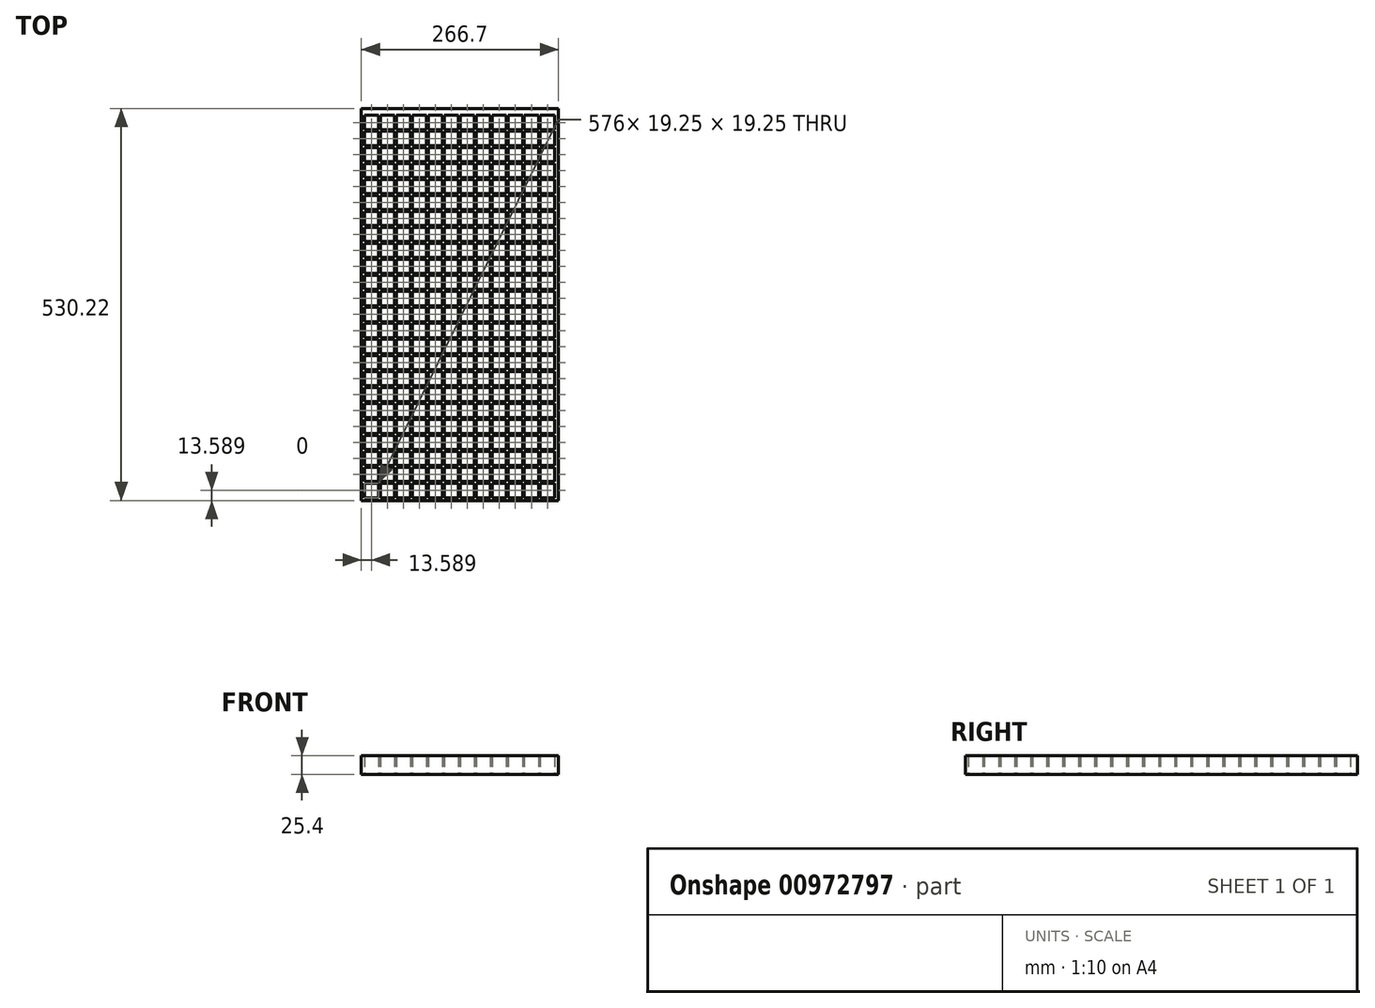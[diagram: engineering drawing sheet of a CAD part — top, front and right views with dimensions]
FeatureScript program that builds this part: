
annotation { "Feature Type Name" : "Feature", "Feature Type Description" : "" }
export const myFeature = defineFeature(function(context is Context, id is Id, definition is map)
    precondition{}
    {
        {
            var Q0;
            Q0=qCreatedBy(makeId("Top.planeOp"),FACE);
            var sketch = newSketch(context, id + "F0", { "sketchPlane" : qUnion([Q0])});
            skLineSegment(sketch, "E0.bottom", {"start": v(0, 0) * mm, "end": v(266.7, 0) * mm});
            skLineSegment(sketch, "E0.top", {"start": v(0, 530.23) * mm, "end": v(266.7, 530.23) * mm});
            skLineSegment(sketch, "E0.left", {"start": v(0, 0) * mm, "end": v(0, 530.23) * mm});
            skLineSegment(sketch, "E0.right", {"start": v(266.7, 0) * mm, "end": v(266.7, 530.22) * mm});
            skLineSegment(sketch, "E1.bottom", {"start": v(3.96, 23.22) * mm, "end": v(23.22, 23.22) * mm});
            skLineSegment(sketch, "E1.top", {"start": v(3.96, 3.96) * mm, "end": v(23.22, 3.96) * mm});
            skLineSegment(sketch, "E1.left", {"start": v(3.96, 23.22) * mm, "end": v(3.96, 3.96) * mm});
            skLineSegment(sketch, "E1.right", {"start": v(23.22, 23.22) * mm, "end": v(23.22, 3.96) * mm});
            skLineSegment(sketch, "E2.0.1.0", {"start": v(3.96, 44.86) * mm, "end": v(23.22, 44.86) * mm});
            skLineSegment(sketch, "E2.0.1.1", {"start": v(3.96, 25.6) * mm, "end": v(23.22, 25.6) * mm});
            skLineSegment(sketch, "E2.0.1.2", {"start": v(3.96, 44.86) * mm, "end": v(3.96, 25.6) * mm});
            skLineSegment(sketch, "E2.0.1.3", {"start": v(23.22, 44.86) * mm, "end": v(23.22, 25.6) * mm});
            skLineSegment(sketch, "E2.0.2.0", {"start": v(3.96, 66.5) * mm, "end": v(23.22, 66.5) * mm});
            skLineSegment(sketch, "E2.0.2.1", {"start": v(3.96, 47.24) * mm, "end": v(23.22, 47.24) * mm});
            skLineSegment(sketch, "E2.0.2.2", {"start": v(3.96, 66.5) * mm, "end": v(3.96, 47.24) * mm});
            skLineSegment(sketch, "E2.0.2.3", {"start": v(23.22, 66.5) * mm, "end": v(23.22, 47.24) * mm});
            skLineSegment(sketch, "E2.0.3.0", {"start": v(3.96, 88.14) * mm, "end": v(23.22, 88.14) * mm});
            skLineSegment(sketch, "E2.0.3.1", {"start": v(3.96, 68.88) * mm, "end": v(23.22, 68.88) * mm});
            skLineSegment(sketch, "E2.0.3.2", {"start": v(3.96, 88.14) * mm, "end": v(3.96, 68.88) * mm});
            skLineSegment(sketch, "E2.0.3.3", {"start": v(23.22, 88.14) * mm, "end": v(23.22, 68.88) * mm});
            skLineSegment(sketch, "E2.0.4.0", {"start": v(3.96, 109.78) * mm, "end": v(23.22, 109.78) * mm});
            skLineSegment(sketch, "E2.0.4.1", {"start": v(3.96, 90.53) * mm, "end": v(23.22, 90.53) * mm});
            skLineSegment(sketch, "E2.0.4.2", {"start": v(3.96, 109.78) * mm, "end": v(3.96, 90.53) * mm});
            skLineSegment(sketch, "E2.0.4.3", {"start": v(23.22, 109.78) * mm, "end": v(23.22, 90.53) * mm});
            skLineSegment(sketch, "E2.0.5.0", {"start": v(3.96, 131.42) * mm, "end": v(23.22, 131.42) * mm});
            skLineSegment(sketch, "E2.0.5.1", {"start": v(3.96, 112.17) * mm, "end": v(23.22, 112.17) * mm});
            skLineSegment(sketch, "E2.0.5.2", {"start": v(3.96, 131.42) * mm, "end": v(3.96, 112.17) * mm});
            skLineSegment(sketch, "E2.0.5.3", {"start": v(23.22, 131.42) * mm, "end": v(23.22, 112.17) * mm});
            skLineSegment(sketch, "E2.0.6.0", {"start": v(3.96, 153.06) * mm, "end": v(23.22, 153.06) * mm});
            skLineSegment(sketch, "E2.0.6.1", {"start": v(3.96, 133.8) * mm, "end": v(23.22, 133.8) * mm});
            skLineSegment(sketch, "E2.0.6.2", {"start": v(3.96, 153.06) * mm, "end": v(3.96, 133.8) * mm});
            skLineSegment(sketch, "E2.0.6.3", {"start": v(23.22, 153.06) * mm, "end": v(23.22, 133.8) * mm});
            skLineSegment(sketch, "E2.0.7.0", {"start": v(3.96, 174.7) * mm, "end": v(23.22, 174.7) * mm});
            skLineSegment(sketch, "E2.0.7.1", {"start": v(3.96, 155.45) * mm, "end": v(23.22, 155.45) * mm});
            skLineSegment(sketch, "E2.0.7.2", {"start": v(3.96, 174.7) * mm, "end": v(3.96, 155.45) * mm});
            skLineSegment(sketch, "E2.0.7.3", {"start": v(23.22, 174.7) * mm, "end": v(23.22, 155.45) * mm});
            skLineSegment(sketch, "E2.0.8.0", {"start": v(3.96, 196.34) * mm, "end": v(23.22, 196.34) * mm});
            skLineSegment(sketch, "E2.0.8.1", {"start": v(3.96, 177.09) * mm, "end": v(23.22, 177.09) * mm});
            skLineSegment(sketch, "E2.0.8.2", {"start": v(3.96, 196.34) * mm, "end": v(3.96, 177.09) * mm});
            skLineSegment(sketch, "E2.0.8.3", {"start": v(23.22, 196.34) * mm, "end": v(23.22, 177.09) * mm});
            skLineSegment(sketch, "E2.0.9.0", {"start": v(3.96, 217.98) * mm, "end": v(23.22, 217.98) * mm});
            skLineSegment(sketch, "E2.0.9.1", {"start": v(3.96, 198.73) * mm, "end": v(23.22, 198.73) * mm});
            skLineSegment(sketch, "E2.0.9.2", {"start": v(3.96, 217.98) * mm, "end": v(3.96, 198.73) * mm});
            skLineSegment(sketch, "E2.0.9.3", {"start": v(23.22, 217.98) * mm, "end": v(23.22, 198.73) * mm});
            skLineSegment(sketch, "E2.0.10.0", {"start": v(3.96, 239.62) * mm, "end": v(23.22, 239.62) * mm});
            skLineSegment(sketch, "E2.0.10.1", {"start": v(3.96, 220.37) * mm, "end": v(23.22, 220.37) * mm});
            skLineSegment(sketch, "E2.0.10.2", {"start": v(3.96, 239.62) * mm, "end": v(3.96, 220.37) * mm});
            skLineSegment(sketch, "E2.0.10.3", {"start": v(23.22, 239.62) * mm, "end": v(23.22, 220.37) * mm});
            skLineSegment(sketch, "E2.0.11.0", {"start": v(3.96, 261.26) * mm, "end": v(23.22, 261.26) * mm});
            skLineSegment(sketch, "E2.0.11.1", {"start": v(3.96, 242.01) * mm, "end": v(23.22, 242.01) * mm});
            skLineSegment(sketch, "E2.0.11.2", {"start": v(3.96, 261.26) * mm, "end": v(3.96, 242.01) * mm});
            skLineSegment(sketch, "E2.0.11.3", {"start": v(23.22, 261.26) * mm, "end": v(23.22, 242.01) * mm});
            skLineSegment(sketch, "E2.0.12.0", {"start": v(3.96, 282.9) * mm, "end": v(23.22, 282.9) * mm});
            skLineSegment(sketch, "E2.0.12.1", {"start": v(3.96, 263.65) * mm, "end": v(23.22, 263.65) * mm});
            skLineSegment(sketch, "E2.0.12.2", {"start": v(3.96, 282.9) * mm, "end": v(3.96, 263.65) * mm});
            skLineSegment(sketch, "E2.0.12.3", {"start": v(23.22, 282.9) * mm, "end": v(23.22, 263.65) * mm});
            skLineSegment(sketch, "E2.0.13.0", {"start": v(3.96, 304.55) * mm, "end": v(23.22, 304.55) * mm});
            skLineSegment(sketch, "E2.0.13.1", {"start": v(3.96, 285.3) * mm, "end": v(23.22, 285.3) * mm});
            skLineSegment(sketch, "E2.0.13.2", {"start": v(3.96, 304.55) * mm, "end": v(3.96, 285.3) * mm});
            skLineSegment(sketch, "E2.0.13.3", {"start": v(23.22, 304.55) * mm, "end": v(23.22, 285.3) * mm});
            skLineSegment(sketch, "E2.0.14.0", {"start": v(3.96, 326.19) * mm, "end": v(23.22, 326.19) * mm});
            skLineSegment(sketch, "E2.0.14.1", {"start": v(3.96, 306.93) * mm, "end": v(23.22, 306.93) * mm});
            skLineSegment(sketch, "E2.0.14.2", {"start": v(3.96, 326.19) * mm, "end": v(3.96, 306.93) * mm});
            skLineSegment(sketch, "E2.0.14.3", {"start": v(23.22, 326.19) * mm, "end": v(23.22, 306.93) * mm});
            skLineSegment(sketch, "E2.0.15.0", {"start": v(3.96, 347.83) * mm, "end": v(23.22, 347.83) * mm});
            skLineSegment(sketch, "E2.0.15.1", {"start": v(3.96, 328.57) * mm, "end": v(23.22, 328.57) * mm});
            skLineSegment(sketch, "E2.0.15.2", {"start": v(3.96, 347.83) * mm, "end": v(3.96, 328.57) * mm});
            skLineSegment(sketch, "E2.0.15.3", {"start": v(23.22, 347.83) * mm, "end": v(23.22, 328.57) * mm});
            skLineSegment(sketch, "E2.0.16.0", {"start": v(3.96, 369.47) * mm, "end": v(23.22, 369.47) * mm});
            skLineSegment(sketch, "E2.0.16.1", {"start": v(3.96, 350.22) * mm, "end": v(23.22, 350.22) * mm});
            skLineSegment(sketch, "E2.0.16.2", {"start": v(3.96, 369.47) * mm, "end": v(3.96, 350.22) * mm});
            skLineSegment(sketch, "E2.0.16.3", {"start": v(23.22, 369.47) * mm, "end": v(23.22, 350.22) * mm});
            skLineSegment(sketch, "E2.0.17.0", {"start": v(3.96, 391.1) * mm, "end": v(23.22, 391.1) * mm});
            skLineSegment(sketch, "E2.0.17.1", {"start": v(3.96, 371.86) * mm, "end": v(23.22, 371.86) * mm});
            skLineSegment(sketch, "E2.0.17.2", {"start": v(3.96, 391.1) * mm, "end": v(3.96, 371.86) * mm});
            skLineSegment(sketch, "E2.0.17.3", {"start": v(23.22, 391.1) * mm, "end": v(23.22, 371.86) * mm});
            skLineSegment(sketch, "E2.0.18.0", {"start": v(3.96, 412.75) * mm, "end": v(23.22, 412.75) * mm});
            skLineSegment(sketch, "E2.0.18.1", {"start": v(3.96, 393.5) * mm, "end": v(23.22, 393.5) * mm});
            skLineSegment(sketch, "E2.0.18.2", {"start": v(3.96, 412.75) * mm, "end": v(3.96, 393.5) * mm});
            skLineSegment(sketch, "E2.0.18.3", {"start": v(23.22, 412.75) * mm, "end": v(23.22, 393.5) * mm});
            skLineSegment(sketch, "E2.0.19.0", {"start": v(3.96, 434.4) * mm, "end": v(23.22, 434.4) * mm});
            skLineSegment(sketch, "E2.0.19.1", {"start": v(3.96, 415.14) * mm, "end": v(23.22, 415.14) * mm});
            skLineSegment(sketch, "E2.0.19.2", {"start": v(3.96, 434.4) * mm, "end": v(3.96, 415.14) * mm});
            skLineSegment(sketch, "E2.0.19.3", {"start": v(23.22, 434.4) * mm, "end": v(23.22, 415.14) * mm});
            skLineSegment(sketch, "E2.0.20.0", {"start": v(3.96, 456.03) * mm, "end": v(23.22, 456.03) * mm});
            skLineSegment(sketch, "E2.0.20.1", {"start": v(3.96, 436.78) * mm, "end": v(23.22, 436.78) * mm});
            skLineSegment(sketch, "E2.0.20.2", {"start": v(3.96, 456.03) * mm, "end": v(3.96, 436.78) * mm});
            skLineSegment(sketch, "E2.0.20.3", {"start": v(23.22, 456.03) * mm, "end": v(23.22, 436.78) * mm});
            skLineSegment(sketch, "E2.0.21.0", {"start": v(3.96, 477.67) * mm, "end": v(23.22, 477.67) * mm});
            skLineSegment(sketch, "E2.0.21.1", {"start": v(3.96, 458.42) * mm, "end": v(23.22, 458.42) * mm});
            skLineSegment(sketch, "E2.0.21.2", {"start": v(3.96, 477.67) * mm, "end": v(3.96, 458.42) * mm});
            skLineSegment(sketch, "E2.0.21.3", {"start": v(23.22, 477.67) * mm, "end": v(23.22, 458.42) * mm});
            skLineSegment(sketch, "E2.0.22.0", {"start": v(3.96, 499.31) * mm, "end": v(23.22, 499.31) * mm});
            skLineSegment(sketch, "E2.0.22.1", {"start": v(3.96, 480.06) * mm, "end": v(23.22, 480.06) * mm});
            skLineSegment(sketch, "E2.0.22.2", {"start": v(3.96, 499.31) * mm, "end": v(3.96, 480.06) * mm});
            skLineSegment(sketch, "E2.0.22.3", {"start": v(23.22, 499.31) * mm, "end": v(23.22, 480.06) * mm});
            skLineSegment(sketch, "E2.0.23.0", {"start": v(3.96, 520.95) * mm, "end": v(23.22, 520.95) * mm});
            skLineSegment(sketch, "E2.0.23.1", {"start": v(3.96, 501.7) * mm, "end": v(23.22, 501.7) * mm});
            skLineSegment(sketch, "E2.0.23.2", {"start": v(3.96, 520.95) * mm, "end": v(3.96, 501.7) * mm});
            skLineSegment(sketch, "E2.0.23.3", {"start": v(23.22, 520.95) * mm, "end": v(23.22, 501.7) * mm});
            skLineSegment(sketch, "E2.1.0.0", {"start": v(25.6, 23.22) * mm, "end": v(44.86, 23.22) * mm});
            skLineSegment(sketch, "E2.1.0.1", {"start": v(25.6, 3.96) * mm, "end": v(44.86, 3.96) * mm});
            skLineSegment(sketch, "E2.1.0.2", {"start": v(25.6, 23.22) * mm, "end": v(25.6, 3.96) * mm});
            skLineSegment(sketch, "E2.1.0.3", {"start": v(44.86, 23.22) * mm, "end": v(44.86, 3.96) * mm});
            skLineSegment(sketch, "E2.1.1.0", {"start": v(25.6, 44.86) * mm, "end": v(44.86, 44.86) * mm});
            skLineSegment(sketch, "E2.1.1.1", {"start": v(25.6, 25.6) * mm, "end": v(44.86, 25.6) * mm});
            skLineSegment(sketch, "E2.1.1.2", {"start": v(25.6, 44.86) * mm, "end": v(25.6, 25.6) * mm});
            skLineSegment(sketch, "E2.1.1.3", {"start": v(44.86, 44.86) * mm, "end": v(44.86, 25.6) * mm});
            skLineSegment(sketch, "E2.1.2.0", {"start": v(25.6, 66.5) * mm, "end": v(44.86, 66.5) * mm});
            skLineSegment(sketch, "E2.1.2.1", {"start": v(25.6, 47.24) * mm, "end": v(44.86, 47.24) * mm});
            skLineSegment(sketch, "E2.1.2.2", {"start": v(25.6, 66.5) * mm, "end": v(25.6, 47.24) * mm});
            skLineSegment(sketch, "E2.1.2.3", {"start": v(44.86, 66.5) * mm, "end": v(44.86, 47.24) * mm});
            skLineSegment(sketch, "E2.1.3.0", {"start": v(25.6, 88.14) * mm, "end": v(44.86, 88.14) * mm});
            skLineSegment(sketch, "E2.1.3.1", {"start": v(25.6, 68.88) * mm, "end": v(44.86, 68.88) * mm});
            skLineSegment(sketch, "E2.1.3.2", {"start": v(25.6, 88.14) * mm, "end": v(25.6, 68.88) * mm});
            skLineSegment(sketch, "E2.1.3.3", {"start": v(44.86, 88.14) * mm, "end": v(44.86, 68.88) * mm});
            skLineSegment(sketch, "E2.1.4.0", {"start": v(25.6, 109.78) * mm, "end": v(44.86, 109.78) * mm});
            skLineSegment(sketch, "E2.1.4.1", {"start": v(25.6, 90.53) * mm, "end": v(44.86, 90.53) * mm});
            skLineSegment(sketch, "E2.1.4.2", {"start": v(25.6, 109.78) * mm, "end": v(25.6, 90.53) * mm});
            skLineSegment(sketch, "E2.1.4.3", {"start": v(44.86, 109.78) * mm, "end": v(44.86, 90.53) * mm});
            skLineSegment(sketch, "E2.1.5.0", {"start": v(25.6, 131.42) * mm, "end": v(44.86, 131.42) * mm});
            skLineSegment(sketch, "E2.1.5.1", {"start": v(25.6, 112.17) * mm, "end": v(44.86, 112.17) * mm});
            skLineSegment(sketch, "E2.1.5.2", {"start": v(25.6, 131.42) * mm, "end": v(25.6, 112.17) * mm});
            skLineSegment(sketch, "E2.1.5.3", {"start": v(44.86, 131.42) * mm, "end": v(44.86, 112.17) * mm});
            skLineSegment(sketch, "E2.1.6.0", {"start": v(25.6, 153.06) * mm, "end": v(44.86, 153.06) * mm});
            skLineSegment(sketch, "E2.1.6.1", {"start": v(25.6, 133.8) * mm, "end": v(44.86, 133.8) * mm});
            skLineSegment(sketch, "E2.1.6.2", {"start": v(25.6, 153.06) * mm, "end": v(25.6, 133.8) * mm});
            skLineSegment(sketch, "E2.1.6.3", {"start": v(44.86, 153.06) * mm, "end": v(44.86, 133.8) * mm});
            skLineSegment(sketch, "E2.1.7.0", {"start": v(25.6, 174.7) * mm, "end": v(44.86, 174.7) * mm});
            skLineSegment(sketch, "E2.1.7.1", {"start": v(25.6, 155.45) * mm, "end": v(44.86, 155.45) * mm});
            skLineSegment(sketch, "E2.1.7.2", {"start": v(25.6, 174.7) * mm, "end": v(25.6, 155.45) * mm});
            skLineSegment(sketch, "E2.1.7.3", {"start": v(44.86, 174.7) * mm, "end": v(44.86, 155.45) * mm});
            skLineSegment(sketch, "E2.1.8.0", {"start": v(25.6, 196.34) * mm, "end": v(44.86, 196.34) * mm});
            skLineSegment(sketch, "E2.1.8.1", {"start": v(25.6, 177.09) * mm, "end": v(44.86, 177.09) * mm});
            skLineSegment(sketch, "E2.1.8.2", {"start": v(25.6, 196.34) * mm, "end": v(25.6, 177.09) * mm});
            skLineSegment(sketch, "E2.1.8.3", {"start": v(44.86, 196.34) * mm, "end": v(44.86, 177.09) * mm});
            skLineSegment(sketch, "E2.1.9.0", {"start": v(25.6, 217.98) * mm, "end": v(44.86, 217.98) * mm});
            skLineSegment(sketch, "E2.1.9.1", {"start": v(25.6, 198.73) * mm, "end": v(44.86, 198.73) * mm});
            skLineSegment(sketch, "E2.1.9.2", {"start": v(25.6, 217.98) * mm, "end": v(25.6, 198.73) * mm});
            skLineSegment(sketch, "E2.1.9.3", {"start": v(44.86, 217.98) * mm, "end": v(44.86, 198.73) * mm});
            skLineSegment(sketch, "E2.1.10.0", {"start": v(25.6, 239.62) * mm, "end": v(44.86, 239.62) * mm});
            skLineSegment(sketch, "E2.1.10.1", {"start": v(25.6, 220.37) * mm, "end": v(44.86, 220.37) * mm});
            skLineSegment(sketch, "E2.1.10.2", {"start": v(25.6, 239.62) * mm, "end": v(25.6, 220.37) * mm});
            skLineSegment(sketch, "E2.1.10.3", {"start": v(44.86, 239.62) * mm, "end": v(44.86, 220.37) * mm});
            skLineSegment(sketch, "E2.1.11.0", {"start": v(25.6, 261.26) * mm, "end": v(44.86, 261.26) * mm});
            skLineSegment(sketch, "E2.1.11.1", {"start": v(25.6, 242.01) * mm, "end": v(44.86, 242.01) * mm});
            skLineSegment(sketch, "E2.1.11.2", {"start": v(25.6, 261.26) * mm, "end": v(25.6, 242.01) * mm});
            skLineSegment(sketch, "E2.1.11.3", {"start": v(44.86, 261.26) * mm, "end": v(44.86, 242.01) * mm});
            skLineSegment(sketch, "E2.1.12.0", {"start": v(25.6, 282.9) * mm, "end": v(44.86, 282.9) * mm});
            skLineSegment(sketch, "E2.1.12.1", {"start": v(25.6, 263.65) * mm, "end": v(44.86, 263.65) * mm});
            skLineSegment(sketch, "E2.1.12.2", {"start": v(25.6, 282.9) * mm, "end": v(25.6, 263.65) * mm});
            skLineSegment(sketch, "E2.1.12.3", {"start": v(44.86, 282.9) * mm, "end": v(44.86, 263.65) * mm});
            skLineSegment(sketch, "E2.1.13.0", {"start": v(25.6, 304.55) * mm, "end": v(44.86, 304.55) * mm});
            skLineSegment(sketch, "E2.1.13.1", {"start": v(25.6, 285.3) * mm, "end": v(44.86, 285.3) * mm});
            skLineSegment(sketch, "E2.1.13.2", {"start": v(25.6, 304.55) * mm, "end": v(25.6, 285.3) * mm});
            skLineSegment(sketch, "E2.1.13.3", {"start": v(44.86, 304.55) * mm, "end": v(44.86, 285.3) * mm});
            skLineSegment(sketch, "E2.1.14.0", {"start": v(25.6, 326.19) * mm, "end": v(44.86, 326.19) * mm});
            skLineSegment(sketch, "E2.1.14.1", {"start": v(25.6, 306.93) * mm, "end": v(44.86, 306.93) * mm});
            skLineSegment(sketch, "E2.1.14.2", {"start": v(25.6, 326.19) * mm, "end": v(25.6, 306.93) * mm});
            skLineSegment(sketch, "E2.1.14.3", {"start": v(44.86, 326.19) * mm, "end": v(44.86, 306.93) * mm});
            skLineSegment(sketch, "E2.1.15.0", {"start": v(25.6, 347.83) * mm, "end": v(44.86, 347.83) * mm});
            skLineSegment(sketch, "E2.1.15.1", {"start": v(25.6, 328.57) * mm, "end": v(44.86, 328.57) * mm});
            skLineSegment(sketch, "E2.1.15.2", {"start": v(25.6, 347.83) * mm, "end": v(25.6, 328.57) * mm});
            skLineSegment(sketch, "E2.1.15.3", {"start": v(44.86, 347.83) * mm, "end": v(44.86, 328.57) * mm});
            skLineSegment(sketch, "E2.1.16.0", {"start": v(25.6, 369.47) * mm, "end": v(44.86, 369.47) * mm});
            skLineSegment(sketch, "E2.1.16.1", {"start": v(25.6, 350.22) * mm, "end": v(44.86, 350.22) * mm});
            skLineSegment(sketch, "E2.1.16.2", {"start": v(25.6, 369.47) * mm, "end": v(25.6, 350.22) * mm});
            skLineSegment(sketch, "E2.1.16.3", {"start": v(44.86, 369.47) * mm, "end": v(44.86, 350.22) * mm});
            skLineSegment(sketch, "E2.1.17.0", {"start": v(25.6, 391.1) * mm, "end": v(44.86, 391.1) * mm});
            skLineSegment(sketch, "E2.1.17.1", {"start": v(25.6, 371.86) * mm, "end": v(44.86, 371.86) * mm});
            skLineSegment(sketch, "E2.1.17.2", {"start": v(25.6, 391.1) * mm, "end": v(25.6, 371.86) * mm});
            skLineSegment(sketch, "E2.1.17.3", {"start": v(44.86, 391.1) * mm, "end": v(44.86, 371.86) * mm});
            skLineSegment(sketch, "E2.1.18.0", {"start": v(25.6, 412.75) * mm, "end": v(44.86, 412.75) * mm});
            skLineSegment(sketch, "E2.1.18.1", {"start": v(25.6, 393.5) * mm, "end": v(44.86, 393.5) * mm});
            skLineSegment(sketch, "E2.1.18.2", {"start": v(25.6, 412.75) * mm, "end": v(25.6, 393.5) * mm});
            skLineSegment(sketch, "E2.1.18.3", {"start": v(44.86, 412.75) * mm, "end": v(44.86, 393.5) * mm});
            skLineSegment(sketch, "E2.1.19.0", {"start": v(25.6, 434.4) * mm, "end": v(44.86, 434.4) * mm});
            skLineSegment(sketch, "E2.1.19.1", {"start": v(25.6, 415.14) * mm, "end": v(44.86, 415.14) * mm});
            skLineSegment(sketch, "E2.1.19.2", {"start": v(25.6, 434.4) * mm, "end": v(25.6, 415.14) * mm});
            skLineSegment(sketch, "E2.1.19.3", {"start": v(44.86, 434.4) * mm, "end": v(44.86, 415.14) * mm});
            skLineSegment(sketch, "E2.1.20.0", {"start": v(25.6, 456.03) * mm, "end": v(44.86, 456.03) * mm});
            skLineSegment(sketch, "E2.1.20.1", {"start": v(25.6, 436.78) * mm, "end": v(44.86, 436.78) * mm});
            skLineSegment(sketch, "E2.1.20.2", {"start": v(25.6, 456.03) * mm, "end": v(25.6, 436.78) * mm});
            skLineSegment(sketch, "E2.1.20.3", {"start": v(44.86, 456.03) * mm, "end": v(44.86, 436.78) * mm});
            skLineSegment(sketch, "E2.1.21.0", {"start": v(25.6, 477.67) * mm, "end": v(44.86, 477.67) * mm});
            skLineSegment(sketch, "E2.1.21.1", {"start": v(25.6, 458.42) * mm, "end": v(44.86, 458.42) * mm});
            skLineSegment(sketch, "E2.1.21.2", {"start": v(25.6, 477.67) * mm, "end": v(25.6, 458.42) * mm});
            skLineSegment(sketch, "E2.1.21.3", {"start": v(44.86, 477.67) * mm, "end": v(44.86, 458.42) * mm});
            skLineSegment(sketch, "E2.1.22.0", {"start": v(25.6, 499.31) * mm, "end": v(44.86, 499.31) * mm});
            skLineSegment(sketch, "E2.1.22.1", {"start": v(25.6, 480.06) * mm, "end": v(44.86, 480.06) * mm});
            skLineSegment(sketch, "E2.1.22.2", {"start": v(25.6, 499.31) * mm, "end": v(25.6, 480.06) * mm});
            skLineSegment(sketch, "E2.1.22.3", {"start": v(44.86, 499.31) * mm, "end": v(44.86, 480.06) * mm});
            skLineSegment(sketch, "E2.1.23.0", {"start": v(25.6, 520.95) * mm, "end": v(44.86, 520.95) * mm});
            skLineSegment(sketch, "E2.1.23.1", {"start": v(25.6, 501.7) * mm, "end": v(44.86, 501.7) * mm});
            skLineSegment(sketch, "E2.1.23.2", {"start": v(25.6, 520.95) * mm, "end": v(25.6, 501.7) * mm});
            skLineSegment(sketch, "E2.1.23.3", {"start": v(44.86, 520.95) * mm, "end": v(44.86, 501.7) * mm});
            skLineSegment(sketch, "E2.2.0.0", {"start": v(47.24, 23.22) * mm, "end": v(66.5, 23.22) * mm});
            skLineSegment(sketch, "E2.2.0.1", {"start": v(47.24, 3.96) * mm, "end": v(66.5, 3.96) * mm});
            skLineSegment(sketch, "E2.2.0.2", {"start": v(47.24, 23.22) * mm, "end": v(47.24, 3.96) * mm});
            skLineSegment(sketch, "E2.2.0.3", {"start": v(66.5, 23.22) * mm, "end": v(66.5, 3.96) * mm});
            skLineSegment(sketch, "E2.2.1.0", {"start": v(47.24, 44.86) * mm, "end": v(66.5, 44.86) * mm});
            skLineSegment(sketch, "E2.2.1.1", {"start": v(47.24, 25.6) * mm, "end": v(66.5, 25.6) * mm});
            skLineSegment(sketch, "E2.2.1.2", {"start": v(47.24, 44.86) * mm, "end": v(47.24, 25.6) * mm});
            skLineSegment(sketch, "E2.2.1.3", {"start": v(66.5, 44.86) * mm, "end": v(66.5, 25.6) * mm});
            skLineSegment(sketch, "E2.2.2.0", {"start": v(47.24, 66.5) * mm, "end": v(66.5, 66.5) * mm});
            skLineSegment(sketch, "E2.2.2.1", {"start": v(47.24, 47.24) * mm, "end": v(66.5, 47.24) * mm});
            skLineSegment(sketch, "E2.2.2.2", {"start": v(47.24, 66.5) * mm, "end": v(47.24, 47.24) * mm});
            skLineSegment(sketch, "E2.2.2.3", {"start": v(66.5, 66.5) * mm, "end": v(66.5, 47.24) * mm});
            skLineSegment(sketch, "E2.2.3.0", {"start": v(47.24, 88.14) * mm, "end": v(66.5, 88.14) * mm});
            skLineSegment(sketch, "E2.2.3.1", {"start": v(47.24, 68.88) * mm, "end": v(66.5, 68.88) * mm});
            skLineSegment(sketch, "E2.2.3.2", {"start": v(47.24, 88.14) * mm, "end": v(47.24, 68.88) * mm});
            skLineSegment(sketch, "E2.2.3.3", {"start": v(66.5, 88.14) * mm, "end": v(66.5, 68.88) * mm});
            skLineSegment(sketch, "E2.2.4.0", {"start": v(47.24, 109.78) * mm, "end": v(66.5, 109.78) * mm});
            skLineSegment(sketch, "E2.2.4.1", {"start": v(47.24, 90.53) * mm, "end": v(66.5, 90.53) * mm});
            skLineSegment(sketch, "E2.2.4.2", {"start": v(47.24, 109.78) * mm, "end": v(47.24, 90.53) * mm});
            skLineSegment(sketch, "E2.2.4.3", {"start": v(66.5, 109.78) * mm, "end": v(66.5, 90.53) * mm});
            skLineSegment(sketch, "E2.2.5.0", {"start": v(47.24, 131.42) * mm, "end": v(66.5, 131.42) * mm});
            skLineSegment(sketch, "E2.2.5.1", {"start": v(47.24, 112.17) * mm, "end": v(66.5, 112.17) * mm});
            skLineSegment(sketch, "E2.2.5.2", {"start": v(47.24, 131.42) * mm, "end": v(47.24, 112.17) * mm});
            skLineSegment(sketch, "E2.2.5.3", {"start": v(66.5, 131.42) * mm, "end": v(66.5, 112.17) * mm});
            skLineSegment(sketch, "E2.2.6.0", {"start": v(47.24, 153.06) * mm, "end": v(66.5, 153.06) * mm});
            skLineSegment(sketch, "E2.2.6.1", {"start": v(47.24, 133.8) * mm, "end": v(66.5, 133.8) * mm});
            skLineSegment(sketch, "E2.2.6.2", {"start": v(47.24, 153.06) * mm, "end": v(47.24, 133.8) * mm});
            skLineSegment(sketch, "E2.2.6.3", {"start": v(66.5, 153.06) * mm, "end": v(66.5, 133.8) * mm});
            skLineSegment(sketch, "E2.2.7.0", {"start": v(47.24, 174.7) * mm, "end": v(66.5, 174.7) * mm});
            skLineSegment(sketch, "E2.2.7.1", {"start": v(47.24, 155.45) * mm, "end": v(66.5, 155.45) * mm});
            skLineSegment(sketch, "E2.2.7.2", {"start": v(47.24, 174.7) * mm, "end": v(47.24, 155.45) * mm});
            skLineSegment(sketch, "E2.2.7.3", {"start": v(66.5, 174.7) * mm, "end": v(66.5, 155.45) * mm});
            skLineSegment(sketch, "E2.2.8.0", {"start": v(47.24, 196.34) * mm, "end": v(66.5, 196.34) * mm});
            skLineSegment(sketch, "E2.2.8.1", {"start": v(47.24, 177.09) * mm, "end": v(66.5, 177.09) * mm});
            skLineSegment(sketch, "E2.2.8.2", {"start": v(47.24, 196.34) * mm, "end": v(47.24, 177.09) * mm});
            skLineSegment(sketch, "E2.2.8.3", {"start": v(66.5, 196.34) * mm, "end": v(66.5, 177.09) * mm});
            skLineSegment(sketch, "E2.2.9.0", {"start": v(47.24, 217.98) * mm, "end": v(66.5, 217.98) * mm});
            skLineSegment(sketch, "E2.2.9.1", {"start": v(47.24, 198.73) * mm, "end": v(66.5, 198.73) * mm});
            skLineSegment(sketch, "E2.2.9.2", {"start": v(47.24, 217.98) * mm, "end": v(47.24, 198.73) * mm});
            skLineSegment(sketch, "E2.2.9.3", {"start": v(66.5, 217.98) * mm, "end": v(66.5, 198.73) * mm});
            skLineSegment(sketch, "E2.2.10.0", {"start": v(47.24, 239.62) * mm, "end": v(66.5, 239.62) * mm});
            skLineSegment(sketch, "E2.2.10.1", {"start": v(47.24, 220.37) * mm, "end": v(66.5, 220.37) * mm});
            skLineSegment(sketch, "E2.2.10.2", {"start": v(47.24, 239.62) * mm, "end": v(47.24, 220.37) * mm});
            skLineSegment(sketch, "E2.2.10.3", {"start": v(66.5, 239.62) * mm, "end": v(66.5, 220.37) * mm});
            skLineSegment(sketch, "E2.2.11.0", {"start": v(47.24, 261.26) * mm, "end": v(66.5, 261.26) * mm});
            skLineSegment(sketch, "E2.2.11.1", {"start": v(47.24, 242.01) * mm, "end": v(66.5, 242.01) * mm});
            skLineSegment(sketch, "E2.2.11.2", {"start": v(47.24, 261.26) * mm, "end": v(47.24, 242.01) * mm});
            skLineSegment(sketch, "E2.2.11.3", {"start": v(66.5, 261.26) * mm, "end": v(66.5, 242.01) * mm});
            skLineSegment(sketch, "E2.2.12.0", {"start": v(47.24, 282.9) * mm, "end": v(66.5, 282.9) * mm});
            skLineSegment(sketch, "E2.2.12.1", {"start": v(47.24, 263.65) * mm, "end": v(66.5, 263.65) * mm});
            skLineSegment(sketch, "E2.2.12.2", {"start": v(47.24, 282.9) * mm, "end": v(47.24, 263.65) * mm});
            skLineSegment(sketch, "E2.2.12.3", {"start": v(66.5, 282.9) * mm, "end": v(66.5, 263.65) * mm});
            skLineSegment(sketch, "E2.2.13.0", {"start": v(47.24, 304.55) * mm, "end": v(66.5, 304.55) * mm});
            skLineSegment(sketch, "E2.2.13.1", {"start": v(47.24, 285.3) * mm, "end": v(66.5, 285.3) * mm});
            skLineSegment(sketch, "E2.2.13.2", {"start": v(47.24, 304.55) * mm, "end": v(47.24, 285.3) * mm});
            skLineSegment(sketch, "E2.2.13.3", {"start": v(66.5, 304.55) * mm, "end": v(66.5, 285.3) * mm});
            skLineSegment(sketch, "E2.2.14.0", {"start": v(47.24, 326.19) * mm, "end": v(66.5, 326.19) * mm});
            skLineSegment(sketch, "E2.2.14.1", {"start": v(47.24, 306.93) * mm, "end": v(66.5, 306.93) * mm});
            skLineSegment(sketch, "E2.2.14.2", {"start": v(47.24, 326.19) * mm, "end": v(47.24, 306.93) * mm});
            skLineSegment(sketch, "E2.2.14.3", {"start": v(66.5, 326.19) * mm, "end": v(66.5, 306.93) * mm});
            skLineSegment(sketch, "E2.2.15.0", {"start": v(47.24, 347.83) * mm, "end": v(66.5, 347.83) * mm});
            skLineSegment(sketch, "E2.2.15.1", {"start": v(47.24, 328.57) * mm, "end": v(66.5, 328.57) * mm});
            skLineSegment(sketch, "E2.2.15.2", {"start": v(47.24, 347.83) * mm, "end": v(47.24, 328.57) * mm});
            skLineSegment(sketch, "E2.2.15.3", {"start": v(66.5, 347.83) * mm, "end": v(66.5, 328.57) * mm});
            skLineSegment(sketch, "E2.2.16.0", {"start": v(47.24, 369.47) * mm, "end": v(66.5, 369.47) * mm});
            skLineSegment(sketch, "E2.2.16.1", {"start": v(47.24, 350.22) * mm, "end": v(66.5, 350.22) * mm});
            skLineSegment(sketch, "E2.2.16.2", {"start": v(47.24, 369.47) * mm, "end": v(47.24, 350.22) * mm});
            skLineSegment(sketch, "E2.2.16.3", {"start": v(66.5, 369.47) * mm, "end": v(66.5, 350.22) * mm});
            skLineSegment(sketch, "E2.2.17.0", {"start": v(47.24, 391.1) * mm, "end": v(66.5, 391.1) * mm});
            skLineSegment(sketch, "E2.2.17.1", {"start": v(47.24, 371.86) * mm, "end": v(66.5, 371.86) * mm});
            skLineSegment(sketch, "E2.2.17.2", {"start": v(47.24, 391.1) * mm, "end": v(47.24, 371.86) * mm});
            skLineSegment(sketch, "E2.2.17.3", {"start": v(66.5, 391.1) * mm, "end": v(66.5, 371.86) * mm});
            skLineSegment(sketch, "E2.2.18.0", {"start": v(47.24, 412.75) * mm, "end": v(66.5, 412.75) * mm});
            skLineSegment(sketch, "E2.2.18.1", {"start": v(47.24, 393.5) * mm, "end": v(66.5, 393.5) * mm});
            skLineSegment(sketch, "E2.2.18.2", {"start": v(47.24, 412.75) * mm, "end": v(47.24, 393.5) * mm});
            skLineSegment(sketch, "E2.2.18.3", {"start": v(66.5, 412.75) * mm, "end": v(66.5, 393.5) * mm});
            skLineSegment(sketch, "E2.2.19.0", {"start": v(47.24, 434.4) * mm, "end": v(66.5, 434.4) * mm});
            skLineSegment(sketch, "E2.2.19.1", {"start": v(47.24, 415.14) * mm, "end": v(66.5, 415.14) * mm});
            skLineSegment(sketch, "E2.2.19.2", {"start": v(47.24, 434.4) * mm, "end": v(47.24, 415.14) * mm});
            skLineSegment(sketch, "E2.2.19.3", {"start": v(66.5, 434.4) * mm, "end": v(66.5, 415.14) * mm});
            skLineSegment(sketch, "E2.2.20.0", {"start": v(47.24, 456.03) * mm, "end": v(66.5, 456.03) * mm});
            skLineSegment(sketch, "E2.2.20.1", {"start": v(47.24, 436.78) * mm, "end": v(66.5, 436.78) * mm});
            skLineSegment(sketch, "E2.2.20.2", {"start": v(47.24, 456.03) * mm, "end": v(47.24, 436.78) * mm});
            skLineSegment(sketch, "E2.2.20.3", {"start": v(66.5, 456.03) * mm, "end": v(66.5, 436.78) * mm});
            skLineSegment(sketch, "E2.2.21.0", {"start": v(47.24, 477.67) * mm, "end": v(66.5, 477.67) * mm});
            skLineSegment(sketch, "E2.2.21.1", {"start": v(47.24, 458.42) * mm, "end": v(66.5, 458.42) * mm});
            skLineSegment(sketch, "E2.2.21.2", {"start": v(47.24, 477.67) * mm, "end": v(47.24, 458.42) * mm});
            skLineSegment(sketch, "E2.2.21.3", {"start": v(66.5, 477.67) * mm, "end": v(66.5, 458.42) * mm});
            skLineSegment(sketch, "E2.2.22.0", {"start": v(47.24, 499.31) * mm, "end": v(66.5, 499.31) * mm});
            skLineSegment(sketch, "E2.2.22.1", {"start": v(47.24, 480.06) * mm, "end": v(66.5, 480.06) * mm});
            skLineSegment(sketch, "E2.2.22.2", {"start": v(47.24, 499.31) * mm, "end": v(47.24, 480.06) * mm});
            skLineSegment(sketch, "E2.2.22.3", {"start": v(66.5, 499.31) * mm, "end": v(66.5, 480.06) * mm});
            skLineSegment(sketch, "E2.2.23.0", {"start": v(47.24, 520.95) * mm, "end": v(66.5, 520.95) * mm});
            skLineSegment(sketch, "E2.2.23.1", {"start": v(47.24, 501.7) * mm, "end": v(66.5, 501.7) * mm});
            skLineSegment(sketch, "E2.2.23.2", {"start": v(47.24, 520.95) * mm, "end": v(47.24, 501.7) * mm});
            skLineSegment(sketch, "E2.2.23.3", {"start": v(66.5, 520.95) * mm, "end": v(66.5, 501.7) * mm});
            skLineSegment(sketch, "E2.3.0.0", {"start": v(68.88, 23.22) * mm, "end": v(88.14, 23.22) * mm});
            skLineSegment(sketch, "E2.3.0.1", {"start": v(68.88, 3.96) * mm, "end": v(88.14, 3.96) * mm});
            skLineSegment(sketch, "E2.3.0.2", {"start": v(68.88, 23.22) * mm, "end": v(68.88, 3.96) * mm});
            skLineSegment(sketch, "E2.3.0.3", {"start": v(88.14, 23.22) * mm, "end": v(88.14, 3.96) * mm});
            skLineSegment(sketch, "E2.3.1.0", {"start": v(68.88, 44.86) * mm, "end": v(88.14, 44.86) * mm});
            skLineSegment(sketch, "E2.3.1.1", {"start": v(68.88, 25.6) * mm, "end": v(88.14, 25.6) * mm});
            skLineSegment(sketch, "E2.3.1.2", {"start": v(68.88, 44.86) * mm, "end": v(68.88, 25.6) * mm});
            skLineSegment(sketch, "E2.3.1.3", {"start": v(88.14, 44.86) * mm, "end": v(88.14, 25.6) * mm});
            skLineSegment(sketch, "E2.3.2.0", {"start": v(68.88, 66.5) * mm, "end": v(88.14, 66.5) * mm});
            skLineSegment(sketch, "E2.3.2.1", {"start": v(68.88, 47.24) * mm, "end": v(88.14, 47.24) * mm});
            skLineSegment(sketch, "E2.3.2.2", {"start": v(68.88, 66.5) * mm, "end": v(68.88, 47.24) * mm});
            skLineSegment(sketch, "E2.3.2.3", {"start": v(88.14, 66.5) * mm, "end": v(88.14, 47.24) * mm});
            skLineSegment(sketch, "E2.3.3.0", {"start": v(68.88, 88.14) * mm, "end": v(88.14, 88.14) * mm});
            skLineSegment(sketch, "E2.3.3.1", {"start": v(68.88, 68.88) * mm, "end": v(88.14, 68.88) * mm});
            skLineSegment(sketch, "E2.3.3.2", {"start": v(68.88, 88.14) * mm, "end": v(68.88, 68.88) * mm});
            skLineSegment(sketch, "E2.3.3.3", {"start": v(88.14, 88.14) * mm, "end": v(88.14, 68.88) * mm});
            skLineSegment(sketch, "E2.3.4.0", {"start": v(68.88, 109.78) * mm, "end": v(88.14, 109.78) * mm});
            skLineSegment(sketch, "E2.3.4.1", {"start": v(68.88, 90.53) * mm, "end": v(88.14, 90.53) * mm});
            skLineSegment(sketch, "E2.3.4.2", {"start": v(68.88, 109.78) * mm, "end": v(68.88, 90.53) * mm});
            skLineSegment(sketch, "E2.3.4.3", {"start": v(88.14, 109.78) * mm, "end": v(88.14, 90.53) * mm});
            skLineSegment(sketch, "E2.3.5.0", {"start": v(68.88, 131.42) * mm, "end": v(88.14, 131.42) * mm});
            skLineSegment(sketch, "E2.3.5.1", {"start": v(68.88, 112.17) * mm, "end": v(88.14, 112.17) * mm});
            skLineSegment(sketch, "E2.3.5.2", {"start": v(68.88, 131.42) * mm, "end": v(68.88, 112.17) * mm});
            skLineSegment(sketch, "E2.3.5.3", {"start": v(88.14, 131.42) * mm, "end": v(88.14, 112.17) * mm});
            skLineSegment(sketch, "E2.3.6.0", {"start": v(68.88, 153.06) * mm, "end": v(88.14, 153.06) * mm});
            skLineSegment(sketch, "E2.3.6.1", {"start": v(68.88, 133.8) * mm, "end": v(88.14, 133.8) * mm});
            skLineSegment(sketch, "E2.3.6.2", {"start": v(68.88, 153.06) * mm, "end": v(68.88, 133.8) * mm});
            skLineSegment(sketch, "E2.3.6.3", {"start": v(88.14, 153.06) * mm, "end": v(88.14, 133.8) * mm});
            skLineSegment(sketch, "E2.3.7.0", {"start": v(68.88, 174.7) * mm, "end": v(88.14, 174.7) * mm});
            skLineSegment(sketch, "E2.3.7.1", {"start": v(68.88, 155.45) * mm, "end": v(88.14, 155.45) * mm});
            skLineSegment(sketch, "E2.3.7.2", {"start": v(68.88, 174.7) * mm, "end": v(68.88, 155.45) * mm});
            skLineSegment(sketch, "E2.3.7.3", {"start": v(88.14, 174.7) * mm, "end": v(88.14, 155.45) * mm});
            skLineSegment(sketch, "E2.3.8.0", {"start": v(68.88, 196.34) * mm, "end": v(88.14, 196.34) * mm});
            skLineSegment(sketch, "E2.3.8.1", {"start": v(68.88, 177.09) * mm, "end": v(88.14, 177.09) * mm});
            skLineSegment(sketch, "E2.3.8.2", {"start": v(68.88, 196.34) * mm, "end": v(68.88, 177.09) * mm});
            skLineSegment(sketch, "E2.3.8.3", {"start": v(88.14, 196.34) * mm, "end": v(88.14, 177.09) * mm});
            skLineSegment(sketch, "E2.3.9.0", {"start": v(68.88, 217.98) * mm, "end": v(88.14, 217.98) * mm});
            skLineSegment(sketch, "E2.3.9.1", {"start": v(68.88, 198.73) * mm, "end": v(88.14, 198.73) * mm});
            skLineSegment(sketch, "E2.3.9.2", {"start": v(68.88, 217.98) * mm, "end": v(68.88, 198.73) * mm});
            skLineSegment(sketch, "E2.3.9.3", {"start": v(88.14, 217.98) * mm, "end": v(88.14, 198.73) * mm});
            skLineSegment(sketch, "E2.3.10.0", {"start": v(68.88, 239.62) * mm, "end": v(88.14, 239.62) * mm});
            skLineSegment(sketch, "E2.3.10.1", {"start": v(68.88, 220.37) * mm, "end": v(88.14, 220.37) * mm});
            skLineSegment(sketch, "E2.3.10.2", {"start": v(68.88, 239.62) * mm, "end": v(68.88, 220.37) * mm});
            skLineSegment(sketch, "E2.3.10.3", {"start": v(88.14, 239.62) * mm, "end": v(88.14, 220.37) * mm});
            skLineSegment(sketch, "E2.3.11.0", {"start": v(68.88, 261.26) * mm, "end": v(88.14, 261.26) * mm});
            skLineSegment(sketch, "E2.3.11.1", {"start": v(68.88, 242.01) * mm, "end": v(88.14, 242.01) * mm});
            skLineSegment(sketch, "E2.3.11.2", {"start": v(68.88, 261.26) * mm, "end": v(68.88, 242.01) * mm});
            skLineSegment(sketch, "E2.3.11.3", {"start": v(88.14, 261.26) * mm, "end": v(88.14, 242.01) * mm});
            skLineSegment(sketch, "E2.3.12.0", {"start": v(68.88, 282.9) * mm, "end": v(88.14, 282.9) * mm});
            skLineSegment(sketch, "E2.3.12.1", {"start": v(68.88, 263.65) * mm, "end": v(88.14, 263.65) * mm});
            skLineSegment(sketch, "E2.3.12.2", {"start": v(68.88, 282.9) * mm, "end": v(68.88, 263.65) * mm});
            skLineSegment(sketch, "E2.3.12.3", {"start": v(88.14, 282.9) * mm, "end": v(88.14, 263.65) * mm});
            skLineSegment(sketch, "E2.3.13.0", {"start": v(68.88, 304.55) * mm, "end": v(88.14, 304.55) * mm});
            skLineSegment(sketch, "E2.3.13.1", {"start": v(68.88, 285.3) * mm, "end": v(88.14, 285.3) * mm});
            skLineSegment(sketch, "E2.3.13.2", {"start": v(68.88, 304.55) * mm, "end": v(68.88, 285.3) * mm});
            skLineSegment(sketch, "E2.3.13.3", {"start": v(88.14, 304.55) * mm, "end": v(88.14, 285.3) * mm});
            skLineSegment(sketch, "E2.3.14.0", {"start": v(68.88, 326.19) * mm, "end": v(88.14, 326.19) * mm});
            skLineSegment(sketch, "E2.3.14.1", {"start": v(68.88, 306.93) * mm, "end": v(88.14, 306.93) * mm});
            skLineSegment(sketch, "E2.3.14.2", {"start": v(68.88, 326.19) * mm, "end": v(68.88, 306.93) * mm});
            skLineSegment(sketch, "E2.3.14.3", {"start": v(88.14, 326.19) * mm, "end": v(88.14, 306.93) * mm});
            skLineSegment(sketch, "E2.3.15.0", {"start": v(68.88, 347.83) * mm, "end": v(88.14, 347.83) * mm});
            skLineSegment(sketch, "E2.3.15.1", {"start": v(68.88, 328.57) * mm, "end": v(88.14, 328.57) * mm});
            skLineSegment(sketch, "E2.3.15.2", {"start": v(68.88, 347.83) * mm, "end": v(68.88, 328.57) * mm});
            skLineSegment(sketch, "E2.3.15.3", {"start": v(88.14, 347.83) * mm, "end": v(88.14, 328.57) * mm});
            skLineSegment(sketch, "E2.3.16.0", {"start": v(68.88, 369.47) * mm, "end": v(88.14, 369.47) * mm});
            skLineSegment(sketch, "E2.3.16.1", {"start": v(68.88, 350.22) * mm, "end": v(88.14, 350.22) * mm});
            skLineSegment(sketch, "E2.3.16.2", {"start": v(68.88, 369.47) * mm, "end": v(68.88, 350.22) * mm});
            skLineSegment(sketch, "E2.3.16.3", {"start": v(88.14, 369.47) * mm, "end": v(88.14, 350.22) * mm});
            skLineSegment(sketch, "E2.3.17.0", {"start": v(68.88, 391.1) * mm, "end": v(88.14, 391.1) * mm});
            skLineSegment(sketch, "E2.3.17.1", {"start": v(68.88, 371.86) * mm, "end": v(88.14, 371.86) * mm});
            skLineSegment(sketch, "E2.3.17.2", {"start": v(68.88, 391.1) * mm, "end": v(68.88, 371.86) * mm});
            skLineSegment(sketch, "E2.3.17.3", {"start": v(88.14, 391.1) * mm, "end": v(88.14, 371.86) * mm});
            skLineSegment(sketch, "E2.3.18.0", {"start": v(68.88, 412.75) * mm, "end": v(88.14, 412.75) * mm});
            skLineSegment(sketch, "E2.3.18.1", {"start": v(68.88, 393.5) * mm, "end": v(88.14, 393.5) * mm});
            skLineSegment(sketch, "E2.3.18.2", {"start": v(68.88, 412.75) * mm, "end": v(68.88, 393.5) * mm});
            skLineSegment(sketch, "E2.3.18.3", {"start": v(88.14, 412.75) * mm, "end": v(88.14, 393.5) * mm});
            skLineSegment(sketch, "E2.3.19.0", {"start": v(68.88, 434.4) * mm, "end": v(88.14, 434.4) * mm});
            skLineSegment(sketch, "E2.3.19.1", {"start": v(68.88, 415.14) * mm, "end": v(88.14, 415.14) * mm});
            skLineSegment(sketch, "E2.3.19.2", {"start": v(68.88, 434.4) * mm, "end": v(68.88, 415.14) * mm});
            skLineSegment(sketch, "E2.3.19.3", {"start": v(88.14, 434.4) * mm, "end": v(88.14, 415.14) * mm});
            skLineSegment(sketch, "E2.3.20.0", {"start": v(68.88, 456.03) * mm, "end": v(88.14, 456.03) * mm});
            skLineSegment(sketch, "E2.3.20.1", {"start": v(68.88, 436.78) * mm, "end": v(88.14, 436.78) * mm});
            skLineSegment(sketch, "E2.3.20.2", {"start": v(68.88, 456.03) * mm, "end": v(68.88, 436.78) * mm});
            skLineSegment(sketch, "E2.3.20.3", {"start": v(88.14, 456.03) * mm, "end": v(88.14, 436.78) * mm});
            skLineSegment(sketch, "E2.3.21.0", {"start": v(68.88, 477.67) * mm, "end": v(88.14, 477.67) * mm});
            skLineSegment(sketch, "E2.3.21.1", {"start": v(68.88, 458.42) * mm, "end": v(88.14, 458.42) * mm});
            skLineSegment(sketch, "E2.3.21.2", {"start": v(68.88, 477.67) * mm, "end": v(68.88, 458.42) * mm});
            skLineSegment(sketch, "E2.3.21.3", {"start": v(88.14, 477.67) * mm, "end": v(88.14, 458.42) * mm});
            skLineSegment(sketch, "E2.3.22.0", {"start": v(68.88, 499.31) * mm, "end": v(88.14, 499.31) * mm});
            skLineSegment(sketch, "E2.3.22.1", {"start": v(68.88, 480.06) * mm, "end": v(88.14, 480.06) * mm});
            skLineSegment(sketch, "E2.3.22.2", {"start": v(68.88, 499.31) * mm, "end": v(68.88, 480.06) * mm});
            skLineSegment(sketch, "E2.3.22.3", {"start": v(88.14, 499.31) * mm, "end": v(88.14, 480.06) * mm});
            skLineSegment(sketch, "E2.3.23.0", {"start": v(68.88, 520.95) * mm, "end": v(88.14, 520.95) * mm});
            skLineSegment(sketch, "E2.3.23.1", {"start": v(68.88, 501.7) * mm, "end": v(88.14, 501.7) * mm});
            skLineSegment(sketch, "E2.3.23.2", {"start": v(68.88, 520.95) * mm, "end": v(68.88, 501.7) * mm});
            skLineSegment(sketch, "E2.3.23.3", {"start": v(88.14, 520.95) * mm, "end": v(88.14, 501.7) * mm});
            skLineSegment(sketch, "E2.4.0.0", {"start": v(90.53, 23.22) * mm, "end": v(109.78, 23.22) * mm});
            skLineSegment(sketch, "E2.4.0.1", {"start": v(90.53, 3.96) * mm, "end": v(109.78, 3.96) * mm});
            skLineSegment(sketch, "E2.4.0.2", {"start": v(90.53, 23.22) * mm, "end": v(90.53, 3.96) * mm});
            skLineSegment(sketch, "E2.4.0.3", {"start": v(109.78, 23.22) * mm, "end": v(109.78, 3.96) * mm});
            skLineSegment(sketch, "E2.4.1.0", {"start": v(90.53, 44.86) * mm, "end": v(109.78, 44.86) * mm});
            skLineSegment(sketch, "E2.4.1.1", {"start": v(90.53, 25.6) * mm, "end": v(109.78, 25.6) * mm});
            skLineSegment(sketch, "E2.4.1.2", {"start": v(90.53, 44.86) * mm, "end": v(90.53, 25.6) * mm});
            skLineSegment(sketch, "E2.4.1.3", {"start": v(109.78, 44.86) * mm, "end": v(109.78, 25.6) * mm});
            skLineSegment(sketch, "E2.4.2.0", {"start": v(90.53, 66.5) * mm, "end": v(109.78, 66.5) * mm});
            skLineSegment(sketch, "E2.4.2.1", {"start": v(90.53, 47.24) * mm, "end": v(109.78, 47.24) * mm});
            skLineSegment(sketch, "E2.4.2.2", {"start": v(90.53, 66.5) * mm, "end": v(90.53, 47.24) * mm});
            skLineSegment(sketch, "E2.4.2.3", {"start": v(109.78, 66.5) * mm, "end": v(109.78, 47.24) * mm});
            skLineSegment(sketch, "E2.4.3.0", {"start": v(90.53, 88.14) * mm, "end": v(109.78, 88.14) * mm});
            skLineSegment(sketch, "E2.4.3.1", {"start": v(90.53, 68.88) * mm, "end": v(109.78, 68.88) * mm});
            skLineSegment(sketch, "E2.4.3.2", {"start": v(90.53, 88.14) * mm, "end": v(90.53, 68.88) * mm});
            skLineSegment(sketch, "E2.4.3.3", {"start": v(109.78, 88.14) * mm, "end": v(109.78, 68.88) * mm});
            skLineSegment(sketch, "E2.4.4.0", {"start": v(90.53, 109.78) * mm, "end": v(109.78, 109.78) * mm});
            skLineSegment(sketch, "E2.4.4.1", {"start": v(90.53, 90.53) * mm, "end": v(109.78, 90.53) * mm});
            skLineSegment(sketch, "E2.4.4.2", {"start": v(90.53, 109.78) * mm, "end": v(90.53, 90.53) * mm});
            skLineSegment(sketch, "E2.4.4.3", {"start": v(109.78, 109.78) * mm, "end": v(109.78, 90.53) * mm});
            skLineSegment(sketch, "E2.4.5.0", {"start": v(90.53, 131.42) * mm, "end": v(109.78, 131.42) * mm});
            skLineSegment(sketch, "E2.4.5.1", {"start": v(90.53, 112.17) * mm, "end": v(109.78, 112.17) * mm});
            skLineSegment(sketch, "E2.4.5.2", {"start": v(90.53, 131.42) * mm, "end": v(90.53, 112.17) * mm});
            skLineSegment(sketch, "E2.4.5.3", {"start": v(109.78, 131.42) * mm, "end": v(109.78, 112.17) * mm});
            skLineSegment(sketch, "E2.4.6.0", {"start": v(90.53, 153.06) * mm, "end": v(109.78, 153.06) * mm});
            skLineSegment(sketch, "E2.4.6.1", {"start": v(90.53, 133.8) * mm, "end": v(109.78, 133.8) * mm});
            skLineSegment(sketch, "E2.4.6.2", {"start": v(90.53, 153.06) * mm, "end": v(90.53, 133.8) * mm});
            skLineSegment(sketch, "E2.4.6.3", {"start": v(109.78, 153.06) * mm, "end": v(109.78, 133.8) * mm});
            skLineSegment(sketch, "E2.4.7.0", {"start": v(90.53, 174.7) * mm, "end": v(109.78, 174.7) * mm});
            skLineSegment(sketch, "E2.4.7.1", {"start": v(90.53, 155.45) * mm, "end": v(109.78, 155.45) * mm});
            skLineSegment(sketch, "E2.4.7.2", {"start": v(90.53, 174.7) * mm, "end": v(90.53, 155.45) * mm});
            skLineSegment(sketch, "E2.4.7.3", {"start": v(109.78, 174.7) * mm, "end": v(109.78, 155.45) * mm});
            skLineSegment(sketch, "E2.4.8.0", {"start": v(90.53, 196.34) * mm, "end": v(109.78, 196.34) * mm});
            skLineSegment(sketch, "E2.4.8.1", {"start": v(90.53, 177.09) * mm, "end": v(109.78, 177.09) * mm});
            skLineSegment(sketch, "E2.4.8.2", {"start": v(90.53, 196.34) * mm, "end": v(90.53, 177.09) * mm});
            skLineSegment(sketch, "E2.4.8.3", {"start": v(109.78, 196.34) * mm, "end": v(109.78, 177.09) * mm});
            skLineSegment(sketch, "E2.4.9.0", {"start": v(90.53, 217.98) * mm, "end": v(109.78, 217.98) * mm});
            skLineSegment(sketch, "E2.4.9.1", {"start": v(90.53, 198.73) * mm, "end": v(109.78, 198.73) * mm});
            skLineSegment(sketch, "E2.4.9.2", {"start": v(90.53, 217.98) * mm, "end": v(90.53, 198.73) * mm});
            skLineSegment(sketch, "E2.4.9.3", {"start": v(109.78, 217.98) * mm, "end": v(109.78, 198.73) * mm});
            skLineSegment(sketch, "E2.4.10.0", {"start": v(90.53, 239.62) * mm, "end": v(109.78, 239.62) * mm});
            skLineSegment(sketch, "E2.4.10.1", {"start": v(90.53, 220.37) * mm, "end": v(109.78, 220.37) * mm});
            skLineSegment(sketch, "E2.4.10.2", {"start": v(90.53, 239.62) * mm, "end": v(90.53, 220.37) * mm});
            skLineSegment(sketch, "E2.4.10.3", {"start": v(109.78, 239.62) * mm, "end": v(109.78, 220.37) * mm});
            skLineSegment(sketch, "E2.4.11.0", {"start": v(90.53, 261.26) * mm, "end": v(109.78, 261.26) * mm});
            skLineSegment(sketch, "E2.4.11.1", {"start": v(90.53, 242.01) * mm, "end": v(109.78, 242.01) * mm});
            skLineSegment(sketch, "E2.4.11.2", {"start": v(90.53, 261.26) * mm, "end": v(90.53, 242.01) * mm});
            skLineSegment(sketch, "E2.4.11.3", {"start": v(109.78, 261.26) * mm, "end": v(109.78, 242.01) * mm});
            skLineSegment(sketch, "E2.4.12.0", {"start": v(90.53, 282.9) * mm, "end": v(109.78, 282.9) * mm});
            skLineSegment(sketch, "E2.4.12.1", {"start": v(90.53, 263.65) * mm, "end": v(109.78, 263.65) * mm});
            skLineSegment(sketch, "E2.4.12.2", {"start": v(90.53, 282.9) * mm, "end": v(90.53, 263.65) * mm});
            skLineSegment(sketch, "E2.4.12.3", {"start": v(109.78, 282.9) * mm, "end": v(109.78, 263.65) * mm});
            skLineSegment(sketch, "E2.4.13.0", {"start": v(90.53, 304.55) * mm, "end": v(109.78, 304.55) * mm});
            skLineSegment(sketch, "E2.4.13.1", {"start": v(90.53, 285.3) * mm, "end": v(109.78, 285.3) * mm});
            skLineSegment(sketch, "E2.4.13.2", {"start": v(90.53, 304.55) * mm, "end": v(90.53, 285.3) * mm});
            skLineSegment(sketch, "E2.4.13.3", {"start": v(109.78, 304.55) * mm, "end": v(109.78, 285.3) * mm});
            skLineSegment(sketch, "E2.4.14.0", {"start": v(90.53, 326.19) * mm, "end": v(109.78, 326.19) * mm});
            skLineSegment(sketch, "E2.4.14.1", {"start": v(90.53, 306.93) * mm, "end": v(109.78, 306.93) * mm});
            skLineSegment(sketch, "E2.4.14.2", {"start": v(90.53, 326.19) * mm, "end": v(90.53, 306.93) * mm});
            skLineSegment(sketch, "E2.4.14.3", {"start": v(109.78, 326.19) * mm, "end": v(109.78, 306.93) * mm});
            skLineSegment(sketch, "E2.4.15.0", {"start": v(90.53, 347.83) * mm, "end": v(109.78, 347.83) * mm});
            skLineSegment(sketch, "E2.4.15.1", {"start": v(90.53, 328.57) * mm, "end": v(109.78, 328.57) * mm});
            skLineSegment(sketch, "E2.4.15.2", {"start": v(90.53, 347.83) * mm, "end": v(90.53, 328.57) * mm});
            skLineSegment(sketch, "E2.4.15.3", {"start": v(109.78, 347.83) * mm, "end": v(109.78, 328.57) * mm});
            skLineSegment(sketch, "E2.4.16.0", {"start": v(90.53, 369.47) * mm, "end": v(109.78, 369.47) * mm});
            skLineSegment(sketch, "E2.4.16.1", {"start": v(90.53, 350.22) * mm, "end": v(109.78, 350.22) * mm});
            skLineSegment(sketch, "E2.4.16.2", {"start": v(90.53, 369.47) * mm, "end": v(90.53, 350.22) * mm});
            skLineSegment(sketch, "E2.4.16.3", {"start": v(109.78, 369.47) * mm, "end": v(109.78, 350.22) * mm});
            skLineSegment(sketch, "E2.4.17.0", {"start": v(90.53, 391.1) * mm, "end": v(109.78, 391.1) * mm});
            skLineSegment(sketch, "E2.4.17.1", {"start": v(90.53, 371.86) * mm, "end": v(109.78, 371.86) * mm});
            skLineSegment(sketch, "E2.4.17.2", {"start": v(90.53, 391.1) * mm, "end": v(90.53, 371.86) * mm});
            skLineSegment(sketch, "E2.4.17.3", {"start": v(109.78, 391.1) * mm, "end": v(109.78, 371.86) * mm});
            skLineSegment(sketch, "E2.4.18.0", {"start": v(90.53, 412.75) * mm, "end": v(109.78, 412.75) * mm});
            skLineSegment(sketch, "E2.4.18.1", {"start": v(90.53, 393.5) * mm, "end": v(109.78, 393.5) * mm});
            skLineSegment(sketch, "E2.4.18.2", {"start": v(90.53, 412.75) * mm, "end": v(90.53, 393.5) * mm});
            skLineSegment(sketch, "E2.4.18.3", {"start": v(109.78, 412.75) * mm, "end": v(109.78, 393.5) * mm});
            skLineSegment(sketch, "E2.4.19.0", {"start": v(90.53, 434.4) * mm, "end": v(109.78, 434.4) * mm});
            skLineSegment(sketch, "E2.4.19.1", {"start": v(90.53, 415.14) * mm, "end": v(109.78, 415.14) * mm});
            skLineSegment(sketch, "E2.4.19.2", {"start": v(90.53, 434.4) * mm, "end": v(90.53, 415.14) * mm});
            skLineSegment(sketch, "E2.4.19.3", {"start": v(109.78, 434.4) * mm, "end": v(109.78, 415.14) * mm});
            skLineSegment(sketch, "E2.4.20.0", {"start": v(90.53, 456.03) * mm, "end": v(109.78, 456.03) * mm});
            skLineSegment(sketch, "E2.4.20.1", {"start": v(90.53, 436.78) * mm, "end": v(109.78, 436.78) * mm});
            skLineSegment(sketch, "E2.4.20.2", {"start": v(90.53, 456.03) * mm, "end": v(90.53, 436.78) * mm});
            skLineSegment(sketch, "E2.4.20.3", {"start": v(109.78, 456.03) * mm, "end": v(109.78, 436.78) * mm});
            skLineSegment(sketch, "E2.4.21.0", {"start": v(90.53, 477.67) * mm, "end": v(109.78, 477.67) * mm});
            skLineSegment(sketch, "E2.4.21.1", {"start": v(90.53, 458.42) * mm, "end": v(109.78, 458.42) * mm});
            skLineSegment(sketch, "E2.4.21.2", {"start": v(90.53, 477.67) * mm, "end": v(90.53, 458.42) * mm});
            skLineSegment(sketch, "E2.4.21.3", {"start": v(109.78, 477.67) * mm, "end": v(109.78, 458.42) * mm});
            skLineSegment(sketch, "E2.4.22.0", {"start": v(90.53, 499.31) * mm, "end": v(109.78, 499.31) * mm});
            skLineSegment(sketch, "E2.4.22.1", {"start": v(90.53, 480.06) * mm, "end": v(109.78, 480.06) * mm});
            skLineSegment(sketch, "E2.4.22.2", {"start": v(90.53, 499.31) * mm, "end": v(90.53, 480.06) * mm});
            skLineSegment(sketch, "E2.4.22.3", {"start": v(109.78, 499.31) * mm, "end": v(109.78, 480.06) * mm});
            skLineSegment(sketch, "E2.4.23.0", {"start": v(90.53, 520.95) * mm, "end": v(109.78, 520.95) * mm});
            skLineSegment(sketch, "E2.4.23.1", {"start": v(90.53, 501.7) * mm, "end": v(109.78, 501.7) * mm});
            skLineSegment(sketch, "E2.4.23.2", {"start": v(90.53, 520.95) * mm, "end": v(90.53, 501.7) * mm});
            skLineSegment(sketch, "E2.4.23.3", {"start": v(109.78, 520.95) * mm, "end": v(109.78, 501.7) * mm});
            skLineSegment(sketch, "E2.5.0.0", {"start": v(112.17, 23.22) * mm, "end": v(131.42, 23.22) * mm});
            skLineSegment(sketch, "E2.5.0.1", {"start": v(112.17, 3.96) * mm, "end": v(131.42, 3.96) * mm});
            skLineSegment(sketch, "E2.5.0.2", {"start": v(112.17, 23.22) * mm, "end": v(112.17, 3.96) * mm});
            skLineSegment(sketch, "E2.5.0.3", {"start": v(131.42, 23.22) * mm, "end": v(131.42, 3.96) * mm});
            skLineSegment(sketch, "E2.5.1.0", {"start": v(112.17, 44.86) * mm, "end": v(131.42, 44.86) * mm});
            skLineSegment(sketch, "E2.5.1.1", {"start": v(112.17, 25.6) * mm, "end": v(131.42, 25.6) * mm});
            skLineSegment(sketch, "E2.5.1.2", {"start": v(112.17, 44.86) * mm, "end": v(112.17, 25.6) * mm});
            skLineSegment(sketch, "E2.5.1.3", {"start": v(131.42, 44.86) * mm, "end": v(131.42, 25.6) * mm});
            skLineSegment(sketch, "E2.5.2.0", {"start": v(112.17, 66.5) * mm, "end": v(131.42, 66.5) * mm});
            skLineSegment(sketch, "E2.5.2.1", {"start": v(112.17, 47.24) * mm, "end": v(131.42, 47.24) * mm});
            skLineSegment(sketch, "E2.5.2.2", {"start": v(112.17, 66.5) * mm, "end": v(112.17, 47.24) * mm});
            skLineSegment(sketch, "E2.5.2.3", {"start": v(131.42, 66.5) * mm, "end": v(131.42, 47.24) * mm});
            skLineSegment(sketch, "E2.5.3.0", {"start": v(112.17, 88.14) * mm, "end": v(131.42, 88.14) * mm});
            skLineSegment(sketch, "E2.5.3.1", {"start": v(112.17, 68.88) * mm, "end": v(131.42, 68.88) * mm});
            skLineSegment(sketch, "E2.5.3.2", {"start": v(112.17, 88.14) * mm, "end": v(112.17, 68.88) * mm});
            skLineSegment(sketch, "E2.5.3.3", {"start": v(131.42, 88.14) * mm, "end": v(131.42, 68.88) * mm});
            skLineSegment(sketch, "E2.5.4.0", {"start": v(112.17, 109.78) * mm, "end": v(131.42, 109.78) * mm});
            skLineSegment(sketch, "E2.5.4.1", {"start": v(112.17, 90.53) * mm, "end": v(131.42, 90.53) * mm});
            skLineSegment(sketch, "E2.5.4.2", {"start": v(112.17, 109.78) * mm, "end": v(112.17, 90.53) * mm});
            skLineSegment(sketch, "E2.5.4.3", {"start": v(131.42, 109.78) * mm, "end": v(131.42, 90.53) * mm});
            skLineSegment(sketch, "E2.5.5.0", {"start": v(112.17, 131.42) * mm, "end": v(131.42, 131.42) * mm});
            skLineSegment(sketch, "E2.5.5.1", {"start": v(112.17, 112.17) * mm, "end": v(131.42, 112.17) * mm});
            skLineSegment(sketch, "E2.5.5.2", {"start": v(112.17, 131.42) * mm, "end": v(112.17, 112.17) * mm});
            skLineSegment(sketch, "E2.5.5.3", {"start": v(131.42, 131.42) * mm, "end": v(131.42, 112.17) * mm});
            skLineSegment(sketch, "E2.5.6.0", {"start": v(112.17, 153.06) * mm, "end": v(131.42, 153.06) * mm});
            skLineSegment(sketch, "E2.5.6.1", {"start": v(112.17, 133.8) * mm, "end": v(131.42, 133.8) * mm});
            skLineSegment(sketch, "E2.5.6.2", {"start": v(112.17, 153.06) * mm, "end": v(112.17, 133.8) * mm});
            skLineSegment(sketch, "E2.5.6.3", {"start": v(131.42, 153.06) * mm, "end": v(131.42, 133.8) * mm});
            skLineSegment(sketch, "E2.5.7.0", {"start": v(112.17, 174.7) * mm, "end": v(131.42, 174.7) * mm});
            skLineSegment(sketch, "E2.5.7.1", {"start": v(112.17, 155.45) * mm, "end": v(131.42, 155.45) * mm});
            skLineSegment(sketch, "E2.5.7.2", {"start": v(112.17, 174.7) * mm, "end": v(112.17, 155.45) * mm});
            skLineSegment(sketch, "E2.5.7.3", {"start": v(131.42, 174.7) * mm, "end": v(131.42, 155.45) * mm});
            skLineSegment(sketch, "E2.5.8.0", {"start": v(112.17, 196.34) * mm, "end": v(131.42, 196.34) * mm});
            skLineSegment(sketch, "E2.5.8.1", {"start": v(112.17, 177.09) * mm, "end": v(131.42, 177.09) * mm});
            skLineSegment(sketch, "E2.5.8.2", {"start": v(112.17, 196.34) * mm, "end": v(112.17, 177.09) * mm});
            skLineSegment(sketch, "E2.5.8.3", {"start": v(131.42, 196.34) * mm, "end": v(131.42, 177.09) * mm});
            skLineSegment(sketch, "E2.5.9.0", {"start": v(112.17, 217.98) * mm, "end": v(131.42, 217.98) * mm});
            skLineSegment(sketch, "E2.5.9.1", {"start": v(112.17, 198.73) * mm, "end": v(131.42, 198.73) * mm});
            skLineSegment(sketch, "E2.5.9.2", {"start": v(112.17, 217.98) * mm, "end": v(112.17, 198.73) * mm});
            skLineSegment(sketch, "E2.5.9.3", {"start": v(131.42, 217.98) * mm, "end": v(131.42, 198.73) * mm});
            skLineSegment(sketch, "E2.5.10.0", {"start": v(112.17, 239.62) * mm, "end": v(131.42, 239.62) * mm});
            skLineSegment(sketch, "E2.5.10.1", {"start": v(112.17, 220.37) * mm, "end": v(131.42, 220.37) * mm});
            skLineSegment(sketch, "E2.5.10.2", {"start": v(112.17, 239.62) * mm, "end": v(112.17, 220.37) * mm});
            skLineSegment(sketch, "E2.5.10.3", {"start": v(131.42, 239.62) * mm, "end": v(131.42, 220.37) * mm});
            skLineSegment(sketch, "E2.5.11.0", {"start": v(112.17, 261.26) * mm, "end": v(131.42, 261.26) * mm});
            skLineSegment(sketch, "E2.5.11.1", {"start": v(112.17, 242.01) * mm, "end": v(131.42, 242.01) * mm});
            skLineSegment(sketch, "E2.5.11.2", {"start": v(112.17, 261.26) * mm, "end": v(112.17, 242.01) * mm});
            skLineSegment(sketch, "E2.5.11.3", {"start": v(131.42, 261.26) * mm, "end": v(131.42, 242.01) * mm});
            skLineSegment(sketch, "E2.5.12.0", {"start": v(112.17, 282.9) * mm, "end": v(131.42, 282.9) * mm});
            skLineSegment(sketch, "E2.5.12.1", {"start": v(112.17, 263.65) * mm, "end": v(131.42, 263.65) * mm});
            skLineSegment(sketch, "E2.5.12.2", {"start": v(112.17, 282.9) * mm, "end": v(112.17, 263.65) * mm});
            skLineSegment(sketch, "E2.5.12.3", {"start": v(131.42, 282.9) * mm, "end": v(131.42, 263.65) * mm});
            skLineSegment(sketch, "E2.5.13.0", {"start": v(112.17, 304.55) * mm, "end": v(131.42, 304.55) * mm});
            skLineSegment(sketch, "E2.5.13.1", {"start": v(112.17, 285.3) * mm, "end": v(131.42, 285.3) * mm});
            skLineSegment(sketch, "E2.5.13.2", {"start": v(112.17, 304.55) * mm, "end": v(112.17, 285.3) * mm});
            skLineSegment(sketch, "E2.5.13.3", {"start": v(131.42, 304.55) * mm, "end": v(131.42, 285.3) * mm});
            skLineSegment(sketch, "E2.5.14.0", {"start": v(112.17, 326.19) * mm, "end": v(131.42, 326.19) * mm});
            skLineSegment(sketch, "E2.5.14.1", {"start": v(112.17, 306.93) * mm, "end": v(131.42, 306.93) * mm});
            skLineSegment(sketch, "E2.5.14.2", {"start": v(112.17, 326.19) * mm, "end": v(112.17, 306.93) * mm});
            skLineSegment(sketch, "E2.5.14.3", {"start": v(131.42, 326.19) * mm, "end": v(131.42, 306.93) * mm});
            skLineSegment(sketch, "E2.5.15.0", {"start": v(112.17, 347.83) * mm, "end": v(131.42, 347.83) * mm});
            skLineSegment(sketch, "E2.5.15.1", {"start": v(112.17, 328.57) * mm, "end": v(131.42, 328.57) * mm});
            skLineSegment(sketch, "E2.5.15.2", {"start": v(112.17, 347.83) * mm, "end": v(112.17, 328.57) * mm});
            skLineSegment(sketch, "E2.5.15.3", {"start": v(131.42, 347.83) * mm, "end": v(131.42, 328.57) * mm});
            skLineSegment(sketch, "E2.5.16.0", {"start": v(112.17, 369.47) * mm, "end": v(131.42, 369.47) * mm});
            skLineSegment(sketch, "E2.5.16.1", {"start": v(112.17, 350.22) * mm, "end": v(131.42, 350.22) * mm});
            skLineSegment(sketch, "E2.5.16.2", {"start": v(112.17, 369.47) * mm, "end": v(112.17, 350.22) * mm});
            skLineSegment(sketch, "E2.5.16.3", {"start": v(131.42, 369.47) * mm, "end": v(131.42, 350.22) * mm});
            skLineSegment(sketch, "E2.5.17.0", {"start": v(112.17, 391.1) * mm, "end": v(131.42, 391.1) * mm});
            skLineSegment(sketch, "E2.5.17.1", {"start": v(112.17, 371.86) * mm, "end": v(131.42, 371.86) * mm});
            skLineSegment(sketch, "E2.5.17.2", {"start": v(112.17, 391.1) * mm, "end": v(112.17, 371.86) * mm});
            skLineSegment(sketch, "E2.5.17.3", {"start": v(131.42, 391.1) * mm, "end": v(131.42, 371.86) * mm});
            skLineSegment(sketch, "E2.5.18.0", {"start": v(112.17, 412.75) * mm, "end": v(131.42, 412.75) * mm});
            skLineSegment(sketch, "E2.5.18.1", {"start": v(112.17, 393.5) * mm, "end": v(131.42, 393.5) * mm});
            skLineSegment(sketch, "E2.5.18.2", {"start": v(112.17, 412.75) * mm, "end": v(112.17, 393.5) * mm});
            skLineSegment(sketch, "E2.5.18.3", {"start": v(131.42, 412.75) * mm, "end": v(131.42, 393.5) * mm});
            skLineSegment(sketch, "E2.5.19.0", {"start": v(112.17, 434.4) * mm, "end": v(131.42, 434.4) * mm});
            skLineSegment(sketch, "E2.5.19.1", {"start": v(112.17, 415.14) * mm, "end": v(131.42, 415.14) * mm});
            skLineSegment(sketch, "E2.5.19.2", {"start": v(112.17, 434.4) * mm, "end": v(112.17, 415.14) * mm});
            skLineSegment(sketch, "E2.5.19.3", {"start": v(131.42, 434.4) * mm, "end": v(131.42, 415.14) * mm});
            skLineSegment(sketch, "E2.5.20.0", {"start": v(112.17, 456.03) * mm, "end": v(131.42, 456.03) * mm});
            skLineSegment(sketch, "E2.5.20.1", {"start": v(112.17, 436.78) * mm, "end": v(131.42, 436.78) * mm});
            skLineSegment(sketch, "E2.5.20.2", {"start": v(112.17, 456.03) * mm, "end": v(112.17, 436.78) * mm});
            skLineSegment(sketch, "E2.5.20.3", {"start": v(131.42, 456.03) * mm, "end": v(131.42, 436.78) * mm});
            skLineSegment(sketch, "E2.5.21.0", {"start": v(112.17, 477.67) * mm, "end": v(131.42, 477.67) * mm});
            skLineSegment(sketch, "E2.5.21.1", {"start": v(112.17, 458.42) * mm, "end": v(131.42, 458.42) * mm});
            skLineSegment(sketch, "E2.5.21.2", {"start": v(112.17, 477.67) * mm, "end": v(112.17, 458.42) * mm});
            skLineSegment(sketch, "E2.5.21.3", {"start": v(131.42, 477.67) * mm, "end": v(131.42, 458.42) * mm});
            skLineSegment(sketch, "E2.5.22.0", {"start": v(112.17, 499.31) * mm, "end": v(131.42, 499.31) * mm});
            skLineSegment(sketch, "E2.5.22.1", {"start": v(112.17, 480.06) * mm, "end": v(131.42, 480.06) * mm});
            skLineSegment(sketch, "E2.5.22.2", {"start": v(112.17, 499.31) * mm, "end": v(112.17, 480.06) * mm});
            skLineSegment(sketch, "E2.5.22.3", {"start": v(131.42, 499.31) * mm, "end": v(131.42, 480.06) * mm});
            skLineSegment(sketch, "E2.5.23.0", {"start": v(112.17, 520.95) * mm, "end": v(131.42, 520.95) * mm});
            skLineSegment(sketch, "E2.5.23.1", {"start": v(112.17, 501.7) * mm, "end": v(131.42, 501.7) * mm});
            skLineSegment(sketch, "E2.5.23.2", {"start": v(112.17, 520.95) * mm, "end": v(112.17, 501.7) * mm});
            skLineSegment(sketch, "E2.5.23.3", {"start": v(131.42, 520.95) * mm, "end": v(131.42, 501.7) * mm});
            skLineSegment(sketch, "E2.6.0.0", {"start": v(133.8, 23.22) * mm, "end": v(153.06, 23.22) * mm});
            skLineSegment(sketch, "E2.6.0.1", {"start": v(133.8, 3.96) * mm, "end": v(153.06, 3.96) * mm});
            skLineSegment(sketch, "E2.6.0.2", {"start": v(133.8, 23.22) * mm, "end": v(133.8, 3.96) * mm});
            skLineSegment(sketch, "E2.6.0.3", {"start": v(153.06, 23.22) * mm, "end": v(153.06, 3.96) * mm});
            skLineSegment(sketch, "E2.6.1.0", {"start": v(133.8, 44.86) * mm, "end": v(153.06, 44.86) * mm});
            skLineSegment(sketch, "E2.6.1.1", {"start": v(133.8, 25.6) * mm, "end": v(153.06, 25.6) * mm});
            skLineSegment(sketch, "E2.6.1.2", {"start": v(133.8, 44.86) * mm, "end": v(133.8, 25.6) * mm});
            skLineSegment(sketch, "E2.6.1.3", {"start": v(153.06, 44.86) * mm, "end": v(153.06, 25.6) * mm});
            skLineSegment(sketch, "E2.6.2.0", {"start": v(133.8, 66.5) * mm, "end": v(153.06, 66.5) * mm});
            skLineSegment(sketch, "E2.6.2.1", {"start": v(133.8, 47.24) * mm, "end": v(153.06, 47.24) * mm});
            skLineSegment(sketch, "E2.6.2.2", {"start": v(133.8, 66.5) * mm, "end": v(133.8, 47.24) * mm});
            skLineSegment(sketch, "E2.6.2.3", {"start": v(153.06, 66.5) * mm, "end": v(153.06, 47.24) * mm});
            skLineSegment(sketch, "E2.6.3.0", {"start": v(133.8, 88.14) * mm, "end": v(153.06, 88.14) * mm});
            skLineSegment(sketch, "E2.6.3.1", {"start": v(133.8, 68.88) * mm, "end": v(153.06, 68.88) * mm});
            skLineSegment(sketch, "E2.6.3.2", {"start": v(133.8, 88.14) * mm, "end": v(133.8, 68.88) * mm});
            skLineSegment(sketch, "E2.6.3.3", {"start": v(153.06, 88.14) * mm, "end": v(153.06, 68.88) * mm});
            skLineSegment(sketch, "E2.6.4.0", {"start": v(133.8, 109.78) * mm, "end": v(153.06, 109.78) * mm});
            skLineSegment(sketch, "E2.6.4.1", {"start": v(133.8, 90.53) * mm, "end": v(153.06, 90.53) * mm});
            skLineSegment(sketch, "E2.6.4.2", {"start": v(133.8, 109.78) * mm, "end": v(133.8, 90.53) * mm});
            skLineSegment(sketch, "E2.6.4.3", {"start": v(153.06, 109.78) * mm, "end": v(153.06, 90.53) * mm});
            skLineSegment(sketch, "E2.6.5.0", {"start": v(133.8, 131.42) * mm, "end": v(153.06, 131.42) * mm});
            skLineSegment(sketch, "E2.6.5.1", {"start": v(133.8, 112.17) * mm, "end": v(153.06, 112.17) * mm});
            skLineSegment(sketch, "E2.6.5.2", {"start": v(133.8, 131.42) * mm, "end": v(133.8, 112.17) * mm});
            skLineSegment(sketch, "E2.6.5.3", {"start": v(153.06, 131.42) * mm, "end": v(153.06, 112.17) * mm});
            skLineSegment(sketch, "E2.6.6.0", {"start": v(133.8, 153.06) * mm, "end": v(153.06, 153.06) * mm});
            skLineSegment(sketch, "E2.6.6.1", {"start": v(133.8, 133.8) * mm, "end": v(153.06, 133.8) * mm});
            skLineSegment(sketch, "E2.6.6.2", {"start": v(133.8, 153.06) * mm, "end": v(133.8, 133.8) * mm});
            skLineSegment(sketch, "E2.6.6.3", {"start": v(153.06, 153.06) * mm, "end": v(153.06, 133.8) * mm});
            skLineSegment(sketch, "E2.6.7.0", {"start": v(133.8, 174.7) * mm, "end": v(153.06, 174.7) * mm});
            skLineSegment(sketch, "E2.6.7.1", {"start": v(133.8, 155.45) * mm, "end": v(153.06, 155.45) * mm});
            skLineSegment(sketch, "E2.6.7.2", {"start": v(133.8, 174.7) * mm, "end": v(133.8, 155.45) * mm});
            skLineSegment(sketch, "E2.6.7.3", {"start": v(153.06, 174.7) * mm, "end": v(153.06, 155.45) * mm});
            skLineSegment(sketch, "E2.6.8.0", {"start": v(133.8, 196.34) * mm, "end": v(153.06, 196.34) * mm});
            skLineSegment(sketch, "E2.6.8.1", {"start": v(133.8, 177.09) * mm, "end": v(153.06, 177.09) * mm});
            skLineSegment(sketch, "E2.6.8.2", {"start": v(133.8, 196.34) * mm, "end": v(133.8, 177.09) * mm});
            skLineSegment(sketch, "E2.6.8.3", {"start": v(153.06, 196.34) * mm, "end": v(153.06, 177.09) * mm});
            skLineSegment(sketch, "E2.6.9.0", {"start": v(133.8, 217.98) * mm, "end": v(153.06, 217.98) * mm});
            skLineSegment(sketch, "E2.6.9.1", {"start": v(133.8, 198.73) * mm, "end": v(153.06, 198.73) * mm});
            skLineSegment(sketch, "E2.6.9.2", {"start": v(133.8, 217.98) * mm, "end": v(133.8, 198.73) * mm});
            skLineSegment(sketch, "E2.6.9.3", {"start": v(153.06, 217.98) * mm, "end": v(153.06, 198.73) * mm});
            skLineSegment(sketch, "E2.6.10.0", {"start": v(133.8, 239.62) * mm, "end": v(153.06, 239.62) * mm});
            skLineSegment(sketch, "E2.6.10.1", {"start": v(133.8, 220.37) * mm, "end": v(153.06, 220.37) * mm});
            skLineSegment(sketch, "E2.6.10.2", {"start": v(133.8, 239.62) * mm, "end": v(133.8, 220.37) * mm});
            skLineSegment(sketch, "E2.6.10.3", {"start": v(153.06, 239.62) * mm, "end": v(153.06, 220.37) * mm});
            skLineSegment(sketch, "E2.6.11.0", {"start": v(133.8, 261.26) * mm, "end": v(153.06, 261.26) * mm});
            skLineSegment(sketch, "E2.6.11.1", {"start": v(133.8, 242.01) * mm, "end": v(153.06, 242.01) * mm});
            skLineSegment(sketch, "E2.6.11.2", {"start": v(133.8, 261.26) * mm, "end": v(133.8, 242.01) * mm});
            skLineSegment(sketch, "E2.6.11.3", {"start": v(153.06, 261.26) * mm, "end": v(153.06, 242.01) * mm});
            skLineSegment(sketch, "E2.6.12.0", {"start": v(133.8, 282.9) * mm, "end": v(153.06, 282.9) * mm});
            skLineSegment(sketch, "E2.6.12.1", {"start": v(133.8, 263.65) * mm, "end": v(153.06, 263.65) * mm});
            skLineSegment(sketch, "E2.6.12.2", {"start": v(133.8, 282.9) * mm, "end": v(133.8, 263.65) * mm});
            skLineSegment(sketch, "E2.6.12.3", {"start": v(153.06, 282.9) * mm, "end": v(153.06, 263.65) * mm});
            skLineSegment(sketch, "E2.6.13.0", {"start": v(133.8, 304.55) * mm, "end": v(153.06, 304.55) * mm});
            skLineSegment(sketch, "E2.6.13.1", {"start": v(133.8, 285.3) * mm, "end": v(153.06, 285.3) * mm});
            skLineSegment(sketch, "E2.6.13.2", {"start": v(133.8, 304.55) * mm, "end": v(133.8, 285.3) * mm});
            skLineSegment(sketch, "E2.6.13.3", {"start": v(153.06, 304.55) * mm, "end": v(153.06, 285.3) * mm});
            skLineSegment(sketch, "E2.6.14.0", {"start": v(133.8, 326.19) * mm, "end": v(153.06, 326.19) * mm});
            skLineSegment(sketch, "E2.6.14.1", {"start": v(133.8, 306.93) * mm, "end": v(153.06, 306.93) * mm});
            skLineSegment(sketch, "E2.6.14.2", {"start": v(133.8, 326.19) * mm, "end": v(133.8, 306.93) * mm});
            skLineSegment(sketch, "E2.6.14.3", {"start": v(153.06, 326.19) * mm, "end": v(153.06, 306.93) * mm});
            skLineSegment(sketch, "E2.6.15.0", {"start": v(133.8, 347.83) * mm, "end": v(153.06, 347.83) * mm});
            skLineSegment(sketch, "E2.6.15.1", {"start": v(133.8, 328.57) * mm, "end": v(153.06, 328.57) * mm});
            skLineSegment(sketch, "E2.6.15.2", {"start": v(133.8, 347.83) * mm, "end": v(133.8, 328.57) * mm});
            skLineSegment(sketch, "E2.6.15.3", {"start": v(153.06, 347.83) * mm, "end": v(153.06, 328.57) * mm});
            skLineSegment(sketch, "E2.6.16.0", {"start": v(133.8, 369.47) * mm, "end": v(153.06, 369.47) * mm});
            skLineSegment(sketch, "E2.6.16.1", {"start": v(133.8, 350.22) * mm, "end": v(153.06, 350.22) * mm});
            skLineSegment(sketch, "E2.6.16.2", {"start": v(133.8, 369.47) * mm, "end": v(133.8, 350.22) * mm});
            skLineSegment(sketch, "E2.6.16.3", {"start": v(153.06, 369.47) * mm, "end": v(153.06, 350.22) * mm});
            skLineSegment(sketch, "E2.6.17.0", {"start": v(133.8, 391.1) * mm, "end": v(153.06, 391.1) * mm});
            skLineSegment(sketch, "E2.6.17.1", {"start": v(133.8, 371.86) * mm, "end": v(153.06, 371.86) * mm});
            skLineSegment(sketch, "E2.6.17.2", {"start": v(133.8, 391.1) * mm, "end": v(133.8, 371.86) * mm});
            skLineSegment(sketch, "E2.6.17.3", {"start": v(153.06, 391.1) * mm, "end": v(153.06, 371.86) * mm});
            skLineSegment(sketch, "E2.6.18.0", {"start": v(133.8, 412.75) * mm, "end": v(153.06, 412.75) * mm});
            skLineSegment(sketch, "E2.6.18.1", {"start": v(133.8, 393.5) * mm, "end": v(153.06, 393.5) * mm});
            skLineSegment(sketch, "E2.6.18.2", {"start": v(133.8, 412.75) * mm, "end": v(133.8, 393.5) * mm});
            skLineSegment(sketch, "E2.6.18.3", {"start": v(153.06, 412.75) * mm, "end": v(153.06, 393.5) * mm});
            skLineSegment(sketch, "E2.6.19.0", {"start": v(133.8, 434.4) * mm, "end": v(153.06, 434.4) * mm});
            skLineSegment(sketch, "E2.6.19.1", {"start": v(133.8, 415.14) * mm, "end": v(153.06, 415.14) * mm});
            skLineSegment(sketch, "E2.6.19.2", {"start": v(133.8, 434.4) * mm, "end": v(133.8, 415.14) * mm});
            skLineSegment(sketch, "E2.6.19.3", {"start": v(153.06, 434.4) * mm, "end": v(153.06, 415.14) * mm});
            skLineSegment(sketch, "E2.6.20.0", {"start": v(133.8, 456.03) * mm, "end": v(153.06, 456.03) * mm});
            skLineSegment(sketch, "E2.6.20.1", {"start": v(133.8, 436.78) * mm, "end": v(153.06, 436.78) * mm});
            skLineSegment(sketch, "E2.6.20.2", {"start": v(133.8, 456.03) * mm, "end": v(133.8, 436.78) * mm});
            skLineSegment(sketch, "E2.6.20.3", {"start": v(153.06, 456.03) * mm, "end": v(153.06, 436.78) * mm});
            skLineSegment(sketch, "E2.6.21.0", {"start": v(133.8, 477.67) * mm, "end": v(153.06, 477.67) * mm});
            skLineSegment(sketch, "E2.6.21.1", {"start": v(133.8, 458.42) * mm, "end": v(153.06, 458.42) * mm});
            skLineSegment(sketch, "E2.6.21.2", {"start": v(133.8, 477.67) * mm, "end": v(133.8, 458.42) * mm});
            skLineSegment(sketch, "E2.6.21.3", {"start": v(153.06, 477.67) * mm, "end": v(153.06, 458.42) * mm});
            skLineSegment(sketch, "E2.6.22.0", {"start": v(133.8, 499.31) * mm, "end": v(153.06, 499.31) * mm});
            skLineSegment(sketch, "E2.6.22.1", {"start": v(133.8, 480.06) * mm, "end": v(153.06, 480.06) * mm});
            skLineSegment(sketch, "E2.6.22.2", {"start": v(133.8, 499.31) * mm, "end": v(133.8, 480.06) * mm});
            skLineSegment(sketch, "E2.6.22.3", {"start": v(153.06, 499.31) * mm, "end": v(153.06, 480.06) * mm});
            skLineSegment(sketch, "E2.6.23.0", {"start": v(133.8, 520.95) * mm, "end": v(153.06, 520.95) * mm});
            skLineSegment(sketch, "E2.6.23.1", {"start": v(133.8, 501.7) * mm, "end": v(153.06, 501.7) * mm});
            skLineSegment(sketch, "E2.6.23.2", {"start": v(133.8, 520.95) * mm, "end": v(133.8, 501.7) * mm});
            skLineSegment(sketch, "E2.6.23.3", {"start": v(153.06, 520.95) * mm, "end": v(153.06, 501.7) * mm});
            skLineSegment(sketch, "E2.7.0.0", {"start": v(155.45, 23.22) * mm, "end": v(174.7, 23.22) * mm});
            skLineSegment(sketch, "E2.7.0.1", {"start": v(155.45, 3.96) * mm, "end": v(174.7, 3.96) * mm});
            skLineSegment(sketch, "E2.7.0.2", {"start": v(155.45, 23.22) * mm, "end": v(155.45, 3.96) * mm});
            skLineSegment(sketch, "E2.7.0.3", {"start": v(174.7, 23.22) * mm, "end": v(174.7, 3.96) * mm});
            skLineSegment(sketch, "E2.7.1.0", {"start": v(155.45, 44.86) * mm, "end": v(174.7, 44.86) * mm});
            skLineSegment(sketch, "E2.7.1.1", {"start": v(155.45, 25.6) * mm, "end": v(174.7, 25.6) * mm});
            skLineSegment(sketch, "E2.7.1.2", {"start": v(155.45, 44.86) * mm, "end": v(155.45, 25.6) * mm});
            skLineSegment(sketch, "E2.7.1.3", {"start": v(174.7, 44.86) * mm, "end": v(174.7, 25.6) * mm});
            skLineSegment(sketch, "E2.7.2.0", {"start": v(155.45, 66.5) * mm, "end": v(174.7, 66.5) * mm});
            skLineSegment(sketch, "E2.7.2.1", {"start": v(155.45, 47.24) * mm, "end": v(174.7, 47.24) * mm});
            skLineSegment(sketch, "E2.7.2.2", {"start": v(155.45, 66.5) * mm, "end": v(155.45, 47.24) * mm});
            skLineSegment(sketch, "E2.7.2.3", {"start": v(174.7, 66.5) * mm, "end": v(174.7, 47.24) * mm});
            skLineSegment(sketch, "E2.7.3.0", {"start": v(155.45, 88.14) * mm, "end": v(174.7, 88.14) * mm});
            skLineSegment(sketch, "E2.7.3.1", {"start": v(155.45, 68.88) * mm, "end": v(174.7, 68.88) * mm});
            skLineSegment(sketch, "E2.7.3.2", {"start": v(155.45, 88.14) * mm, "end": v(155.45, 68.88) * mm});
            skLineSegment(sketch, "E2.7.3.3", {"start": v(174.7, 88.14) * mm, "end": v(174.7, 68.88) * mm});
            skLineSegment(sketch, "E2.7.4.0", {"start": v(155.45, 109.78) * mm, "end": v(174.7, 109.78) * mm});
            skLineSegment(sketch, "E2.7.4.1", {"start": v(155.45, 90.53) * mm, "end": v(174.7, 90.53) * mm});
            skLineSegment(sketch, "E2.7.4.2", {"start": v(155.45, 109.78) * mm, "end": v(155.45, 90.53) * mm});
            skLineSegment(sketch, "E2.7.4.3", {"start": v(174.7, 109.78) * mm, "end": v(174.7, 90.53) * mm});
            skLineSegment(sketch, "E2.7.5.0", {"start": v(155.45, 131.42) * mm, "end": v(174.7, 131.42) * mm});
            skLineSegment(sketch, "E2.7.5.1", {"start": v(155.45, 112.17) * mm, "end": v(174.7, 112.17) * mm});
            skLineSegment(sketch, "E2.7.5.2", {"start": v(155.45, 131.42) * mm, "end": v(155.45, 112.17) * mm});
            skLineSegment(sketch, "E2.7.5.3", {"start": v(174.7, 131.42) * mm, "end": v(174.7, 112.17) * mm});
            skLineSegment(sketch, "E2.7.6.0", {"start": v(155.45, 153.06) * mm, "end": v(174.7, 153.06) * mm});
            skLineSegment(sketch, "E2.7.6.1", {"start": v(155.45, 133.8) * mm, "end": v(174.7, 133.8) * mm});
            skLineSegment(sketch, "E2.7.6.2", {"start": v(155.45, 153.06) * mm, "end": v(155.45, 133.8) * mm});
            skLineSegment(sketch, "E2.7.6.3", {"start": v(174.7, 153.06) * mm, "end": v(174.7, 133.8) * mm});
            skLineSegment(sketch, "E2.7.7.0", {"start": v(155.45, 174.7) * mm, "end": v(174.7, 174.7) * mm});
            skLineSegment(sketch, "E2.7.7.1", {"start": v(155.45, 155.45) * mm, "end": v(174.7, 155.45) * mm});
            skLineSegment(sketch, "E2.7.7.2", {"start": v(155.45, 174.7) * mm, "end": v(155.45, 155.45) * mm});
            skLineSegment(sketch, "E2.7.7.3", {"start": v(174.7, 174.7) * mm, "end": v(174.7, 155.45) * mm});
            skLineSegment(sketch, "E2.7.8.0", {"start": v(155.45, 196.34) * mm, "end": v(174.7, 196.34) * mm});
            skLineSegment(sketch, "E2.7.8.1", {"start": v(155.45, 177.09) * mm, "end": v(174.7, 177.09) * mm});
            skLineSegment(sketch, "E2.7.8.2", {"start": v(155.45, 196.34) * mm, "end": v(155.45, 177.09) * mm});
            skLineSegment(sketch, "E2.7.8.3", {"start": v(174.7, 196.34) * mm, "end": v(174.7, 177.09) * mm});
            skLineSegment(sketch, "E2.7.9.0", {"start": v(155.45, 217.98) * mm, "end": v(174.7, 217.98) * mm});
            skLineSegment(sketch, "E2.7.9.1", {"start": v(155.45, 198.73) * mm, "end": v(174.7, 198.73) * mm});
            skLineSegment(sketch, "E2.7.9.2", {"start": v(155.45, 217.98) * mm, "end": v(155.45, 198.73) * mm});
            skLineSegment(sketch, "E2.7.9.3", {"start": v(174.7, 217.98) * mm, "end": v(174.7, 198.73) * mm});
            skLineSegment(sketch, "E2.7.10.0", {"start": v(155.45, 239.62) * mm, "end": v(174.7, 239.62) * mm});
            skLineSegment(sketch, "E2.7.10.1", {"start": v(155.45, 220.37) * mm, "end": v(174.7, 220.37) * mm});
            skLineSegment(sketch, "E2.7.10.2", {"start": v(155.45, 239.62) * mm, "end": v(155.45, 220.37) * mm});
            skLineSegment(sketch, "E2.7.10.3", {"start": v(174.7, 239.62) * mm, "end": v(174.7, 220.37) * mm});
            skLineSegment(sketch, "E2.7.11.0", {"start": v(155.45, 261.26) * mm, "end": v(174.7, 261.26) * mm});
            skLineSegment(sketch, "E2.7.11.1", {"start": v(155.45, 242.01) * mm, "end": v(174.7, 242.01) * mm});
            skLineSegment(sketch, "E2.7.11.2", {"start": v(155.45, 261.26) * mm, "end": v(155.45, 242.01) * mm});
            skLineSegment(sketch, "E2.7.11.3", {"start": v(174.7, 261.26) * mm, "end": v(174.7, 242.01) * mm});
            skLineSegment(sketch, "E2.7.12.0", {"start": v(155.45, 282.9) * mm, "end": v(174.7, 282.9) * mm});
            skLineSegment(sketch, "E2.7.12.1", {"start": v(155.45, 263.65) * mm, "end": v(174.7, 263.65) * mm});
            skLineSegment(sketch, "E2.7.12.2", {"start": v(155.45, 282.9) * mm, "end": v(155.45, 263.65) * mm});
            skLineSegment(sketch, "E2.7.12.3", {"start": v(174.7, 282.9) * mm, "end": v(174.7, 263.65) * mm});
            skLineSegment(sketch, "E2.7.13.0", {"start": v(155.45, 304.55) * mm, "end": v(174.7, 304.55) * mm});
            skLineSegment(sketch, "E2.7.13.1", {"start": v(155.45, 285.3) * mm, "end": v(174.7, 285.3) * mm});
            skLineSegment(sketch, "E2.7.13.2", {"start": v(155.45, 304.55) * mm, "end": v(155.45, 285.3) * mm});
            skLineSegment(sketch, "E2.7.13.3", {"start": v(174.7, 304.55) * mm, "end": v(174.7, 285.3) * mm});
            skLineSegment(sketch, "E2.7.14.0", {"start": v(155.45, 326.19) * mm, "end": v(174.7, 326.19) * mm});
            skLineSegment(sketch, "E2.7.14.1", {"start": v(155.45, 306.93) * mm, "end": v(174.7, 306.93) * mm});
            skLineSegment(sketch, "E2.7.14.2", {"start": v(155.45, 326.19) * mm, "end": v(155.45, 306.93) * mm});
            skLineSegment(sketch, "E2.7.14.3", {"start": v(174.7, 326.19) * mm, "end": v(174.7, 306.93) * mm});
            skLineSegment(sketch, "E2.7.15.0", {"start": v(155.45, 347.83) * mm, "end": v(174.7, 347.83) * mm});
            skLineSegment(sketch, "E2.7.15.1", {"start": v(155.45, 328.57) * mm, "end": v(174.7, 328.57) * mm});
            skLineSegment(sketch, "E2.7.15.2", {"start": v(155.45, 347.83) * mm, "end": v(155.45, 328.57) * mm});
            skLineSegment(sketch, "E2.7.15.3", {"start": v(174.7, 347.83) * mm, "end": v(174.7, 328.57) * mm});
            skLineSegment(sketch, "E2.7.16.0", {"start": v(155.45, 369.47) * mm, "end": v(174.7, 369.47) * mm});
            skLineSegment(sketch, "E2.7.16.1", {"start": v(155.45, 350.22) * mm, "end": v(174.7, 350.22) * mm});
            skLineSegment(sketch, "E2.7.16.2", {"start": v(155.45, 369.47) * mm, "end": v(155.45, 350.22) * mm});
            skLineSegment(sketch, "E2.7.16.3", {"start": v(174.7, 369.47) * mm, "end": v(174.7, 350.22) * mm});
            skLineSegment(sketch, "E2.7.17.0", {"start": v(155.45, 391.1) * mm, "end": v(174.7, 391.1) * mm});
            skLineSegment(sketch, "E2.7.17.1", {"start": v(155.45, 371.86) * mm, "end": v(174.7, 371.86) * mm});
            skLineSegment(sketch, "E2.7.17.2", {"start": v(155.45, 391.1) * mm, "end": v(155.45, 371.86) * mm});
            skLineSegment(sketch, "E2.7.17.3", {"start": v(174.7, 391.1) * mm, "end": v(174.7, 371.86) * mm});
            skLineSegment(sketch, "E2.7.18.0", {"start": v(155.45, 412.75) * mm, "end": v(174.7, 412.75) * mm});
            skLineSegment(sketch, "E2.7.18.1", {"start": v(155.45, 393.5) * mm, "end": v(174.7, 393.5) * mm});
            skLineSegment(sketch, "E2.7.18.2", {"start": v(155.45, 412.75) * mm, "end": v(155.45, 393.5) * mm});
            skLineSegment(sketch, "E2.7.18.3", {"start": v(174.7, 412.75) * mm, "end": v(174.7, 393.5) * mm});
            skLineSegment(sketch, "E2.7.19.0", {"start": v(155.45, 434.4) * mm, "end": v(174.7, 434.4) * mm});
            skLineSegment(sketch, "E2.7.19.1", {"start": v(155.45, 415.14) * mm, "end": v(174.7, 415.14) * mm});
            skLineSegment(sketch, "E2.7.19.2", {"start": v(155.45, 434.4) * mm, "end": v(155.45, 415.14) * mm});
            skLineSegment(sketch, "E2.7.19.3", {"start": v(174.7, 434.4) * mm, "end": v(174.7, 415.14) * mm});
            skLineSegment(sketch, "E2.7.20.0", {"start": v(155.45, 456.03) * mm, "end": v(174.7, 456.03) * mm});
            skLineSegment(sketch, "E2.7.20.1", {"start": v(155.45, 436.78) * mm, "end": v(174.7, 436.78) * mm});
            skLineSegment(sketch, "E2.7.20.2", {"start": v(155.45, 456.03) * mm, "end": v(155.45, 436.78) * mm});
            skLineSegment(sketch, "E2.7.20.3", {"start": v(174.7, 456.03) * mm, "end": v(174.7, 436.78) * mm});
            skLineSegment(sketch, "E2.7.21.0", {"start": v(155.45, 477.67) * mm, "end": v(174.7, 477.67) * mm});
            skLineSegment(sketch, "E2.7.21.1", {"start": v(155.45, 458.42) * mm, "end": v(174.7, 458.42) * mm});
            skLineSegment(sketch, "E2.7.21.2", {"start": v(155.45, 477.67) * mm, "end": v(155.45, 458.42) * mm});
            skLineSegment(sketch, "E2.7.21.3", {"start": v(174.7, 477.67) * mm, "end": v(174.7, 458.42) * mm});
            skLineSegment(sketch, "E2.7.22.0", {"start": v(155.45, 499.31) * mm, "end": v(174.7, 499.31) * mm});
            skLineSegment(sketch, "E2.7.22.1", {"start": v(155.45, 480.06) * mm, "end": v(174.7, 480.06) * mm});
            skLineSegment(sketch, "E2.7.22.2", {"start": v(155.45, 499.31) * mm, "end": v(155.45, 480.06) * mm});
            skLineSegment(sketch, "E2.7.22.3", {"start": v(174.7, 499.31) * mm, "end": v(174.7, 480.06) * mm});
            skLineSegment(sketch, "E2.7.23.0", {"start": v(155.45, 520.95) * mm, "end": v(174.7, 520.95) * mm});
            skLineSegment(sketch, "E2.7.23.1", {"start": v(155.45, 501.7) * mm, "end": v(174.7, 501.7) * mm});
            skLineSegment(sketch, "E2.7.23.2", {"start": v(155.45, 520.95) * mm, "end": v(155.45, 501.7) * mm});
            skLineSegment(sketch, "E2.7.23.3", {"start": v(174.7, 520.95) * mm, "end": v(174.7, 501.7) * mm});
            skLineSegment(sketch, "E2.8.0.0", {"start": v(177.09, 23.22) * mm, "end": v(196.34, 23.22) * mm});
            skLineSegment(sketch, "E2.8.0.1", {"start": v(177.09, 3.96) * mm, "end": v(196.34, 3.96) * mm});
            skLineSegment(sketch, "E2.8.0.2", {"start": v(177.09, 23.22) * mm, "end": v(177.09, 3.96) * mm});
            skLineSegment(sketch, "E2.8.0.3", {"start": v(196.34, 23.22) * mm, "end": v(196.34, 3.96) * mm});
            skLineSegment(sketch, "E2.8.1.0", {"start": v(177.09, 44.86) * mm, "end": v(196.34, 44.86) * mm});
            skLineSegment(sketch, "E2.8.1.1", {"start": v(177.09, 25.6) * mm, "end": v(196.34, 25.6) * mm});
            skLineSegment(sketch, "E2.8.1.2", {"start": v(177.09, 44.86) * mm, "end": v(177.09, 25.6) * mm});
            skLineSegment(sketch, "E2.8.1.3", {"start": v(196.34, 44.86) * mm, "end": v(196.34, 25.6) * mm});
            skLineSegment(sketch, "E2.8.2.0", {"start": v(177.09, 66.5) * mm, "end": v(196.34, 66.5) * mm});
            skLineSegment(sketch, "E2.8.2.1", {"start": v(177.09, 47.24) * mm, "end": v(196.34, 47.24) * mm});
            skLineSegment(sketch, "E2.8.2.2", {"start": v(177.09, 66.5) * mm, "end": v(177.09, 47.24) * mm});
            skLineSegment(sketch, "E2.8.2.3", {"start": v(196.34, 66.5) * mm, "end": v(196.34, 47.24) * mm});
            skLineSegment(sketch, "E2.8.3.0", {"start": v(177.09, 88.14) * mm, "end": v(196.34, 88.14) * mm});
            skLineSegment(sketch, "E2.8.3.1", {"start": v(177.09, 68.88) * mm, "end": v(196.34, 68.88) * mm});
            skLineSegment(sketch, "E2.8.3.2", {"start": v(177.09, 88.14) * mm, "end": v(177.09, 68.88) * mm});
            skLineSegment(sketch, "E2.8.3.3", {"start": v(196.34, 88.14) * mm, "end": v(196.34, 68.88) * mm});
            skLineSegment(sketch, "E2.8.4.0", {"start": v(177.09, 109.78) * mm, "end": v(196.34, 109.78) * mm});
            skLineSegment(sketch, "E2.8.4.1", {"start": v(177.09, 90.53) * mm, "end": v(196.34, 90.53) * mm});
            skLineSegment(sketch, "E2.8.4.2", {"start": v(177.09, 109.78) * mm, "end": v(177.09, 90.53) * mm});
            skLineSegment(sketch, "E2.8.4.3", {"start": v(196.34, 109.78) * mm, "end": v(196.34, 90.53) * mm});
            skLineSegment(sketch, "E2.8.5.0", {"start": v(177.09, 131.42) * mm, "end": v(196.34, 131.42) * mm});
            skLineSegment(sketch, "E2.8.5.1", {"start": v(177.09, 112.17) * mm, "end": v(196.34, 112.17) * mm});
            skLineSegment(sketch, "E2.8.5.2", {"start": v(177.09, 131.42) * mm, "end": v(177.09, 112.17) * mm});
            skLineSegment(sketch, "E2.8.5.3", {"start": v(196.34, 131.42) * mm, "end": v(196.34, 112.17) * mm});
            skLineSegment(sketch, "E2.8.6.0", {"start": v(177.09, 153.06) * mm, "end": v(196.34, 153.06) * mm});
            skLineSegment(sketch, "E2.8.6.1", {"start": v(177.09, 133.8) * mm, "end": v(196.34, 133.8) * mm});
            skLineSegment(sketch, "E2.8.6.2", {"start": v(177.09, 153.06) * mm, "end": v(177.09, 133.8) * mm});
            skLineSegment(sketch, "E2.8.6.3", {"start": v(196.34, 153.06) * mm, "end": v(196.34, 133.8) * mm});
            skLineSegment(sketch, "E2.8.7.0", {"start": v(177.09, 174.7) * mm, "end": v(196.34, 174.7) * mm});
            skLineSegment(sketch, "E2.8.7.1", {"start": v(177.09, 155.45) * mm, "end": v(196.34, 155.45) * mm});
            skLineSegment(sketch, "E2.8.7.2", {"start": v(177.09, 174.7) * mm, "end": v(177.09, 155.45) * mm});
            skLineSegment(sketch, "E2.8.7.3", {"start": v(196.34, 174.7) * mm, "end": v(196.34, 155.45) * mm});
            skLineSegment(sketch, "E2.8.8.0", {"start": v(177.09, 196.34) * mm, "end": v(196.34, 196.34) * mm});
            skLineSegment(sketch, "E2.8.8.1", {"start": v(177.09, 177.09) * mm, "end": v(196.34, 177.09) * mm});
            skLineSegment(sketch, "E2.8.8.2", {"start": v(177.09, 196.34) * mm, "end": v(177.09, 177.09) * mm});
            skLineSegment(sketch, "E2.8.8.3", {"start": v(196.34, 196.34) * mm, "end": v(196.34, 177.09) * mm});
            skLineSegment(sketch, "E2.8.9.0", {"start": v(177.09, 217.98) * mm, "end": v(196.34, 217.98) * mm});
            skLineSegment(sketch, "E2.8.9.1", {"start": v(177.09, 198.73) * mm, "end": v(196.34, 198.73) * mm});
            skLineSegment(sketch, "E2.8.9.2", {"start": v(177.09, 217.98) * mm, "end": v(177.09, 198.73) * mm});
            skLineSegment(sketch, "E2.8.9.3", {"start": v(196.34, 217.98) * mm, "end": v(196.34, 198.73) * mm});
            skLineSegment(sketch, "E2.8.10.0", {"start": v(177.09, 239.62) * mm, "end": v(196.34, 239.62) * mm});
            skLineSegment(sketch, "E2.8.10.1", {"start": v(177.09, 220.37) * mm, "end": v(196.34, 220.37) * mm});
            skLineSegment(sketch, "E2.8.10.2", {"start": v(177.09, 239.62) * mm, "end": v(177.09, 220.37) * mm});
            skLineSegment(sketch, "E2.8.10.3", {"start": v(196.34, 239.62) * mm, "end": v(196.34, 220.37) * mm});
            skLineSegment(sketch, "E2.8.11.0", {"start": v(177.09, 261.26) * mm, "end": v(196.34, 261.26) * mm});
            skLineSegment(sketch, "E2.8.11.1", {"start": v(177.09, 242.01) * mm, "end": v(196.34, 242.01) * mm});
            skLineSegment(sketch, "E2.8.11.2", {"start": v(177.09, 261.26) * mm, "end": v(177.09, 242.01) * mm});
            skLineSegment(sketch, "E2.8.11.3", {"start": v(196.34, 261.26) * mm, "end": v(196.34, 242.01) * mm});
            skLineSegment(sketch, "E2.8.12.0", {"start": v(177.09, 282.9) * mm, "end": v(196.34, 282.9) * mm});
            skLineSegment(sketch, "E2.8.12.1", {"start": v(177.09, 263.65) * mm, "end": v(196.34, 263.65) * mm});
            skLineSegment(sketch, "E2.8.12.2", {"start": v(177.09, 282.9) * mm, "end": v(177.09, 263.65) * mm});
            skLineSegment(sketch, "E2.8.12.3", {"start": v(196.34, 282.9) * mm, "end": v(196.34, 263.65) * mm});
            skLineSegment(sketch, "E2.8.13.0", {"start": v(177.09, 304.55) * mm, "end": v(196.34, 304.55) * mm});
            skLineSegment(sketch, "E2.8.13.1", {"start": v(177.09, 285.3) * mm, "end": v(196.34, 285.3) * mm});
            skLineSegment(sketch, "E2.8.13.2", {"start": v(177.09, 304.55) * mm, "end": v(177.09, 285.3) * mm});
            skLineSegment(sketch, "E2.8.13.3", {"start": v(196.34, 304.55) * mm, "end": v(196.34, 285.3) * mm});
            skLineSegment(sketch, "E2.8.14.0", {"start": v(177.09, 326.19) * mm, "end": v(196.34, 326.19) * mm});
            skLineSegment(sketch, "E2.8.14.1", {"start": v(177.09, 306.93) * mm, "end": v(196.34, 306.93) * mm});
            skLineSegment(sketch, "E2.8.14.2", {"start": v(177.09, 326.19) * mm, "end": v(177.09, 306.93) * mm});
            skLineSegment(sketch, "E2.8.14.3", {"start": v(196.34, 326.19) * mm, "end": v(196.34, 306.93) * mm});
            skLineSegment(sketch, "E2.8.15.0", {"start": v(177.09, 347.83) * mm, "end": v(196.34, 347.83) * mm});
            skLineSegment(sketch, "E2.8.15.1", {"start": v(177.09, 328.57) * mm, "end": v(196.34, 328.57) * mm});
            skLineSegment(sketch, "E2.8.15.2", {"start": v(177.09, 347.83) * mm, "end": v(177.09, 328.57) * mm});
            skLineSegment(sketch, "E2.8.15.3", {"start": v(196.34, 347.83) * mm, "end": v(196.34, 328.57) * mm});
            skLineSegment(sketch, "E2.8.16.0", {"start": v(177.09, 369.47) * mm, "end": v(196.34, 369.47) * mm});
            skLineSegment(sketch, "E2.8.16.1", {"start": v(177.09, 350.22) * mm, "end": v(196.34, 350.22) * mm});
            skLineSegment(sketch, "E2.8.16.2", {"start": v(177.09, 369.47) * mm, "end": v(177.09, 350.22) * mm});
            skLineSegment(sketch, "E2.8.16.3", {"start": v(196.34, 369.47) * mm, "end": v(196.34, 350.22) * mm});
            skLineSegment(sketch, "E2.8.17.0", {"start": v(177.09, 391.1) * mm, "end": v(196.34, 391.1) * mm});
            skLineSegment(sketch, "E2.8.17.1", {"start": v(177.09, 371.86) * mm, "end": v(196.34, 371.86) * mm});
            skLineSegment(sketch, "E2.8.17.2", {"start": v(177.09, 391.1) * mm, "end": v(177.09, 371.86) * mm});
            skLineSegment(sketch, "E2.8.17.3", {"start": v(196.34, 391.1) * mm, "end": v(196.34, 371.86) * mm});
            skLineSegment(sketch, "E2.8.18.0", {"start": v(177.09, 412.75) * mm, "end": v(196.34, 412.75) * mm});
            skLineSegment(sketch, "E2.8.18.1", {"start": v(177.09, 393.5) * mm, "end": v(196.34, 393.5) * mm});
            skLineSegment(sketch, "E2.8.18.2", {"start": v(177.09, 412.75) * mm, "end": v(177.09, 393.5) * mm});
            skLineSegment(sketch, "E2.8.18.3", {"start": v(196.34, 412.75) * mm, "end": v(196.34, 393.5) * mm});
            skLineSegment(sketch, "E2.8.19.0", {"start": v(177.09, 434.4) * mm, "end": v(196.34, 434.4) * mm});
            skLineSegment(sketch, "E2.8.19.1", {"start": v(177.09, 415.14) * mm, "end": v(196.34, 415.14) * mm});
            skLineSegment(sketch, "E2.8.19.2", {"start": v(177.09, 434.4) * mm, "end": v(177.09, 415.14) * mm});
            skLineSegment(sketch, "E2.8.19.3", {"start": v(196.34, 434.4) * mm, "end": v(196.34, 415.14) * mm});
            skLineSegment(sketch, "E2.8.20.0", {"start": v(177.09, 456.03) * mm, "end": v(196.34, 456.03) * mm});
            skLineSegment(sketch, "E2.8.20.1", {"start": v(177.09, 436.78) * mm, "end": v(196.34, 436.78) * mm});
            skLineSegment(sketch, "E2.8.20.2", {"start": v(177.09, 456.03) * mm, "end": v(177.09, 436.78) * mm});
            skLineSegment(sketch, "E2.8.20.3", {"start": v(196.34, 456.03) * mm, "end": v(196.34, 436.78) * mm});
            skLineSegment(sketch, "E2.8.21.0", {"start": v(177.09, 477.67) * mm, "end": v(196.34, 477.67) * mm});
            skLineSegment(sketch, "E2.8.21.1", {"start": v(177.09, 458.42) * mm, "end": v(196.34, 458.42) * mm});
            skLineSegment(sketch, "E2.8.21.2", {"start": v(177.09, 477.67) * mm, "end": v(177.09, 458.42) * mm});
            skLineSegment(sketch, "E2.8.21.3", {"start": v(196.34, 477.67) * mm, "end": v(196.34, 458.42) * mm});
            skLineSegment(sketch, "E2.8.22.0", {"start": v(177.09, 499.31) * mm, "end": v(196.34, 499.31) * mm});
            skLineSegment(sketch, "E2.8.22.1", {"start": v(177.09, 480.06) * mm, "end": v(196.34, 480.06) * mm});
            skLineSegment(sketch, "E2.8.22.2", {"start": v(177.09, 499.31) * mm, "end": v(177.09, 480.06) * mm});
            skLineSegment(sketch, "E2.8.22.3", {"start": v(196.34, 499.31) * mm, "end": v(196.34, 480.06) * mm});
            skLineSegment(sketch, "E2.8.23.0", {"start": v(177.09, 520.95) * mm, "end": v(196.34, 520.95) * mm});
            skLineSegment(sketch, "E2.8.23.1", {"start": v(177.09, 501.7) * mm, "end": v(196.34, 501.7) * mm});
            skLineSegment(sketch, "E2.8.23.2", {"start": v(177.09, 520.95) * mm, "end": v(177.09, 501.7) * mm});
            skLineSegment(sketch, "E2.8.23.3", {"start": v(196.34, 520.95) * mm, "end": v(196.34, 501.7) * mm});
            skLineSegment(sketch, "E2.9.0.0", {"start": v(198.73, 23.22) * mm, "end": v(217.98, 23.22) * mm});
            skLineSegment(sketch, "E2.9.0.1", {"start": v(198.73, 3.96) * mm, "end": v(217.98, 3.96) * mm});
            skLineSegment(sketch, "E2.9.0.2", {"start": v(198.73, 23.22) * mm, "end": v(198.73, 3.96) * mm});
            skLineSegment(sketch, "E2.9.0.3", {"start": v(217.98, 23.22) * mm, "end": v(217.98, 3.96) * mm});
            skLineSegment(sketch, "E2.9.1.0", {"start": v(198.73, 44.86) * mm, "end": v(217.98, 44.86) * mm});
            skLineSegment(sketch, "E2.9.1.1", {"start": v(198.73, 25.6) * mm, "end": v(217.98, 25.6) * mm});
            skLineSegment(sketch, "E2.9.1.2", {"start": v(198.73, 44.86) * mm, "end": v(198.73, 25.6) * mm});
            skLineSegment(sketch, "E2.9.1.3", {"start": v(217.98, 44.86) * mm, "end": v(217.98, 25.6) * mm});
            skLineSegment(sketch, "E2.9.2.0", {"start": v(198.73, 66.5) * mm, "end": v(217.98, 66.5) * mm});
            skLineSegment(sketch, "E2.9.2.1", {"start": v(198.73, 47.24) * mm, "end": v(217.98, 47.24) * mm});
            skLineSegment(sketch, "E2.9.2.2", {"start": v(198.73, 66.5) * mm, "end": v(198.73, 47.24) * mm});
            skLineSegment(sketch, "E2.9.2.3", {"start": v(217.98, 66.5) * mm, "end": v(217.98, 47.24) * mm});
            skLineSegment(sketch, "E2.9.3.0", {"start": v(198.73, 88.14) * mm, "end": v(217.98, 88.14) * mm});
            skLineSegment(sketch, "E2.9.3.1", {"start": v(198.73, 68.88) * mm, "end": v(217.98, 68.88) * mm});
            skLineSegment(sketch, "E2.9.3.2", {"start": v(198.73, 88.14) * mm, "end": v(198.73, 68.88) * mm});
            skLineSegment(sketch, "E2.9.3.3", {"start": v(217.98, 88.14) * mm, "end": v(217.98, 68.88) * mm});
            skLineSegment(sketch, "E2.9.4.0", {"start": v(198.73, 109.78) * mm, "end": v(217.98, 109.78) * mm});
            skLineSegment(sketch, "E2.9.4.1", {"start": v(198.73, 90.53) * mm, "end": v(217.98, 90.53) * mm});
            skLineSegment(sketch, "E2.9.4.2", {"start": v(198.73, 109.78) * mm, "end": v(198.73, 90.53) * mm});
            skLineSegment(sketch, "E2.9.4.3", {"start": v(217.98, 109.78) * mm, "end": v(217.98, 90.53) * mm});
            skLineSegment(sketch, "E2.9.5.0", {"start": v(198.73, 131.42) * mm, "end": v(217.98, 131.42) * mm});
            skLineSegment(sketch, "E2.9.5.1", {"start": v(198.73, 112.17) * mm, "end": v(217.98, 112.17) * mm});
            skLineSegment(sketch, "E2.9.5.2", {"start": v(198.73, 131.42) * mm, "end": v(198.73, 112.17) * mm});
            skLineSegment(sketch, "E2.9.5.3", {"start": v(217.98, 131.42) * mm, "end": v(217.98, 112.17) * mm});
            skLineSegment(sketch, "E2.9.6.0", {"start": v(198.73, 153.06) * mm, "end": v(217.98, 153.06) * mm});
            skLineSegment(sketch, "E2.9.6.1", {"start": v(198.73, 133.8) * mm, "end": v(217.98, 133.8) * mm});
            skLineSegment(sketch, "E2.9.6.2", {"start": v(198.73, 153.06) * mm, "end": v(198.73, 133.8) * mm});
            skLineSegment(sketch, "E2.9.6.3", {"start": v(217.98, 153.06) * mm, "end": v(217.98, 133.8) * mm});
            skLineSegment(sketch, "E2.9.7.0", {"start": v(198.73, 174.7) * mm, "end": v(217.98, 174.7) * mm});
            skLineSegment(sketch, "E2.9.7.1", {"start": v(198.73, 155.45) * mm, "end": v(217.98, 155.45) * mm});
            skLineSegment(sketch, "E2.9.7.2", {"start": v(198.73, 174.7) * mm, "end": v(198.73, 155.45) * mm});
            skLineSegment(sketch, "E2.9.7.3", {"start": v(217.98, 174.7) * mm, "end": v(217.98, 155.45) * mm});
            skLineSegment(sketch, "E2.9.8.0", {"start": v(198.73, 196.34) * mm, "end": v(217.98, 196.34) * mm});
            skLineSegment(sketch, "E2.9.8.1", {"start": v(198.73, 177.09) * mm, "end": v(217.98, 177.09) * mm});
            skLineSegment(sketch, "E2.9.8.2", {"start": v(198.73, 196.34) * mm, "end": v(198.73, 177.09) * mm});
            skLineSegment(sketch, "E2.9.8.3", {"start": v(217.98, 196.34) * mm, "end": v(217.98, 177.09) * mm});
            skLineSegment(sketch, "E2.9.9.0", {"start": v(198.73, 217.98) * mm, "end": v(217.98, 217.98) * mm});
            skLineSegment(sketch, "E2.9.9.1", {"start": v(198.73, 198.73) * mm, "end": v(217.98, 198.73) * mm});
            skLineSegment(sketch, "E2.9.9.2", {"start": v(198.73, 217.98) * mm, "end": v(198.73, 198.73) * mm});
            skLineSegment(sketch, "E2.9.9.3", {"start": v(217.98, 217.98) * mm, "end": v(217.98, 198.73) * mm});
            skLineSegment(sketch, "E2.9.10.0", {"start": v(198.73, 239.62) * mm, "end": v(217.98, 239.62) * mm});
            skLineSegment(sketch, "E2.9.10.1", {"start": v(198.73, 220.37) * mm, "end": v(217.98, 220.37) * mm});
            skLineSegment(sketch, "E2.9.10.2", {"start": v(198.73, 239.62) * mm, "end": v(198.73, 220.37) * mm});
            skLineSegment(sketch, "E2.9.10.3", {"start": v(217.98, 239.62) * mm, "end": v(217.98, 220.37) * mm});
            skLineSegment(sketch, "E2.9.11.0", {"start": v(198.73, 261.26) * mm, "end": v(217.98, 261.26) * mm});
            skLineSegment(sketch, "E2.9.11.1", {"start": v(198.73, 242.01) * mm, "end": v(217.98, 242.01) * mm});
            skLineSegment(sketch, "E2.9.11.2", {"start": v(198.73, 261.26) * mm, "end": v(198.73, 242.01) * mm});
            skLineSegment(sketch, "E2.9.11.3", {"start": v(217.98, 261.26) * mm, "end": v(217.98, 242.01) * mm});
            skLineSegment(sketch, "E2.9.12.0", {"start": v(198.73, 282.9) * mm, "end": v(217.98, 282.9) * mm});
            skLineSegment(sketch, "E2.9.12.1", {"start": v(198.73, 263.65) * mm, "end": v(217.98, 263.65) * mm});
            skLineSegment(sketch, "E2.9.12.2", {"start": v(198.73, 282.9) * mm, "end": v(198.73, 263.65) * mm});
            skLineSegment(sketch, "E2.9.12.3", {"start": v(217.98, 282.9) * mm, "end": v(217.98, 263.65) * mm});
            skLineSegment(sketch, "E2.9.13.0", {"start": v(198.73, 304.55) * mm, "end": v(217.98, 304.55) * mm});
            skLineSegment(sketch, "E2.9.13.1", {"start": v(198.73, 285.3) * mm, "end": v(217.98, 285.3) * mm});
            skLineSegment(sketch, "E2.9.13.2", {"start": v(198.73, 304.55) * mm, "end": v(198.73, 285.3) * mm});
            skLineSegment(sketch, "E2.9.13.3", {"start": v(217.98, 304.55) * mm, "end": v(217.98, 285.3) * mm});
            skLineSegment(sketch, "E2.9.14.0", {"start": v(198.73, 326.19) * mm, "end": v(217.98, 326.19) * mm});
            skLineSegment(sketch, "E2.9.14.1", {"start": v(198.73, 306.93) * mm, "end": v(217.98, 306.93) * mm});
            skLineSegment(sketch, "E2.9.14.2", {"start": v(198.73, 326.19) * mm, "end": v(198.73, 306.93) * mm});
            skLineSegment(sketch, "E2.9.14.3", {"start": v(217.98, 326.19) * mm, "end": v(217.98, 306.93) * mm});
            skLineSegment(sketch, "E2.9.15.0", {"start": v(198.73, 347.83) * mm, "end": v(217.98, 347.83) * mm});
            skLineSegment(sketch, "E2.9.15.1", {"start": v(198.73, 328.57) * mm, "end": v(217.98, 328.57) * mm});
            skLineSegment(sketch, "E2.9.15.2", {"start": v(198.73, 347.83) * mm, "end": v(198.73, 328.57) * mm});
            skLineSegment(sketch, "E2.9.15.3", {"start": v(217.98, 347.83) * mm, "end": v(217.98, 328.57) * mm});
            skLineSegment(sketch, "E2.9.16.0", {"start": v(198.73, 369.47) * mm, "end": v(217.98, 369.47) * mm});
            skLineSegment(sketch, "E2.9.16.1", {"start": v(198.73, 350.22) * mm, "end": v(217.98, 350.22) * mm});
            skLineSegment(sketch, "E2.9.16.2", {"start": v(198.73, 369.47) * mm, "end": v(198.73, 350.22) * mm});
            skLineSegment(sketch, "E2.9.16.3", {"start": v(217.98, 369.47) * mm, "end": v(217.98, 350.22) * mm});
            skLineSegment(sketch, "E2.9.17.0", {"start": v(198.73, 391.1) * mm, "end": v(217.98, 391.1) * mm});
            skLineSegment(sketch, "E2.9.17.1", {"start": v(198.73, 371.86) * mm, "end": v(217.98, 371.86) * mm});
            skLineSegment(sketch, "E2.9.17.2", {"start": v(198.73, 391.1) * mm, "end": v(198.73, 371.86) * mm});
            skLineSegment(sketch, "E2.9.17.3", {"start": v(217.98, 391.1) * mm, "end": v(217.98, 371.86) * mm});
            skLineSegment(sketch, "E2.9.18.0", {"start": v(198.73, 412.75) * mm, "end": v(217.98, 412.75) * mm});
            skLineSegment(sketch, "E2.9.18.1", {"start": v(198.73, 393.5) * mm, "end": v(217.98, 393.5) * mm});
            skLineSegment(sketch, "E2.9.18.2", {"start": v(198.73, 412.75) * mm, "end": v(198.73, 393.5) * mm});
            skLineSegment(sketch, "E2.9.18.3", {"start": v(217.98, 412.75) * mm, "end": v(217.98, 393.5) * mm});
            skLineSegment(sketch, "E2.9.19.0", {"start": v(198.73, 434.4) * mm, "end": v(217.98, 434.4) * mm});
            skLineSegment(sketch, "E2.9.19.1", {"start": v(198.73, 415.14) * mm, "end": v(217.98, 415.14) * mm});
            skLineSegment(sketch, "E2.9.19.2", {"start": v(198.73, 434.4) * mm, "end": v(198.73, 415.14) * mm});
            skLineSegment(sketch, "E2.9.19.3", {"start": v(217.98, 434.4) * mm, "end": v(217.98, 415.14) * mm});
            skLineSegment(sketch, "E2.9.20.0", {"start": v(198.73, 456.03) * mm, "end": v(217.98, 456.03) * mm});
            skLineSegment(sketch, "E2.9.20.1", {"start": v(198.73, 436.78) * mm, "end": v(217.98, 436.78) * mm});
            skLineSegment(sketch, "E2.9.20.2", {"start": v(198.73, 456.03) * mm, "end": v(198.73, 436.78) * mm});
            skLineSegment(sketch, "E2.9.20.3", {"start": v(217.98, 456.03) * mm, "end": v(217.98, 436.78) * mm});
            skLineSegment(sketch, "E2.9.21.0", {"start": v(198.73, 477.67) * mm, "end": v(217.98, 477.67) * mm});
            skLineSegment(sketch, "E2.9.21.1", {"start": v(198.73, 458.42) * mm, "end": v(217.98, 458.42) * mm});
            skLineSegment(sketch, "E2.9.21.2", {"start": v(198.73, 477.67) * mm, "end": v(198.73, 458.42) * mm});
            skLineSegment(sketch, "E2.9.21.3", {"start": v(217.98, 477.67) * mm, "end": v(217.98, 458.42) * mm});
            skLineSegment(sketch, "E2.9.22.0", {"start": v(198.73, 499.31) * mm, "end": v(217.98, 499.31) * mm});
            skLineSegment(sketch, "E2.9.22.1", {"start": v(198.73, 480.06) * mm, "end": v(217.98, 480.06) * mm});
            skLineSegment(sketch, "E2.9.22.2", {"start": v(198.73, 499.31) * mm, "end": v(198.73, 480.06) * mm});
            skLineSegment(sketch, "E2.9.22.3", {"start": v(217.98, 499.31) * mm, "end": v(217.98, 480.06) * mm});
            skLineSegment(sketch, "E2.9.23.0", {"start": v(198.73, 520.95) * mm, "end": v(217.98, 520.95) * mm});
            skLineSegment(sketch, "E2.9.23.1", {"start": v(198.73, 501.7) * mm, "end": v(217.98, 501.7) * mm});
            skLineSegment(sketch, "E2.9.23.2", {"start": v(198.73, 520.95) * mm, "end": v(198.73, 501.7) * mm});
            skLineSegment(sketch, "E2.9.23.3", {"start": v(217.98, 520.95) * mm, "end": v(217.98, 501.7) * mm});
            skLineSegment(sketch, "E2.10.0.0", {"start": v(220.37, 23.22) * mm, "end": v(239.62, 23.22) * mm});
            skLineSegment(sketch, "E2.10.0.1", {"start": v(220.37, 3.96) * mm, "end": v(239.62, 3.96) * mm});
            skLineSegment(sketch, "E2.10.0.2", {"start": v(220.37, 23.22) * mm, "end": v(220.37, 3.96) * mm});
            skLineSegment(sketch, "E2.10.0.3", {"start": v(239.62, 23.22) * mm, "end": v(239.62, 3.96) * mm});
            skLineSegment(sketch, "E2.10.1.0", {"start": v(220.37, 44.86) * mm, "end": v(239.62, 44.86) * mm});
            skLineSegment(sketch, "E2.10.1.1", {"start": v(220.37, 25.6) * mm, "end": v(239.62, 25.6) * mm});
            skLineSegment(sketch, "E2.10.1.2", {"start": v(220.37, 44.86) * mm, "end": v(220.37, 25.6) * mm});
            skLineSegment(sketch, "E2.10.1.3", {"start": v(239.62, 44.86) * mm, "end": v(239.62, 25.6) * mm});
            skLineSegment(sketch, "E2.10.2.0", {"start": v(220.37, 66.5) * mm, "end": v(239.62, 66.5) * mm});
            skLineSegment(sketch, "E2.10.2.1", {"start": v(220.37, 47.24) * mm, "end": v(239.62, 47.24) * mm});
            skLineSegment(sketch, "E2.10.2.2", {"start": v(220.37, 66.5) * mm, "end": v(220.37, 47.24) * mm});
            skLineSegment(sketch, "E2.10.2.3", {"start": v(239.62, 66.5) * mm, "end": v(239.62, 47.24) * mm});
            skLineSegment(sketch, "E2.10.3.0", {"start": v(220.37, 88.14) * mm, "end": v(239.62, 88.14) * mm});
            skLineSegment(sketch, "E2.10.3.1", {"start": v(220.37, 68.88) * mm, "end": v(239.62, 68.88) * mm});
            skLineSegment(sketch, "E2.10.3.2", {"start": v(220.37, 88.14) * mm, "end": v(220.37, 68.88) * mm});
            skLineSegment(sketch, "E2.10.3.3", {"start": v(239.62, 88.14) * mm, "end": v(239.62, 68.88) * mm});
            skLineSegment(sketch, "E2.10.4.0", {"start": v(220.37, 109.78) * mm, "end": v(239.62, 109.78) * mm});
            skLineSegment(sketch, "E2.10.4.1", {"start": v(220.37, 90.53) * mm, "end": v(239.62, 90.53) * mm});
            skLineSegment(sketch, "E2.10.4.2", {"start": v(220.37, 109.78) * mm, "end": v(220.37, 90.53) * mm});
            skLineSegment(sketch, "E2.10.4.3", {"start": v(239.62, 109.78) * mm, "end": v(239.62, 90.53) * mm});
            skLineSegment(sketch, "E2.10.5.0", {"start": v(220.37, 131.42) * mm, "end": v(239.62, 131.42) * mm});
            skLineSegment(sketch, "E2.10.5.1", {"start": v(220.37, 112.17) * mm, "end": v(239.62, 112.17) * mm});
            skLineSegment(sketch, "E2.10.5.2", {"start": v(220.37, 131.42) * mm, "end": v(220.37, 112.17) * mm});
            skLineSegment(sketch, "E2.10.5.3", {"start": v(239.62, 131.42) * mm, "end": v(239.62, 112.17) * mm});
            skLineSegment(sketch, "E2.10.6.0", {"start": v(220.37, 153.06) * mm, "end": v(239.62, 153.06) * mm});
            skLineSegment(sketch, "E2.10.6.1", {"start": v(220.37, 133.8) * mm, "end": v(239.62, 133.8) * mm});
            skLineSegment(sketch, "E2.10.6.2", {"start": v(220.37, 153.06) * mm, "end": v(220.37, 133.8) * mm});
            skLineSegment(sketch, "E2.10.6.3", {"start": v(239.62, 153.06) * mm, "end": v(239.62, 133.8) * mm});
            skLineSegment(sketch, "E2.10.7.0", {"start": v(220.37, 174.7) * mm, "end": v(239.62, 174.7) * mm});
            skLineSegment(sketch, "E2.10.7.1", {"start": v(220.37, 155.45) * mm, "end": v(239.62, 155.45) * mm});
            skLineSegment(sketch, "E2.10.7.2", {"start": v(220.37, 174.7) * mm, "end": v(220.37, 155.45) * mm});
            skLineSegment(sketch, "E2.10.7.3", {"start": v(239.62, 174.7) * mm, "end": v(239.62, 155.45) * mm});
            skLineSegment(sketch, "E2.10.8.0", {"start": v(220.37, 196.34) * mm, "end": v(239.62, 196.34) * mm});
            skLineSegment(sketch, "E2.10.8.1", {"start": v(220.37, 177.09) * mm, "end": v(239.62, 177.09) * mm});
            skLineSegment(sketch, "E2.10.8.2", {"start": v(220.37, 196.34) * mm, "end": v(220.37, 177.09) * mm});
            skLineSegment(sketch, "E2.10.8.3", {"start": v(239.62, 196.34) * mm, "end": v(239.62, 177.09) * mm});
            skLineSegment(sketch, "E2.10.9.0", {"start": v(220.37, 217.98) * mm, "end": v(239.62, 217.98) * mm});
            skLineSegment(sketch, "E2.10.9.1", {"start": v(220.37, 198.73) * mm, "end": v(239.62, 198.73) * mm});
            skLineSegment(sketch, "E2.10.9.2", {"start": v(220.37, 217.98) * mm, "end": v(220.37, 198.73) * mm});
            skLineSegment(sketch, "E2.10.9.3", {"start": v(239.62, 217.98) * mm, "end": v(239.62, 198.73) * mm});
            skLineSegment(sketch, "E2.10.10.0", {"start": v(220.37, 239.62) * mm, "end": v(239.62, 239.62) * mm});
            skLineSegment(sketch, "E2.10.10.1", {"start": v(220.37, 220.37) * mm, "end": v(239.62, 220.37) * mm});
            skLineSegment(sketch, "E2.10.10.2", {"start": v(220.37, 239.62) * mm, "end": v(220.37, 220.37) * mm});
            skLineSegment(sketch, "E2.10.10.3", {"start": v(239.62, 239.62) * mm, "end": v(239.62, 220.37) * mm});
            skLineSegment(sketch, "E2.10.11.0", {"start": v(220.37, 261.26) * mm, "end": v(239.62, 261.26) * mm});
            skLineSegment(sketch, "E2.10.11.1", {"start": v(220.37, 242.01) * mm, "end": v(239.62, 242.01) * mm});
            skLineSegment(sketch, "E2.10.11.2", {"start": v(220.37, 261.26) * mm, "end": v(220.37, 242.01) * mm});
            skLineSegment(sketch, "E2.10.11.3", {"start": v(239.62, 261.26) * mm, "end": v(239.62, 242.01) * mm});
            skLineSegment(sketch, "E2.10.12.0", {"start": v(220.37, 282.9) * mm, "end": v(239.62, 282.9) * mm});
            skLineSegment(sketch, "E2.10.12.1", {"start": v(220.37, 263.65) * mm, "end": v(239.62, 263.65) * mm});
            skLineSegment(sketch, "E2.10.12.2", {"start": v(220.37, 282.9) * mm, "end": v(220.37, 263.65) * mm});
            skLineSegment(sketch, "E2.10.12.3", {"start": v(239.62, 282.9) * mm, "end": v(239.62, 263.65) * mm});
            skLineSegment(sketch, "E2.10.13.0", {"start": v(220.37, 304.55) * mm, "end": v(239.62, 304.55) * mm});
            skLineSegment(sketch, "E2.10.13.1", {"start": v(220.37, 285.3) * mm, "end": v(239.62, 285.3) * mm});
            skLineSegment(sketch, "E2.10.13.2", {"start": v(220.37, 304.55) * mm, "end": v(220.37, 285.3) * mm});
            skLineSegment(sketch, "E2.10.13.3", {"start": v(239.62, 304.55) * mm, "end": v(239.62, 285.3) * mm});
            skLineSegment(sketch, "E2.10.14.0", {"start": v(220.37, 326.19) * mm, "end": v(239.62, 326.19) * mm});
            skLineSegment(sketch, "E2.10.14.1", {"start": v(220.37, 306.93) * mm, "end": v(239.62, 306.93) * mm});
            skLineSegment(sketch, "E2.10.14.2", {"start": v(220.37, 326.19) * mm, "end": v(220.37, 306.93) * mm});
            skLineSegment(sketch, "E2.10.14.3", {"start": v(239.62, 326.19) * mm, "end": v(239.62, 306.93) * mm});
            skLineSegment(sketch, "E2.10.15.0", {"start": v(220.37, 347.83) * mm, "end": v(239.62, 347.83) * mm});
            skLineSegment(sketch, "E2.10.15.1", {"start": v(220.37, 328.57) * mm, "end": v(239.62, 328.57) * mm});
            skLineSegment(sketch, "E2.10.15.2", {"start": v(220.37, 347.83) * mm, "end": v(220.37, 328.57) * mm});
            skLineSegment(sketch, "E2.10.15.3", {"start": v(239.62, 347.83) * mm, "end": v(239.62, 328.57) * mm});
            skLineSegment(sketch, "E2.10.16.0", {"start": v(220.37, 369.47) * mm, "end": v(239.62, 369.47) * mm});
            skLineSegment(sketch, "E2.10.16.1", {"start": v(220.37, 350.22) * mm, "end": v(239.62, 350.22) * mm});
            skLineSegment(sketch, "E2.10.16.2", {"start": v(220.37, 369.47) * mm, "end": v(220.37, 350.22) * mm});
            skLineSegment(sketch, "E2.10.16.3", {"start": v(239.62, 369.47) * mm, "end": v(239.62, 350.22) * mm});
            skLineSegment(sketch, "E2.10.17.0", {"start": v(220.37, 391.1) * mm, "end": v(239.62, 391.1) * mm});
            skLineSegment(sketch, "E2.10.17.1", {"start": v(220.37, 371.86) * mm, "end": v(239.62, 371.86) * mm});
            skLineSegment(sketch, "E2.10.17.2", {"start": v(220.37, 391.1) * mm, "end": v(220.37, 371.86) * mm});
            skLineSegment(sketch, "E2.10.17.3", {"start": v(239.62, 391.1) * mm, "end": v(239.62, 371.86) * mm});
            skLineSegment(sketch, "E2.10.18.0", {"start": v(220.37, 412.75) * mm, "end": v(239.62, 412.75) * mm});
            skLineSegment(sketch, "E2.10.18.1", {"start": v(220.37, 393.5) * mm, "end": v(239.62, 393.5) * mm});
            skLineSegment(sketch, "E2.10.18.2", {"start": v(220.37, 412.75) * mm, "end": v(220.37, 393.5) * mm});
            skLineSegment(sketch, "E2.10.18.3", {"start": v(239.62, 412.75) * mm, "end": v(239.62, 393.5) * mm});
            skLineSegment(sketch, "E2.10.19.0", {"start": v(220.37, 434.4) * mm, "end": v(239.62, 434.4) * mm});
            skLineSegment(sketch, "E2.10.19.1", {"start": v(220.37, 415.14) * mm, "end": v(239.62, 415.14) * mm});
            skLineSegment(sketch, "E2.10.19.2", {"start": v(220.37, 434.4) * mm, "end": v(220.37, 415.14) * mm});
            skLineSegment(sketch, "E2.10.19.3", {"start": v(239.62, 434.4) * mm, "end": v(239.62, 415.14) * mm});
            skLineSegment(sketch, "E2.10.20.0", {"start": v(220.37, 456.03) * mm, "end": v(239.62, 456.03) * mm});
            skLineSegment(sketch, "E2.10.20.1", {"start": v(220.37, 436.78) * mm, "end": v(239.62, 436.78) * mm});
            skLineSegment(sketch, "E2.10.20.2", {"start": v(220.37, 456.03) * mm, "end": v(220.37, 436.78) * mm});
            skLineSegment(sketch, "E2.10.20.3", {"start": v(239.62, 456.03) * mm, "end": v(239.62, 436.78) * mm});
            skLineSegment(sketch, "E2.10.21.0", {"start": v(220.37, 477.67) * mm, "end": v(239.62, 477.67) * mm});
            skLineSegment(sketch, "E2.10.21.1", {"start": v(220.37, 458.42) * mm, "end": v(239.62, 458.42) * mm});
            skLineSegment(sketch, "E2.10.21.2", {"start": v(220.37, 477.67) * mm, "end": v(220.37, 458.42) * mm});
            skLineSegment(sketch, "E2.10.21.3", {"start": v(239.62, 477.67) * mm, "end": v(239.62, 458.42) * mm});
            skLineSegment(sketch, "E2.10.22.0", {"start": v(220.37, 499.31) * mm, "end": v(239.62, 499.31) * mm});
            skLineSegment(sketch, "E2.10.22.1", {"start": v(220.37, 480.06) * mm, "end": v(239.62, 480.06) * mm});
            skLineSegment(sketch, "E2.10.22.2", {"start": v(220.37, 499.31) * mm, "end": v(220.37, 480.06) * mm});
            skLineSegment(sketch, "E2.10.22.3", {"start": v(239.62, 499.31) * mm, "end": v(239.62, 480.06) * mm});
            skLineSegment(sketch, "E2.10.23.0", {"start": v(220.37, 520.95) * mm, "end": v(239.62, 520.95) * mm});
            skLineSegment(sketch, "E2.10.23.1", {"start": v(220.37, 501.7) * mm, "end": v(239.62, 501.7) * mm});
            skLineSegment(sketch, "E2.10.23.2", {"start": v(220.37, 520.95) * mm, "end": v(220.37, 501.7) * mm});
            skLineSegment(sketch, "E2.10.23.3", {"start": v(239.62, 520.95) * mm, "end": v(239.62, 501.7) * mm});
            skLineSegment(sketch, "E2.11.0.0", {"start": v(242.01, 23.22) * mm, "end": v(261.26, 23.22) * mm});
            skLineSegment(sketch, "E2.11.0.1", {"start": v(242.01, 3.96) * mm, "end": v(261.26, 3.96) * mm});
            skLineSegment(sketch, "E2.11.0.2", {"start": v(242.01, 23.22) * mm, "end": v(242.01, 3.96) * mm});
            skLineSegment(sketch, "E2.11.0.3", {"start": v(261.26, 23.22) * mm, "end": v(261.26, 3.96) * mm});
            skLineSegment(sketch, "E2.11.1.0", {"start": v(242.01, 44.86) * mm, "end": v(261.26, 44.86) * mm});
            skLineSegment(sketch, "E2.11.1.1", {"start": v(242.01, 25.6) * mm, "end": v(261.26, 25.6) * mm});
            skLineSegment(sketch, "E2.11.1.2", {"start": v(242.01, 44.86) * mm, "end": v(242.01, 25.6) * mm});
            skLineSegment(sketch, "E2.11.1.3", {"start": v(261.26, 44.86) * mm, "end": v(261.26, 25.6) * mm});
            skLineSegment(sketch, "E2.11.2.0", {"start": v(242.01, 66.5) * mm, "end": v(261.26, 66.5) * mm});
            skLineSegment(sketch, "E2.11.2.1", {"start": v(242.01, 47.24) * mm, "end": v(261.26, 47.24) * mm});
            skLineSegment(sketch, "E2.11.2.2", {"start": v(242.01, 66.5) * mm, "end": v(242.01, 47.24) * mm});
            skLineSegment(sketch, "E2.11.2.3", {"start": v(261.26, 66.5) * mm, "end": v(261.26, 47.24) * mm});
            skLineSegment(sketch, "E2.11.3.0", {"start": v(242.01, 88.14) * mm, "end": v(261.26, 88.14) * mm});
            skLineSegment(sketch, "E2.11.3.1", {"start": v(242.01, 68.88) * mm, "end": v(261.26, 68.88) * mm});
            skLineSegment(sketch, "E2.11.3.2", {"start": v(242.01, 88.14) * mm, "end": v(242.01, 68.88) * mm});
            skLineSegment(sketch, "E2.11.3.3", {"start": v(261.26, 88.14) * mm, "end": v(261.26, 68.88) * mm});
            skLineSegment(sketch, "E2.11.4.0", {"start": v(242.01, 109.78) * mm, "end": v(261.26, 109.78) * mm});
            skLineSegment(sketch, "E2.11.4.1", {"start": v(242.01, 90.53) * mm, "end": v(261.26, 90.53) * mm});
            skLineSegment(sketch, "E2.11.4.2", {"start": v(242.01, 109.78) * mm, "end": v(242.01, 90.53) * mm});
            skLineSegment(sketch, "E2.11.4.3", {"start": v(261.26, 109.78) * mm, "end": v(261.26, 90.53) * mm});
            skLineSegment(sketch, "E2.11.5.0", {"start": v(242.01, 131.42) * mm, "end": v(261.26, 131.42) * mm});
            skLineSegment(sketch, "E2.11.5.1", {"start": v(242.01, 112.17) * mm, "end": v(261.26, 112.17) * mm});
            skLineSegment(sketch, "E2.11.5.2", {"start": v(242.01, 131.42) * mm, "end": v(242.01, 112.17) * mm});
            skLineSegment(sketch, "E2.11.5.3", {"start": v(261.26, 131.42) * mm, "end": v(261.26, 112.17) * mm});
            skLineSegment(sketch, "E2.11.6.0", {"start": v(242.01, 153.06) * mm, "end": v(261.26, 153.06) * mm});
            skLineSegment(sketch, "E2.11.6.1", {"start": v(242.01, 133.8) * mm, "end": v(261.26, 133.8) * mm});
            skLineSegment(sketch, "E2.11.6.2", {"start": v(242.01, 153.06) * mm, "end": v(242.01, 133.8) * mm});
            skLineSegment(sketch, "E2.11.6.3", {"start": v(261.26, 153.06) * mm, "end": v(261.26, 133.8) * mm});
            skLineSegment(sketch, "E2.11.7.0", {"start": v(242.01, 174.7) * mm, "end": v(261.26, 174.7) * mm});
            skLineSegment(sketch, "E2.11.7.1", {"start": v(242.01, 155.45) * mm, "end": v(261.26, 155.45) * mm});
            skLineSegment(sketch, "E2.11.7.2", {"start": v(242.01, 174.7) * mm, "end": v(242.01, 155.45) * mm});
            skLineSegment(sketch, "E2.11.7.3", {"start": v(261.26, 174.7) * mm, "end": v(261.26, 155.45) * mm});
            skLineSegment(sketch, "E2.11.8.0", {"start": v(242.01, 196.34) * mm, "end": v(261.26, 196.34) * mm});
            skLineSegment(sketch, "E2.11.8.1", {"start": v(242.01, 177.09) * mm, "end": v(261.26, 177.09) * mm});
            skLineSegment(sketch, "E2.11.8.2", {"start": v(242.01, 196.34) * mm, "end": v(242.01, 177.09) * mm});
            skLineSegment(sketch, "E2.11.8.3", {"start": v(261.26, 196.34) * mm, "end": v(261.26, 177.09) * mm});
            skLineSegment(sketch, "E2.11.9.0", {"start": v(242.01, 217.98) * mm, "end": v(261.26, 217.98) * mm});
            skLineSegment(sketch, "E2.11.9.1", {"start": v(242.01, 198.73) * mm, "end": v(261.26, 198.73) * mm});
            skLineSegment(sketch, "E2.11.9.2", {"start": v(242.01, 217.98) * mm, "end": v(242.01, 198.73) * mm});
            skLineSegment(sketch, "E2.11.9.3", {"start": v(261.26, 217.98) * mm, "end": v(261.26, 198.73) * mm});
            skLineSegment(sketch, "E2.11.10.0", {"start": v(242.01, 239.62) * mm, "end": v(261.26, 239.62) * mm});
            skLineSegment(sketch, "E2.11.10.1", {"start": v(242.01, 220.37) * mm, "end": v(261.26, 220.37) * mm});
            skLineSegment(sketch, "E2.11.10.2", {"start": v(242.01, 239.62) * mm, "end": v(242.01, 220.37) * mm});
            skLineSegment(sketch, "E2.11.10.3", {"start": v(261.26, 239.62) * mm, "end": v(261.26, 220.37) * mm});
            skLineSegment(sketch, "E2.11.11.0", {"start": v(242.01, 261.26) * mm, "end": v(261.26, 261.26) * mm});
            skLineSegment(sketch, "E2.11.11.1", {"start": v(242.01, 242.01) * mm, "end": v(261.26, 242.01) * mm});
            skLineSegment(sketch, "E2.11.11.2", {"start": v(242.01, 261.26) * mm, "end": v(242.01, 242.01) * mm});
            skLineSegment(sketch, "E2.11.11.3", {"start": v(261.26, 261.26) * mm, "end": v(261.26, 242.01) * mm});
            skLineSegment(sketch, "E2.11.12.0", {"start": v(242.01, 282.9) * mm, "end": v(261.26, 282.9) * mm});
            skLineSegment(sketch, "E2.11.12.1", {"start": v(242.01, 263.65) * mm, "end": v(261.26, 263.65) * mm});
            skLineSegment(sketch, "E2.11.12.2", {"start": v(242.01, 282.9) * mm, "end": v(242.01, 263.65) * mm});
            skLineSegment(sketch, "E2.11.12.3", {"start": v(261.26, 282.9) * mm, "end": v(261.26, 263.65) * mm});
            skLineSegment(sketch, "E2.11.13.0", {"start": v(242.01, 304.55) * mm, "end": v(261.26, 304.55) * mm});
            skLineSegment(sketch, "E2.11.13.1", {"start": v(242.01, 285.3) * mm, "end": v(261.26, 285.3) * mm});
            skLineSegment(sketch, "E2.11.13.2", {"start": v(242.01, 304.55) * mm, "end": v(242.01, 285.3) * mm});
            skLineSegment(sketch, "E2.11.13.3", {"start": v(261.26, 304.55) * mm, "end": v(261.26, 285.3) * mm});
            skLineSegment(sketch, "E2.11.14.0", {"start": v(242.01, 326.19) * mm, "end": v(261.26, 326.19) * mm});
            skLineSegment(sketch, "E2.11.14.1", {"start": v(242.01, 306.93) * mm, "end": v(261.26, 306.93) * mm});
            skLineSegment(sketch, "E2.11.14.2", {"start": v(242.01, 326.19) * mm, "end": v(242.01, 306.93) * mm});
            skLineSegment(sketch, "E2.11.14.3", {"start": v(261.26, 326.19) * mm, "end": v(261.26, 306.93) * mm});
            skLineSegment(sketch, "E2.11.15.0", {"start": v(242.01, 347.83) * mm, "end": v(261.26, 347.83) * mm});
            skLineSegment(sketch, "E2.11.15.1", {"start": v(242.01, 328.57) * mm, "end": v(261.26, 328.57) * mm});
            skLineSegment(sketch, "E2.11.15.2", {"start": v(242.01, 347.83) * mm, "end": v(242.01, 328.57) * mm});
            skLineSegment(sketch, "E2.11.15.3", {"start": v(261.26, 347.83) * mm, "end": v(261.26, 328.57) * mm});
            skLineSegment(sketch, "E2.11.16.0", {"start": v(242.01, 369.47) * mm, "end": v(261.26, 369.47) * mm});
            skLineSegment(sketch, "E2.11.16.1", {"start": v(242.01, 350.22) * mm, "end": v(261.26, 350.22) * mm});
            skLineSegment(sketch, "E2.11.16.2", {"start": v(242.01, 369.47) * mm, "end": v(242.01, 350.22) * mm});
            skLineSegment(sketch, "E2.11.16.3", {"start": v(261.26, 369.47) * mm, "end": v(261.26, 350.22) * mm});
            skLineSegment(sketch, "E2.11.17.0", {"start": v(242.01, 391.1) * mm, "end": v(261.26, 391.1) * mm});
            skLineSegment(sketch, "E2.11.17.1", {"start": v(242.01, 371.86) * mm, "end": v(261.26, 371.86) * mm});
            skLineSegment(sketch, "E2.11.17.2", {"start": v(242.01, 391.1) * mm, "end": v(242.01, 371.86) * mm});
            skLineSegment(sketch, "E2.11.17.3", {"start": v(261.26, 391.1) * mm, "end": v(261.26, 371.86) * mm});
            skLineSegment(sketch, "E2.11.18.0", {"start": v(242.01, 412.75) * mm, "end": v(261.26, 412.75) * mm});
            skLineSegment(sketch, "E2.11.18.1", {"start": v(242.01, 393.5) * mm, "end": v(261.26, 393.5) * mm});
            skLineSegment(sketch, "E2.11.18.2", {"start": v(242.01, 412.75) * mm, "end": v(242.01, 393.5) * mm});
            skLineSegment(sketch, "E2.11.18.3", {"start": v(261.26, 412.75) * mm, "end": v(261.26, 393.5) * mm});
            skLineSegment(sketch, "E2.11.19.0", {"start": v(242.01, 434.4) * mm, "end": v(261.26, 434.4) * mm});
            skLineSegment(sketch, "E2.11.19.1", {"start": v(242.01, 415.14) * mm, "end": v(261.26, 415.14) * mm});
            skLineSegment(sketch, "E2.11.19.2", {"start": v(242.01, 434.4) * mm, "end": v(242.01, 415.14) * mm});
            skLineSegment(sketch, "E2.11.19.3", {"start": v(261.26, 434.4) * mm, "end": v(261.26, 415.14) * mm});
            skLineSegment(sketch, "E2.11.20.0", {"start": v(242.01, 456.03) * mm, "end": v(261.26, 456.03) * mm});
            skLineSegment(sketch, "E2.11.20.1", {"start": v(242.01, 436.78) * mm, "end": v(261.26, 436.78) * mm});
            skLineSegment(sketch, "E2.11.20.2", {"start": v(242.01, 456.03) * mm, "end": v(242.01, 436.78) * mm});
            skLineSegment(sketch, "E2.11.20.3", {"start": v(261.26, 456.03) * mm, "end": v(261.26, 436.78) * mm});
            skLineSegment(sketch, "E2.11.21.0", {"start": v(242.01, 477.67) * mm, "end": v(261.26, 477.67) * mm});
            skLineSegment(sketch, "E2.11.21.1", {"start": v(242.01, 458.42) * mm, "end": v(261.26, 458.42) * mm});
            skLineSegment(sketch, "E2.11.21.2", {"start": v(242.01, 477.67) * mm, "end": v(242.01, 458.42) * mm});
            skLineSegment(sketch, "E2.11.21.3", {"start": v(261.26, 477.67) * mm, "end": v(261.26, 458.42) * mm});
            skLineSegment(sketch, "E2.11.22.0", {"start": v(242.01, 499.31) * mm, "end": v(261.26, 499.31) * mm});
            skLineSegment(sketch, "E2.11.22.1", {"start": v(242.01, 480.06) * mm, "end": v(261.26, 480.06) * mm});
            skLineSegment(sketch, "E2.11.22.2", {"start": v(242.01, 499.31) * mm, "end": v(242.01, 480.06) * mm});
            skLineSegment(sketch, "E2.11.22.3", {"start": v(261.26, 499.31) * mm, "end": v(261.26, 480.06) * mm});
            skLineSegment(sketch, "E2.11.23.0", {"start": v(242.01, 520.95) * mm, "end": v(261.26, 520.95) * mm});
            skLineSegment(sketch, "E2.11.23.1", {"start": v(242.01, 501.7) * mm, "end": v(261.26, 501.7) * mm});
            skLineSegment(sketch, "E2.11.23.2", {"start": v(242.01, 520.95) * mm, "end": v(242.01, 501.7) * mm});
            skLineSegment(sketch, "E2.11.23.3", {"start": v(261.26, 520.95) * mm, "end": v(261.26, 501.7) * mm});
            skLineSegment(sketch, "E2.direction1", {"start": v(3.96, 3.96) * mm, "end": v(25.6, 3.96) * mm, "construction": true});
            skLineSegment(sketch, "E2.direction2", {"start": v(3.96, 3.96) * mm, "end": v(3.96, 25.6) * mm, "construction": true});
            skSolve(sketch);
        }
        {
            var Q0;
            Q0=qSketchRegion(id+"F0",true);
            extrude(context, id + "F1", {"entities" : qUnion([Q0]), "depth" : 25.4 * mm, "offsetDistance" : 25.4 * mm});
        }
        {
            var Q0;
            Q0=makeQuery(id+"F1.opExtrude","SWEPT_BODY",BODY,{"disambiguationData":[OSD([sQuery(id+"F0.wireOp",EDGE,"E0.bottom"),sQuery(id+"F0.wireOp",EDGE,"E0.top"),sQuery(id+"F0.wireOp",EDGE,"E0.left"),sQuery(id+"F0.wireOp",EDGE,"E0.right"),sQuery(id+"F0.wireOp",EDGE,"E1.bottom"),sQuery(id+"F0.wireOp",EDGE,"E1.top"),sQuery(id+"F0.wireOp",EDGE,"E1.left"),sQuery(id+"F0.wireOp",EDGE,"E1.right"),sQuery(id+"F0.wireOp",EDGE,"E2.0.1.0"),sQuery(id+"F0.wireOp",EDGE,"E2.0.1.1"),sQuery(id+"F0.wireOp",EDGE,"E2.0.1.2"),sQuery(id+"F0.wireOp",EDGE,"E2.0.1.3"),sQuery(id+"F0.wireOp",EDGE,"E2.0.2.0"),sQuery(id+"F0.wireOp",EDGE,"E2.0.2.1"),sQuery(id+"F0.wireOp",EDGE,"E2.0.2.2"),sQuery(id+"F0.wireOp",EDGE,"E2.0.2.3"),sQuery(id+"F0.wireOp",EDGE,"E2.0.3.0"),sQuery(id+"F0.wireOp",EDGE,"E2.0.3.1"),sQuery(id+"F0.wireOp",EDGE,"E2.0.3.2"),sQuery(id+"F0.wireOp",EDGE,"E2.0.3.3"),sQuery(id+"F0.wireOp",EDGE,"E2.0.4.0"),sQuery(id+"F0.wireOp",EDGE,"E2.0.4.1"),sQuery(id+"F0.wireOp",EDGE,"E2.0.4.2"),sQuery(id+"F0.wireOp",EDGE,"E2.0.4.3"),sQuery(id+"F0.wireOp",EDGE,"E2.0.5.0"),sQuery(id+"F0.wireOp",EDGE,"E2.0.5.1"),sQuery(id+"F0.wireOp",EDGE,"E2.0.5.2"),sQuery(id+"F0.wireOp",EDGE,"E2.0.5.3"),sQuery(id+"F0.wireOp",EDGE,"E2.0.6.0"),sQuery(id+"F0.wireOp",EDGE,"E2.0.6.1"),sQuery(id+"F0.wireOp",EDGE,"E2.0.6.2"),sQuery(id+"F0.wireOp",EDGE,"E2.0.6.3"),sQuery(id+"F0.wireOp",EDGE,"E2.0.7.0"),sQuery(id+"F0.wireOp",EDGE,"E2.0.7.1"),sQuery(id+"F0.wireOp",EDGE,"E2.0.7.2"),sQuery(id+"F0.wireOp",EDGE,"E2.0.7.3"),sQuery(id+"F0.wireOp",EDGE,"E2.0.8.0"),sQuery(id+"F0.wireOp",EDGE,"E2.0.8.1"),sQuery(id+"F0.wireOp",EDGE,"E2.0.8.2"),sQuery(id+"F0.wireOp",EDGE,"E2.0.8.3"),sQuery(id+"F0.wireOp",EDGE,"E2.0.9.0"),sQuery(id+"F0.wireOp",EDGE,"E2.0.9.1"),sQuery(id+"F0.wireOp",EDGE,"E2.0.9.2"),sQuery(id+"F0.wireOp",EDGE,"E2.0.9.3"),sQuery(id+"F0.wireOp",EDGE,"E2.0.10.0"),sQuery(id+"F0.wireOp",EDGE,"E2.0.10.1"),sQuery(id+"F0.wireOp",EDGE,"E2.0.10.2"),sQuery(id+"F0.wireOp",EDGE,"E2.0.10.3"),sQuery(id+"F0.wireOp",EDGE,"E2.0.11.0"),sQuery(id+"F0.wireOp",EDGE,"E2.0.11.1"),sQuery(id+"F0.wireOp",EDGE,"E2.0.11.2"),sQuery(id+"F0.wireOp",EDGE,"E2.0.11.3"),sQuery(id+"F0.wireOp",EDGE,"E2.0.12.0"),sQuery(id+"F0.wireOp",EDGE,"E2.0.12.1"),sQuery(id+"F0.wireOp",EDGE,"E2.0.12.2"),sQuery(id+"F0.wireOp",EDGE,"E2.0.12.3"),sQuery(id+"F0.wireOp",EDGE,"E2.0.13.0"),sQuery(id+"F0.wireOp",EDGE,"E2.0.13.1"),sQuery(id+"F0.wireOp",EDGE,"E2.0.13.2"),sQuery(id+"F0.wireOp",EDGE,"E2.0.13.3"),sQuery(id+"F0.wireOp",EDGE,"E2.0.14.0"),sQuery(id+"F0.wireOp",EDGE,"E2.0.14.1"),sQuery(id+"F0.wireOp",EDGE,"E2.0.14.2"),sQuery(id+"F0.wireOp",EDGE,"E2.0.14.3"),sQuery(id+"F0.wireOp",EDGE,"E2.0.15.0"),sQuery(id+"F0.wireOp",EDGE,"E2.0.15.1"),sQuery(id+"F0.wireOp",EDGE,"E2.0.15.2"),sQuery(id+"F0.wireOp",EDGE,"E2.0.15.3"),sQuery(id+"F0.wireOp",EDGE,"E2.0.16.0"),sQuery(id+"F0.wireOp",EDGE,"E2.0.16.1"),sQuery(id+"F0.wireOp",EDGE,"E2.0.16.2"),sQuery(id+"F0.wireOp",EDGE,"E2.0.16.3"),sQuery(id+"F0.wireOp",EDGE,"E2.0.17.0"),sQuery(id+"F0.wireOp",EDGE,"E2.0.17.1"),sQuery(id+"F0.wireOp",EDGE,"E2.0.17.2"),sQuery(id+"F0.wireOp",EDGE,"E2.0.17.3"),sQuery(id+"F0.wireOp",EDGE,"E2.0.18.0"),sQuery(id+"F0.wireOp",EDGE,"E2.0.18.1"),sQuery(id+"F0.wireOp",EDGE,"E2.0.18.2"),sQuery(id+"F0.wireOp",EDGE,"E2.0.18.3"),sQuery(id+"F0.wireOp",EDGE,"E2.0.19.0"),sQuery(id+"F0.wireOp",EDGE,"E2.0.19.1"),sQuery(id+"F0.wireOp",EDGE,"E2.0.19.2"),sQuery(id+"F0.wireOp",EDGE,"E2.0.19.3"),sQuery(id+"F0.wireOp",EDGE,"E2.0.20.0"),sQuery(id+"F0.wireOp",EDGE,"E2.0.20.1"),sQuery(id+"F0.wireOp",EDGE,"E2.0.20.2"),sQuery(id+"F0.wireOp",EDGE,"E2.0.20.3"),sQuery(id+"F0.wireOp",EDGE,"E2.0.21.0"),sQuery(id+"F0.wireOp",EDGE,"E2.0.21.1"),sQuery(id+"F0.wireOp",EDGE,"E2.0.21.2"),sQuery(id+"F0.wireOp",EDGE,"E2.0.21.3"),sQuery(id+"F0.wireOp",EDGE,"E2.0.22.0"),sQuery(id+"F0.wireOp",EDGE,"E2.0.22.1"),sQuery(id+"F0.wireOp",EDGE,"E2.0.22.2"),sQuery(id+"F0.wireOp",EDGE,"E2.0.22.3"),sQuery(id+"F0.wireOp",EDGE,"E2.0.23.0"),sQuery(id+"F0.wireOp",EDGE,"E2.0.23.1"),sQuery(id+"F0.wireOp",EDGE,"E2.0.23.2"),sQuery(id+"F0.wireOp",EDGE,"E2.0.23.3"),sQuery(id+"F0.wireOp",EDGE,"E2.1.0.0"),sQuery(id+"F0.wireOp",EDGE,"E2.1.0.1"),sQuery(id+"F0.wireOp",EDGE,"E2.1.0.2"),sQuery(id+"F0.wireOp",EDGE,"E2.1.0.3"),sQuery(id+"F0.wireOp",EDGE,"E2.1.1.0"),sQuery(id+"F0.wireOp",EDGE,"E2.1.1.1"),sQuery(id+"F0.wireOp",EDGE,"E2.1.1.2"),sQuery(id+"F0.wireOp",EDGE,"E2.1.1.3"),sQuery(id+"F0.wireOp",EDGE,"E2.1.2.0"),sQuery(id+"F0.wireOp",EDGE,"E2.1.2.1"),sQuery(id+"F0.wireOp",EDGE,"E2.1.2.2"),sQuery(id+"F0.wireOp",EDGE,"E2.1.2.3"),sQuery(id+"F0.wireOp",EDGE,"E2.1.3.0"),sQuery(id+"F0.wireOp",EDGE,"E2.1.3.1"),sQuery(id+"F0.wireOp",EDGE,"E2.1.3.2"),sQuery(id+"F0.wireOp",EDGE,"E2.1.3.3"),sQuery(id+"F0.wireOp",EDGE,"E2.1.4.0"),sQuery(id+"F0.wireOp",EDGE,"E2.1.4.1"),sQuery(id+"F0.wireOp",EDGE,"E2.1.4.2"),sQuery(id+"F0.wireOp",EDGE,"E2.1.4.3"),sQuery(id+"F0.wireOp",EDGE,"E2.1.5.0"),sQuery(id+"F0.wireOp",EDGE,"E2.1.5.1"),sQuery(id+"F0.wireOp",EDGE,"E2.1.5.2"),sQuery(id+"F0.wireOp",EDGE,"E2.1.5.3"),sQuery(id+"F0.wireOp",EDGE,"E2.1.6.0"),sQuery(id+"F0.wireOp",EDGE,"E2.1.6.1"),sQuery(id+"F0.wireOp",EDGE,"E2.1.6.2"),sQuery(id+"F0.wireOp",EDGE,"E2.1.6.3"),sQuery(id+"F0.wireOp",EDGE,"E2.1.7.0"),sQuery(id+"F0.wireOp",EDGE,"E2.1.7.1"),sQuery(id+"F0.wireOp",EDGE,"E2.1.7.2"),sQuery(id+"F0.wireOp",EDGE,"E2.1.7.3"),sQuery(id+"F0.wireOp",EDGE,"E2.1.8.0"),sQuery(id+"F0.wireOp",EDGE,"E2.1.8.1"),sQuery(id+"F0.wireOp",EDGE,"E2.1.8.2"),sQuery(id+"F0.wireOp",EDGE,"E2.1.8.3"),sQuery(id+"F0.wireOp",EDGE,"E2.1.9.0"),sQuery(id+"F0.wireOp",EDGE,"E2.1.9.1"),sQuery(id+"F0.wireOp",EDGE,"E2.1.9.2"),sQuery(id+"F0.wireOp",EDGE,"E2.1.9.3"),sQuery(id+"F0.wireOp",EDGE,"E2.1.10.0"),sQuery(id+"F0.wireOp",EDGE,"E2.1.10.1"),sQuery(id+"F0.wireOp",EDGE,"E2.1.10.2"),sQuery(id+"F0.wireOp",EDGE,"E2.1.10.3"),sQuery(id+"F0.wireOp",EDGE,"E2.1.11.0"),sQuery(id+"F0.wireOp",EDGE,"E2.1.11.1"),sQuery(id+"F0.wireOp",EDGE,"E2.1.11.2"),sQuery(id+"F0.wireOp",EDGE,"E2.1.11.3"),sQuery(id+"F0.wireOp",EDGE,"E2.1.12.0"),sQuery(id+"F0.wireOp",EDGE,"E2.1.12.1"),sQuery(id+"F0.wireOp",EDGE,"E2.1.12.2"),sQuery(id+"F0.wireOp",EDGE,"E2.1.12.3"),sQuery(id+"F0.wireOp",EDGE,"E2.1.13.0"),sQuery(id+"F0.wireOp",EDGE,"E2.1.13.1"),sQuery(id+"F0.wireOp",EDGE,"E2.1.13.2"),sQuery(id+"F0.wireOp",EDGE,"E2.1.13.3"),sQuery(id+"F0.wireOp",EDGE,"E2.1.14.0"),sQuery(id+"F0.wireOp",EDGE,"E2.1.14.1"),sQuery(id+"F0.wireOp",EDGE,"E2.1.14.2"),sQuery(id+"F0.wireOp",EDGE,"E2.1.14.3"),sQuery(id+"F0.wireOp",EDGE,"E2.1.15.0"),sQuery(id+"F0.wireOp",EDGE,"E2.1.15.1"),sQuery(id+"F0.wireOp",EDGE,"E2.1.15.2"),sQuery(id+"F0.wireOp",EDGE,"E2.1.15.3"),sQuery(id+"F0.wireOp",EDGE,"E2.1.16.0"),sQuery(id+"F0.wireOp",EDGE,"E2.1.16.1"),sQuery(id+"F0.wireOp",EDGE,"E2.1.16.2"),sQuery(id+"F0.wireOp",EDGE,"E2.1.16.3"),sQuery(id+"F0.wireOp",EDGE,"E2.1.17.0"),sQuery(id+"F0.wireOp",EDGE,"E2.1.17.1"),sQuery(id+"F0.wireOp",EDGE,"E2.1.17.2"),sQuery(id+"F0.wireOp",EDGE,"E2.1.17.3"),sQuery(id+"F0.wireOp",EDGE,"E2.1.18.0"),sQuery(id+"F0.wireOp",EDGE,"E2.1.18.1"),sQuery(id+"F0.wireOp",EDGE,"E2.1.18.2"),sQuery(id+"F0.wireOp",EDGE,"E2.1.18.3"),sQuery(id+"F0.wireOp",EDGE,"E2.1.19.0"),sQuery(id+"F0.wireOp",EDGE,"E2.1.19.1"),sQuery(id+"F0.wireOp",EDGE,"E2.1.19.2"),sQuery(id+"F0.wireOp",EDGE,"E2.1.19.3"),sQuery(id+"F0.wireOp",EDGE,"E2.1.20.0"),sQuery(id+"F0.wireOp",EDGE,"E2.1.20.1"),sQuery(id+"F0.wireOp",EDGE,"E2.1.20.2"),sQuery(id+"F0.wireOp",EDGE,"E2.1.20.3"),sQuery(id+"F0.wireOp",EDGE,"E2.1.21.0"),sQuery(id+"F0.wireOp",EDGE,"E2.1.21.1"),sQuery(id+"F0.wireOp",EDGE,"E2.1.21.2"),sQuery(id+"F0.wireOp",EDGE,"E2.1.21.3"),sQuery(id+"F0.wireOp",EDGE,"E2.1.22.0"),sQuery(id+"F0.wireOp",EDGE,"E2.1.22.1"),sQuery(id+"F0.wireOp",EDGE,"E2.1.22.2"),sQuery(id+"F0.wireOp",EDGE,"E2.1.22.3"),sQuery(id+"F0.wireOp",EDGE,"E2.1.23.0"),sQuery(id+"F0.wireOp",EDGE,"E2.1.23.1"),sQuery(id+"F0.wireOp",EDGE,"E2.1.23.2"),sQuery(id+"F0.wireOp",EDGE,"E2.1.23.3"),sQuery(id+"F0.wireOp",EDGE,"E2.2.0.0"),sQuery(id+"F0.wireOp",EDGE,"E2.2.0.1"),sQuery(id+"F0.wireOp",EDGE,"E2.2.0.2"),sQuery(id+"F0.wireOp",EDGE,"E2.2.0.3"),sQuery(id+"F0.wireOp",EDGE,"E2.2.1.0"),sQuery(id+"F0.wireOp",EDGE,"E2.2.1.1"),sQuery(id+"F0.wireOp",EDGE,"E2.2.1.2"),sQuery(id+"F0.wireOp",EDGE,"E2.2.1.3"),sQuery(id+"F0.wireOp",EDGE,"E2.2.2.0"),sQuery(id+"F0.wireOp",EDGE,"E2.2.2.1"),sQuery(id+"F0.wireOp",EDGE,"E2.2.2.2"),sQuery(id+"F0.wireOp",EDGE,"E2.2.2.3"),sQuery(id+"F0.wireOp",EDGE,"E2.2.3.0"),sQuery(id+"F0.wireOp",EDGE,"E2.2.3.1"),sQuery(id+"F0.wireOp",EDGE,"E2.2.3.2"),sQuery(id+"F0.wireOp",EDGE,"E2.2.3.3"),sQuery(id+"F0.wireOp",EDGE,"E2.2.4.0"),sQuery(id+"F0.wireOp",EDGE,"E2.2.4.1"),sQuery(id+"F0.wireOp",EDGE,"E2.2.4.2"),sQuery(id+"F0.wireOp",EDGE,"E2.2.4.3"),sQuery(id+"F0.wireOp",EDGE,"E2.2.5.0"),sQuery(id+"F0.wireOp",EDGE,"E2.2.5.1"),sQuery(id+"F0.wireOp",EDGE,"E2.2.5.2"),sQuery(id+"F0.wireOp",EDGE,"E2.2.5.3"),sQuery(id+"F0.wireOp",EDGE,"E2.2.6.0"),sQuery(id+"F0.wireOp",EDGE,"E2.2.6.1"),sQuery(id+"F0.wireOp",EDGE,"E2.2.6.2"),sQuery(id+"F0.wireOp",EDGE,"E2.2.6.3"),sQuery(id+"F0.wireOp",EDGE,"E2.2.7.0"),sQuery(id+"F0.wireOp",EDGE,"E2.2.7.1"),sQuery(id+"F0.wireOp",EDGE,"E2.2.7.2"),sQuery(id+"F0.wireOp",EDGE,"E2.2.7.3"),sQuery(id+"F0.wireOp",EDGE,"E2.2.8.0"),sQuery(id+"F0.wireOp",EDGE,"E2.2.8.1"),sQuery(id+"F0.wireOp",EDGE,"E2.2.8.2"),sQuery(id+"F0.wireOp",EDGE,"E2.2.8.3"),sQuery(id+"F0.wireOp",EDGE,"E2.2.9.0"),sQuery(id+"F0.wireOp",EDGE,"E2.2.9.1"),sQuery(id+"F0.wireOp",EDGE,"E2.2.9.2"),sQuery(id+"F0.wireOp",EDGE,"E2.2.9.3"),sQuery(id+"F0.wireOp",EDGE,"E2.2.10.0"),sQuery(id+"F0.wireOp",EDGE,"E2.2.10.1"),sQuery(id+"F0.wireOp",EDGE,"E2.2.10.2"),sQuery(id+"F0.wireOp",EDGE,"E2.2.10.3"),sQuery(id+"F0.wireOp",EDGE,"E2.2.11.0"),sQuery(id+"F0.wireOp",EDGE,"E2.2.11.1"),sQuery(id+"F0.wireOp",EDGE,"E2.2.11.2"),sQuery(id+"F0.wireOp",EDGE,"E2.2.11.3"),sQuery(id+"F0.wireOp",EDGE,"E2.2.12.0"),sQuery(id+"F0.wireOp",EDGE,"E2.2.12.1"),sQuery(id+"F0.wireOp",EDGE,"E2.2.12.2"),sQuery(id+"F0.wireOp",EDGE,"E2.2.12.3"),sQuery(id+"F0.wireOp",EDGE,"E2.2.13.0"),sQuery(id+"F0.wireOp",EDGE,"E2.2.13.1"),sQuery(id+"F0.wireOp",EDGE,"E2.2.13.2"),sQuery(id+"F0.wireOp",EDGE,"E2.2.13.3"),sQuery(id+"F0.wireOp",EDGE,"E2.2.14.0"),sQuery(id+"F0.wireOp",EDGE,"E2.2.14.1"),sQuery(id+"F0.wireOp",EDGE,"E2.2.14.2"),sQuery(id+"F0.wireOp",EDGE,"E2.2.14.3"),sQuery(id+"F0.wireOp",EDGE,"E2.2.15.0"),sQuery(id+"F0.wireOp",EDGE,"E2.2.15.1"),sQuery(id+"F0.wireOp",EDGE,"E2.2.15.2"),sQuery(id+"F0.wireOp",EDGE,"E2.2.15.3"),sQuery(id+"F0.wireOp",EDGE,"E2.2.16.0"),sQuery(id+"F0.wireOp",EDGE,"E2.2.16.1"),sQuery(id+"F0.wireOp",EDGE,"E2.2.16.2"),sQuery(id+"F0.wireOp",EDGE,"E2.2.16.3"),sQuery(id+"F0.wireOp",EDGE,"E2.2.17.0"),sQuery(id+"F0.wireOp",EDGE,"E2.2.17.1"),sQuery(id+"F0.wireOp",EDGE,"E2.2.17.2"),sQuery(id+"F0.wireOp",EDGE,"E2.2.17.3"),sQuery(id+"F0.wireOp",EDGE,"E2.2.18.0"),sQuery(id+"F0.wireOp",EDGE,"E2.2.18.1"),sQuery(id+"F0.wireOp",EDGE,"E2.2.18.2"),sQuery(id+"F0.wireOp",EDGE,"E2.2.18.3"),sQuery(id+"F0.wireOp",EDGE,"E2.2.19.0"),sQuery(id+"F0.wireOp",EDGE,"E2.2.19.1"),sQuery(id+"F0.wireOp",EDGE,"E2.2.19.2"),sQuery(id+"F0.wireOp",EDGE,"E2.2.19.3"),sQuery(id+"F0.wireOp",EDGE,"E2.2.20.0"),sQuery(id+"F0.wireOp",EDGE,"E2.2.20.1"),sQuery(id+"F0.wireOp",EDGE,"E2.2.20.2"),sQuery(id+"F0.wireOp",EDGE,"E2.2.20.3"),sQuery(id+"F0.wireOp",EDGE,"E2.2.21.0"),sQuery(id+"F0.wireOp",EDGE,"E2.2.21.1"),sQuery(id+"F0.wireOp",EDGE,"E2.2.21.2"),sQuery(id+"F0.wireOp",EDGE,"E2.2.21.3"),sQuery(id+"F0.wireOp",EDGE,"E2.2.22.0"),sQuery(id+"F0.wireOp",EDGE,"E2.2.22.1"),sQuery(id+"F0.wireOp",EDGE,"E2.2.22.2"),sQuery(id+"F0.wireOp",EDGE,"E2.2.22.3"),sQuery(id+"F0.wireOp",EDGE,"E2.2.23.0"),sQuery(id+"F0.wireOp",EDGE,"E2.2.23.1"),sQuery(id+"F0.wireOp",EDGE,"E2.2.23.2"),sQuery(id+"F0.wireOp",EDGE,"E2.2.23.3"),sQuery(id+"F0.wireOp",EDGE,"E2.3.0.0"),sQuery(id+"F0.wireOp",EDGE,"E2.3.0.1"),sQuery(id+"F0.wireOp",EDGE,"E2.3.0.2"),sQuery(id+"F0.wireOp",EDGE,"E2.3.0.3"),sQuery(id+"F0.wireOp",EDGE,"E2.3.1.0"),sQuery(id+"F0.wireOp",EDGE,"E2.3.1.1"),sQuery(id+"F0.wireOp",EDGE,"E2.3.1.2"),sQuery(id+"F0.wireOp",EDGE,"E2.3.1.3"),sQuery(id+"F0.wireOp",EDGE,"E2.3.2.0"),sQuery(id+"F0.wireOp",EDGE,"E2.3.2.1"),sQuery(id+"F0.wireOp",EDGE,"E2.3.2.2"),sQuery(id+"F0.wireOp",EDGE,"E2.3.2.3"),sQuery(id+"F0.wireOp",EDGE,"E2.3.3.0"),sQuery(id+"F0.wireOp",EDGE,"E2.3.3.1"),sQuery(id+"F0.wireOp",EDGE,"E2.3.3.2"),sQuery(id+"F0.wireOp",EDGE,"E2.3.3.3"),sQuery(id+"F0.wireOp",EDGE,"E2.3.4.0"),sQuery(id+"F0.wireOp",EDGE,"E2.3.4.1"),sQuery(id+"F0.wireOp",EDGE,"E2.3.4.2"),sQuery(id+"F0.wireOp",EDGE,"E2.3.4.3"),sQuery(id+"F0.wireOp",EDGE,"E2.3.5.0"),sQuery(id+"F0.wireOp",EDGE,"E2.3.5.1"),sQuery(id+"F0.wireOp",EDGE,"E2.3.5.2"),sQuery(id+"F0.wireOp",EDGE,"E2.3.5.3"),sQuery(id+"F0.wireOp",EDGE,"E2.3.6.0"),sQuery(id+"F0.wireOp",EDGE,"E2.3.6.1"),sQuery(id+"F0.wireOp",EDGE,"E2.3.6.2"),sQuery(id+"F0.wireOp",EDGE,"E2.3.6.3"),sQuery(id+"F0.wireOp",EDGE,"E2.3.7.0"),sQuery(id+"F0.wireOp",EDGE,"E2.3.7.1"),sQuery(id+"F0.wireOp",EDGE,"E2.3.7.2"),sQuery(id+"F0.wireOp",EDGE,"E2.3.7.3"),sQuery(id+"F0.wireOp",EDGE,"E2.3.8.0"),sQuery(id+"F0.wireOp",EDGE,"E2.3.8.1"),sQuery(id+"F0.wireOp",EDGE,"E2.3.8.2"),sQuery(id+"F0.wireOp",EDGE,"E2.3.8.3"),sQuery(id+"F0.wireOp",EDGE,"E2.3.9.0"),sQuery(id+"F0.wireOp",EDGE,"E2.3.9.1"),sQuery(id+"F0.wireOp",EDGE,"E2.3.9.2"),sQuery(id+"F0.wireOp",EDGE,"E2.3.9.3"),sQuery(id+"F0.wireOp",EDGE,"E2.3.10.0"),sQuery(id+"F0.wireOp",EDGE,"E2.3.10.1"),sQuery(id+"F0.wireOp",EDGE,"E2.3.10.2"),sQuery(id+"F0.wireOp",EDGE,"E2.3.10.3"),sQuery(id+"F0.wireOp",EDGE,"E2.3.11.0"),sQuery(id+"F0.wireOp",EDGE,"E2.3.11.1"),sQuery(id+"F0.wireOp",EDGE,"E2.3.11.2"),sQuery(id+"F0.wireOp",EDGE,"E2.3.11.3"),sQuery(id+"F0.wireOp",EDGE,"E2.3.12.0"),sQuery(id+"F0.wireOp",EDGE,"E2.3.12.1"),sQuery(id+"F0.wireOp",EDGE,"E2.3.12.2"),sQuery(id+"F0.wireOp",EDGE,"E2.3.12.3"),sQuery(id+"F0.wireOp",EDGE,"E2.3.13.0"),sQuery(id+"F0.wireOp",EDGE,"E2.3.13.1"),sQuery(id+"F0.wireOp",EDGE,"E2.3.13.2"),sQuery(id+"F0.wireOp",EDGE,"E2.3.13.3"),sQuery(id+"F0.wireOp",EDGE,"E2.3.14.0"),sQuery(id+"F0.wireOp",EDGE,"E2.3.14.1"),sQuery(id+"F0.wireOp",EDGE,"E2.3.14.2"),sQuery(id+"F0.wireOp",EDGE,"E2.3.14.3"),sQuery(id+"F0.wireOp",EDGE,"E2.3.15.0"),sQuery(id+"F0.wireOp",EDGE,"E2.3.15.1"),sQuery(id+"F0.wireOp",EDGE,"E2.3.15.2"),sQuery(id+"F0.wireOp",EDGE,"E2.3.15.3"),sQuery(id+"F0.wireOp",EDGE,"E2.3.16.0"),sQuery(id+"F0.wireOp",EDGE,"E2.3.16.1"),sQuery(id+"F0.wireOp",EDGE,"E2.3.16.2"),sQuery(id+"F0.wireOp",EDGE,"E2.3.16.3"),sQuery(id+"F0.wireOp",EDGE,"E2.3.17.0"),sQuery(id+"F0.wireOp",EDGE,"E2.3.17.1"),sQuery(id+"F0.wireOp",EDGE,"E2.3.17.2"),sQuery(id+"F0.wireOp",EDGE,"E2.3.17.3"),sQuery(id+"F0.wireOp",EDGE,"E2.3.18.0"),sQuery(id+"F0.wireOp",EDGE,"E2.3.18.1"),sQuery(id+"F0.wireOp",EDGE,"E2.3.18.2"),sQuery(id+"F0.wireOp",EDGE,"E2.3.18.3"),sQuery(id+"F0.wireOp",EDGE,"E2.3.19.0"),sQuery(id+"F0.wireOp",EDGE,"E2.3.19.1"),sQuery(id+"F0.wireOp",EDGE,"E2.3.19.2"),sQuery(id+"F0.wireOp",EDGE,"E2.3.19.3"),sQuery(id+"F0.wireOp",EDGE,"E2.3.20.0"),sQuery(id+"F0.wireOp",EDGE,"E2.3.20.1"),sQuery(id+"F0.wireOp",EDGE,"E2.3.20.2"),sQuery(id+"F0.wireOp",EDGE,"E2.3.20.3"),sQuery(id+"F0.wireOp",EDGE,"E2.3.21.0"),sQuery(id+"F0.wireOp",EDGE,"E2.3.21.1"),sQuery(id+"F0.wireOp",EDGE,"E2.3.21.2"),sQuery(id+"F0.wireOp",EDGE,"E2.3.21.3"),sQuery(id+"F0.wireOp",EDGE,"E2.3.22.0"),sQuery(id+"F0.wireOp",EDGE,"E2.3.22.1"),sQuery(id+"F0.wireOp",EDGE,"E2.3.22.2"),sQuery(id+"F0.wireOp",EDGE,"E2.3.22.3"),sQuery(id+"F0.wireOp",EDGE,"E2.3.23.0"),sQuery(id+"F0.wireOp",EDGE,"E2.3.23.1"),sQuery(id+"F0.wireOp",EDGE,"E2.3.23.2"),sQuery(id+"F0.wireOp",EDGE,"E2.3.23.3"),sQuery(id+"F0.wireOp",EDGE,"E2.4.0.0"),sQuery(id+"F0.wireOp",EDGE,"E2.4.0.1"),sQuery(id+"F0.wireOp",EDGE,"E2.4.0.2"),sQuery(id+"F0.wireOp",EDGE,"E2.4.0.3"),sQuery(id+"F0.wireOp",EDGE,"E2.4.1.0"),sQuery(id+"F0.wireOp",EDGE,"E2.4.1.1"),sQuery(id+"F0.wireOp",EDGE,"E2.4.1.2"),sQuery(id+"F0.wireOp",EDGE,"E2.4.1.3"),sQuery(id+"F0.wireOp",EDGE,"E2.4.2.0"),sQuery(id+"F0.wireOp",EDGE,"E2.4.2.1"),sQuery(id+"F0.wireOp",EDGE,"E2.4.2.2"),sQuery(id+"F0.wireOp",EDGE,"E2.4.2.3"),sQuery(id+"F0.wireOp",EDGE,"E2.4.3.0"),sQuery(id+"F0.wireOp",EDGE,"E2.4.3.1"),sQuery(id+"F0.wireOp",EDGE,"E2.4.3.2"),sQuery(id+"F0.wireOp",EDGE,"E2.4.3.3"),sQuery(id+"F0.wireOp",EDGE,"E2.4.4.0"),sQuery(id+"F0.wireOp",EDGE,"E2.4.4.1"),sQuery(id+"F0.wireOp",EDGE,"E2.4.4.2"),sQuery(id+"F0.wireOp",EDGE,"E2.4.4.3"),sQuery(id+"F0.wireOp",EDGE,"E2.4.5.0"),sQuery(id+"F0.wireOp",EDGE,"E2.4.5.1"),sQuery(id+"F0.wireOp",EDGE,"E2.4.5.2"),sQuery(id+"F0.wireOp",EDGE,"E2.4.5.3"),sQuery(id+"F0.wireOp",EDGE,"E2.4.6.0"),sQuery(id+"F0.wireOp",EDGE,"E2.4.6.1"),sQuery(id+"F0.wireOp",EDGE,"E2.4.6.2"),sQuery(id+"F0.wireOp",EDGE,"E2.4.6.3"),sQuery(id+"F0.wireOp",EDGE,"E2.4.7.0"),sQuery(id+"F0.wireOp",EDGE,"E2.4.7.1"),sQuery(id+"F0.wireOp",EDGE,"E2.4.7.2"),sQuery(id+"F0.wireOp",EDGE,"E2.4.7.3"),sQuery(id+"F0.wireOp",EDGE,"E2.4.8.0"),sQuery(id+"F0.wireOp",EDGE,"E2.4.8.1"),sQuery(id+"F0.wireOp",EDGE,"E2.4.8.2"),sQuery(id+"F0.wireOp",EDGE,"E2.4.8.3"),sQuery(id+"F0.wireOp",EDGE,"E2.4.9.0"),sQuery(id+"F0.wireOp",EDGE,"E2.4.9.1"),sQuery(id+"F0.wireOp",EDGE,"E2.4.9.2"),sQuery(id+"F0.wireOp",EDGE,"E2.4.9.3"),sQuery(id+"F0.wireOp",EDGE,"E2.4.10.0"),sQuery(id+"F0.wireOp",EDGE,"E2.4.10.1"),sQuery(id+"F0.wireOp",EDGE,"E2.4.10.2"),sQuery(id+"F0.wireOp",EDGE,"E2.4.10.3"),sQuery(id+"F0.wireOp",EDGE,"E2.4.11.0"),sQuery(id+"F0.wireOp",EDGE,"E2.4.11.1"),sQuery(id+"F0.wireOp",EDGE,"E2.4.11.2"),sQuery(id+"F0.wireOp",EDGE,"E2.4.11.3"),sQuery(id+"F0.wireOp",EDGE,"E2.4.12.0"),sQuery(id+"F0.wireOp",EDGE,"E2.4.12.1"),sQuery(id+"F0.wireOp",EDGE,"E2.4.12.2"),sQuery(id+"F0.wireOp",EDGE,"E2.4.12.3"),sQuery(id+"F0.wireOp",EDGE,"E2.4.13.0"),sQuery(id+"F0.wireOp",EDGE,"E2.4.13.1"),sQuery(id+"F0.wireOp",EDGE,"E2.4.13.2"),sQuery(id+"F0.wireOp",EDGE,"E2.4.13.3"),sQuery(id+"F0.wireOp",EDGE,"E2.4.14.0"),sQuery(id+"F0.wireOp",EDGE,"E2.4.14.1"),sQuery(id+"F0.wireOp",EDGE,"E2.4.14.2"),sQuery(id+"F0.wireOp",EDGE,"E2.4.14.3"),sQuery(id+"F0.wireOp",EDGE,"E2.4.15.0"),sQuery(id+"F0.wireOp",EDGE,"E2.4.15.1"),sQuery(id+"F0.wireOp",EDGE,"E2.4.15.2"),sQuery(id+"F0.wireOp",EDGE,"E2.4.15.3"),sQuery(id+"F0.wireOp",EDGE,"E2.4.16.0"),sQuery(id+"F0.wireOp",EDGE,"E2.4.16.1"),sQuery(id+"F0.wireOp",EDGE,"E2.4.16.2"),sQuery(id+"F0.wireOp",EDGE,"E2.4.16.3"),sQuery(id+"F0.wireOp",EDGE,"E2.4.17.0"),sQuery(id+"F0.wireOp",EDGE,"E2.4.17.1"),sQuery(id+"F0.wireOp",EDGE,"E2.4.17.2"),sQuery(id+"F0.wireOp",EDGE,"E2.4.17.3"),sQuery(id+"F0.wireOp",EDGE,"E2.4.18.0"),sQuery(id+"F0.wireOp",EDGE,"E2.4.18.1"),sQuery(id+"F0.wireOp",EDGE,"E2.4.18.2"),sQuery(id+"F0.wireOp",EDGE,"E2.4.18.3"),sQuery(id+"F0.wireOp",EDGE,"E2.4.19.0"),sQuery(id+"F0.wireOp",EDGE,"E2.4.19.1"),sQuery(id+"F0.wireOp",EDGE,"E2.4.19.2"),sQuery(id+"F0.wireOp",EDGE,"E2.4.19.3"),sQuery(id+"F0.wireOp",EDGE,"E2.4.20.0"),sQuery(id+"F0.wireOp",EDGE,"E2.4.20.1"),sQuery(id+"F0.wireOp",EDGE,"E2.4.20.2"),sQuery(id+"F0.wireOp",EDGE,"E2.4.20.3"),sQuery(id+"F0.wireOp",EDGE,"E2.4.21.0"),sQuery(id+"F0.wireOp",EDGE,"E2.4.21.1"),sQuery(id+"F0.wireOp",EDGE,"E2.4.21.2"),sQuery(id+"F0.wireOp",EDGE,"E2.4.21.3"),sQuery(id+"F0.wireOp",EDGE,"E2.4.22.0"),sQuery(id+"F0.wireOp",EDGE,"E2.4.22.1"),sQuery(id+"F0.wireOp",EDGE,"E2.4.22.2"),sQuery(id+"F0.wireOp",EDGE,"E2.4.22.3"),sQuery(id+"F0.wireOp",EDGE,"E2.4.23.0"),sQuery(id+"F0.wireOp",EDGE,"E2.4.23.1"),sQuery(id+"F0.wireOp",EDGE,"E2.4.23.2"),sQuery(id+"F0.wireOp",EDGE,"E2.4.23.3"),sQuery(id+"F0.wireOp",EDGE,"E2.5.0.0"),sQuery(id+"F0.wireOp",EDGE,"E2.5.0.1"),sQuery(id+"F0.wireOp",EDGE,"E2.5.0.2"),sQuery(id+"F0.wireOp",EDGE,"E2.5.0.3"),sQuery(id+"F0.wireOp",EDGE,"E2.5.1.0"),sQuery(id+"F0.wireOp",EDGE,"E2.5.1.1"),sQuery(id+"F0.wireOp",EDGE,"E2.5.1.2"),sQuery(id+"F0.wireOp",EDGE,"E2.5.1.3"),sQuery(id+"F0.wireOp",EDGE,"E2.5.2.0"),sQuery(id+"F0.wireOp",EDGE,"E2.5.2.1"),sQuery(id+"F0.wireOp",EDGE,"E2.5.2.2"),sQuery(id+"F0.wireOp",EDGE,"E2.5.2.3"),sQuery(id+"F0.wireOp",EDGE,"E2.5.3.0"),sQuery(id+"F0.wireOp",EDGE,"E2.5.3.1"),sQuery(id+"F0.wireOp",EDGE,"E2.5.3.2"),sQuery(id+"F0.wireOp",EDGE,"E2.5.3.3"),sQuery(id+"F0.wireOp",EDGE,"E2.5.4.0"),sQuery(id+"F0.wireOp",EDGE,"E2.5.4.1"),sQuery(id+"F0.wireOp",EDGE,"E2.5.4.2"),sQuery(id+"F0.wireOp",EDGE,"E2.5.4.3"),sQuery(id+"F0.wireOp",EDGE,"E2.5.5.0"),sQuery(id+"F0.wireOp",EDGE,"E2.5.5.1"),sQuery(id+"F0.wireOp",EDGE,"E2.5.5.2"),sQuery(id+"F0.wireOp",EDGE,"E2.5.5.3"),sQuery(id+"F0.wireOp",EDGE,"E2.5.6.0"),sQuery(id+"F0.wireOp",EDGE,"E2.5.6.1"),sQuery(id+"F0.wireOp",EDGE,"E2.5.6.2"),sQuery(id+"F0.wireOp",EDGE,"E2.5.6.3"),sQuery(id+"F0.wireOp",EDGE,"E2.5.7.0"),sQuery(id+"F0.wireOp",EDGE,"E2.5.7.1"),sQuery(id+"F0.wireOp",EDGE,"E2.5.7.2"),sQuery(id+"F0.wireOp",EDGE,"E2.5.7.3"),sQuery(id+"F0.wireOp",EDGE,"E2.5.8.0"),sQuery(id+"F0.wireOp",EDGE,"E2.5.8.1"),sQuery(id+"F0.wireOp",EDGE,"E2.5.8.2"),sQuery(id+"F0.wireOp",EDGE,"E2.5.8.3"),sQuery(id+"F0.wireOp",EDGE,"E2.5.9.0"),sQuery(id+"F0.wireOp",EDGE,"E2.5.9.1"),sQuery(id+"F0.wireOp",EDGE,"E2.5.9.2"),sQuery(id+"F0.wireOp",EDGE,"E2.5.9.3"),sQuery(id+"F0.wireOp",EDGE,"E2.5.10.0"),sQuery(id+"F0.wireOp",EDGE,"E2.5.10.1"),sQuery(id+"F0.wireOp",EDGE,"E2.5.10.2"),sQuery(id+"F0.wireOp",EDGE,"E2.5.10.3"),sQuery(id+"F0.wireOp",EDGE,"E2.5.11.0"),sQuery(id+"F0.wireOp",EDGE,"E2.5.11.1"),sQuery(id+"F0.wireOp",EDGE,"E2.5.11.2"),sQuery(id+"F0.wireOp",EDGE,"E2.5.11.3"),sQuery(id+"F0.wireOp",EDGE,"E2.5.12.0"),sQuery(id+"F0.wireOp",EDGE,"E2.5.12.1"),sQuery(id+"F0.wireOp",EDGE,"E2.5.12.2"),sQuery(id+"F0.wireOp",EDGE,"E2.5.12.3"),sQuery(id+"F0.wireOp",EDGE,"E2.5.13.0"),sQuery(id+"F0.wireOp",EDGE,"E2.5.13.1"),sQuery(id+"F0.wireOp",EDGE,"E2.5.13.2"),sQuery(id+"F0.wireOp",EDGE,"E2.5.13.3"),sQuery(id+"F0.wireOp",EDGE,"E2.5.14.0"),sQuery(id+"F0.wireOp",EDGE,"E2.5.14.1"),sQuery(id+"F0.wireOp",EDGE,"E2.5.14.2"),sQuery(id+"F0.wireOp",EDGE,"E2.5.14.3"),sQuery(id+"F0.wireOp",EDGE,"E2.5.15.0"),sQuery(id+"F0.wireOp",EDGE,"E2.5.15.1"),sQuery(id+"F0.wireOp",EDGE,"E2.5.15.2"),sQuery(id+"F0.wireOp",EDGE,"E2.5.15.3"),sQuery(id+"F0.wireOp",EDGE,"E2.5.16.0"),sQuery(id+"F0.wireOp",EDGE,"E2.5.16.1"),sQuery(id+"F0.wireOp",EDGE,"E2.5.16.2"),sQuery(id+"F0.wireOp",EDGE,"E2.5.16.3"),sQuery(id+"F0.wireOp",EDGE,"E2.5.17.0"),sQuery(id+"F0.wireOp",EDGE,"E2.5.17.1"),sQuery(id+"F0.wireOp",EDGE,"E2.5.17.2"),sQuery(id+"F0.wireOp",EDGE,"E2.5.17.3"),sQuery(id+"F0.wireOp",EDGE,"E2.5.18.0"),sQuery(id+"F0.wireOp",EDGE,"E2.5.18.1"),sQuery(id+"F0.wireOp",EDGE,"E2.5.18.2"),sQuery(id+"F0.wireOp",EDGE,"E2.5.18.3"),sQuery(id+"F0.wireOp",EDGE,"E2.5.19.0"),sQuery(id+"F0.wireOp",EDGE,"E2.5.19.1"),sQuery(id+"F0.wireOp",EDGE,"E2.5.19.2"),sQuery(id+"F0.wireOp",EDGE,"E2.5.19.3"),sQuery(id+"F0.wireOp",EDGE,"E2.5.20.0"),sQuery(id+"F0.wireOp",EDGE,"E2.5.20.1"),sQuery(id+"F0.wireOp",EDGE,"E2.5.20.2"),sQuery(id+"F0.wireOp",EDGE,"E2.5.20.3"),sQuery(id+"F0.wireOp",EDGE,"E2.5.21.0"),sQuery(id+"F0.wireOp",EDGE,"E2.5.21.1"),sQuery(id+"F0.wireOp",EDGE,"E2.5.21.2"),sQuery(id+"F0.wireOp",EDGE,"E2.5.21.3"),sQuery(id+"F0.wireOp",EDGE,"E2.5.22.0"),sQuery(id+"F0.wireOp",EDGE,"E2.5.22.1"),sQuery(id+"F0.wireOp",EDGE,"E2.5.22.2"),sQuery(id+"F0.wireOp",EDGE,"E2.5.22.3"),sQuery(id+"F0.wireOp",EDGE,"E2.5.23.0"),sQuery(id+"F0.wireOp",EDGE,"E2.5.23.1"),sQuery(id+"F0.wireOp",EDGE,"E2.5.23.2"),sQuery(id+"F0.wireOp",EDGE,"E2.5.23.3"),sQuery(id+"F0.wireOp",EDGE,"E2.6.0.0"),sQuery(id+"F0.wireOp",EDGE,"E2.6.0.1"),sQuery(id+"F0.wireOp",EDGE,"E2.6.0.2"),sQuery(id+"F0.wireOp",EDGE,"E2.6.0.3"),sQuery(id+"F0.wireOp",EDGE,"E2.6.1.0"),sQuery(id+"F0.wireOp",EDGE,"E2.6.1.1"),sQuery(id+"F0.wireOp",EDGE,"E2.6.1.2"),sQuery(id+"F0.wireOp",EDGE,"E2.6.1.3"),sQuery(id+"F0.wireOp",EDGE,"E2.6.2.0"),sQuery(id+"F0.wireOp",EDGE,"E2.6.2.1"),sQuery(id+"F0.wireOp",EDGE,"E2.6.2.2"),sQuery(id+"F0.wireOp",EDGE,"E2.6.2.3"),sQuery(id+"F0.wireOp",EDGE,"E2.6.3.0"),sQuery(id+"F0.wireOp",EDGE,"E2.6.3.1"),sQuery(id+"F0.wireOp",EDGE,"E2.6.3.2"),sQuery(id+"F0.wireOp",EDGE,"E2.6.3.3"),sQuery(id+"F0.wireOp",EDGE,"E2.6.4.0"),sQuery(id+"F0.wireOp",EDGE,"E2.6.4.1"),sQuery(id+"F0.wireOp",EDGE,"E2.6.4.2"),sQuery(id+"F0.wireOp",EDGE,"E2.6.4.3"),sQuery(id+"F0.wireOp",EDGE,"E2.6.5.0"),sQuery(id+"F0.wireOp",EDGE,"E2.6.5.1"),sQuery(id+"F0.wireOp",EDGE,"E2.6.5.2"),sQuery(id+"F0.wireOp",EDGE,"E2.6.5.3"),sQuery(id+"F0.wireOp",EDGE,"E2.6.6.0"),sQuery(id+"F0.wireOp",EDGE,"E2.6.6.1"),sQuery(id+"F0.wireOp",EDGE,"E2.6.6.2"),sQuery(id+"F0.wireOp",EDGE,"E2.6.6.3"),sQuery(id+"F0.wireOp",EDGE,"E2.6.7.0"),sQuery(id+"F0.wireOp",EDGE,"E2.6.7.1"),sQuery(id+"F0.wireOp",EDGE,"E2.6.7.2"),sQuery(id+"F0.wireOp",EDGE,"E2.6.7.3"),sQuery(id+"F0.wireOp",EDGE,"E2.6.8.0"),sQuery(id+"F0.wireOp",EDGE,"E2.6.8.1"),sQuery(id+"F0.wireOp",EDGE,"E2.6.8.2"),sQuery(id+"F0.wireOp",EDGE,"E2.6.8.3"),sQuery(id+"F0.wireOp",EDGE,"E2.6.9.0"),sQuery(id+"F0.wireOp",EDGE,"E2.6.9.1"),sQuery(id+"F0.wireOp",EDGE,"E2.6.9.2"),sQuery(id+"F0.wireOp",EDGE,"E2.6.9.3"),sQuery(id+"F0.wireOp",EDGE,"E2.6.10.0"),sQuery(id+"F0.wireOp",EDGE,"E2.6.10.1"),sQuery(id+"F0.wireOp",EDGE,"E2.6.10.2"),sQuery(id+"F0.wireOp",EDGE,"E2.6.10.3"),sQuery(id+"F0.wireOp",EDGE,"E2.6.11.0"),sQuery(id+"F0.wireOp",EDGE,"E2.6.11.1"),sQuery(id+"F0.wireOp",EDGE,"E2.6.11.2"),sQuery(id+"F0.wireOp",EDGE,"E2.6.11.3"),sQuery(id+"F0.wireOp",EDGE,"E2.6.12.0"),sQuery(id+"F0.wireOp",EDGE,"E2.6.12.1"),sQuery(id+"F0.wireOp",EDGE,"E2.6.12.2"),sQuery(id+"F0.wireOp",EDGE,"E2.6.12.3"),sQuery(id+"F0.wireOp",EDGE,"E2.6.13.0"),sQuery(id+"F0.wireOp",EDGE,"E2.6.13.1"),sQuery(id+"F0.wireOp",EDGE,"E2.6.13.2"),sQuery(id+"F0.wireOp",EDGE,"E2.6.13.3"),sQuery(id+"F0.wireOp",EDGE,"E2.6.14.0"),sQuery(id+"F0.wireOp",EDGE,"E2.6.14.1"),sQuery(id+"F0.wireOp",EDGE,"E2.6.14.2"),sQuery(id+"F0.wireOp",EDGE,"E2.6.14.3"),sQuery(id+"F0.wireOp",EDGE,"E2.6.15.0"),sQuery(id+"F0.wireOp",EDGE,"E2.6.15.1"),sQuery(id+"F0.wireOp",EDGE,"E2.6.15.2"),sQuery(id+"F0.wireOp",EDGE,"E2.6.15.3"),sQuery(id+"F0.wireOp",EDGE,"E2.6.16.0"),sQuery(id+"F0.wireOp",EDGE,"E2.6.16.1"),sQuery(id+"F0.wireOp",EDGE,"E2.6.16.2"),sQuery(id+"F0.wireOp",EDGE,"E2.6.16.3"),sQuery(id+"F0.wireOp",EDGE,"E2.6.17.0"),sQuery(id+"F0.wireOp",EDGE,"E2.6.17.1"),sQuery(id+"F0.wireOp",EDGE,"E2.6.17.2"),sQuery(id+"F0.wireOp",EDGE,"E2.6.17.3"),sQuery(id+"F0.wireOp",EDGE,"E2.6.18.0"),sQuery(id+"F0.wireOp",EDGE,"E2.6.18.1"),sQuery(id+"F0.wireOp",EDGE,"E2.6.18.2"),sQuery(id+"F0.wireOp",EDGE,"E2.6.18.3"),sQuery(id+"F0.wireOp",EDGE,"E2.6.19.0"),sQuery(id+"F0.wireOp",EDGE,"E2.6.19.1"),sQuery(id+"F0.wireOp",EDGE,"E2.6.19.2"),sQuery(id+"F0.wireOp",EDGE,"E2.6.19.3"),sQuery(id+"F0.wireOp",EDGE,"E2.6.20.0"),sQuery(id+"F0.wireOp",EDGE,"E2.6.20.1"),sQuery(id+"F0.wireOp",EDGE,"E2.6.20.2"),sQuery(id+"F0.wireOp",EDGE,"E2.6.20.3"),sQuery(id+"F0.wireOp",EDGE,"E2.6.21.0"),sQuery(id+"F0.wireOp",EDGE,"E2.6.21.1"),sQuery(id+"F0.wireOp",EDGE,"E2.6.21.2"),sQuery(id+"F0.wireOp",EDGE,"E2.6.21.3"),sQuery(id+"F0.wireOp",EDGE,"E2.6.22.0"),sQuery(id+"F0.wireOp",EDGE,"E2.6.22.1"),sQuery(id+"F0.wireOp",EDGE,"E2.6.22.2"),sQuery(id+"F0.wireOp",EDGE,"E2.6.22.3"),sQuery(id+"F0.wireOp",EDGE,"E2.6.23.0"),sQuery(id+"F0.wireOp",EDGE,"E2.6.23.1"),sQuery(id+"F0.wireOp",EDGE,"E2.6.23.2"),sQuery(id+"F0.wireOp",EDGE,"E2.6.23.3"),sQuery(id+"F0.wireOp",EDGE,"E2.7.0.0"),sQuery(id+"F0.wireOp",EDGE,"E2.7.0.1"),sQuery(id+"F0.wireOp",EDGE,"E2.7.0.2"),sQuery(id+"F0.wireOp",EDGE,"E2.7.0.3"),sQuery(id+"F0.wireOp",EDGE,"E2.7.1.0"),sQuery(id+"F0.wireOp",EDGE,"E2.7.1.1"),sQuery(id+"F0.wireOp",EDGE,"E2.7.1.2"),sQuery(id+"F0.wireOp",EDGE,"E2.7.1.3"),sQuery(id+"F0.wireOp",EDGE,"E2.7.2.0"),sQuery(id+"F0.wireOp",EDGE,"E2.7.2.1"),sQuery(id+"F0.wireOp",EDGE,"E2.7.2.2"),sQuery(id+"F0.wireOp",EDGE,"E2.7.2.3"),sQuery(id+"F0.wireOp",EDGE,"E2.7.3.0"),sQuery(id+"F0.wireOp",EDGE,"E2.7.3.1"),sQuery(id+"F0.wireOp",EDGE,"E2.7.3.2"),sQuery(id+"F0.wireOp",EDGE,"E2.7.3.3"),sQuery(id+"F0.wireOp",EDGE,"E2.7.4.0"),sQuery(id+"F0.wireOp",EDGE,"E2.7.4.1"),sQuery(id+"F0.wireOp",EDGE,"E2.7.4.2"),sQuery(id+"F0.wireOp",EDGE,"E2.7.4.3"),sQuery(id+"F0.wireOp",EDGE,"E2.7.5.0"),sQuery(id+"F0.wireOp",EDGE,"E2.7.5.1"),sQuery(id+"F0.wireOp",EDGE,"E2.7.5.2"),sQuery(id+"F0.wireOp",EDGE,"E2.7.5.3"),sQuery(id+"F0.wireOp",EDGE,"E2.7.6.0"),sQuery(id+"F0.wireOp",EDGE,"E2.7.6.1"),sQuery(id+"F0.wireOp",EDGE,"E2.7.6.2"),sQuery(id+"F0.wireOp",EDGE,"E2.7.6.3"),sQuery(id+"F0.wireOp",EDGE,"E2.7.7.0"),sQuery(id+"F0.wireOp",EDGE,"E2.7.7.1"),sQuery(id+"F0.wireOp",EDGE,"E2.7.7.2"),sQuery(id+"F0.wireOp",EDGE,"E2.7.7.3"),sQuery(id+"F0.wireOp",EDGE,"E2.7.8.0"),sQuery(id+"F0.wireOp",EDGE,"E2.7.8.1"),sQuery(id+"F0.wireOp",EDGE,"E2.7.8.2"),sQuery(id+"F0.wireOp",EDGE,"E2.7.8.3"),sQuery(id+"F0.wireOp",EDGE,"E2.7.9.0"),sQuery(id+"F0.wireOp",EDGE,"E2.7.9.1"),sQuery(id+"F0.wireOp",EDGE,"E2.7.9.2"),sQuery(id+"F0.wireOp",EDGE,"E2.7.9.3"),sQuery(id+"F0.wireOp",EDGE,"E2.7.10.0"),sQuery(id+"F0.wireOp",EDGE,"E2.7.10.1"),sQuery(id+"F0.wireOp",EDGE,"E2.7.10.2"),sQuery(id+"F0.wireOp",EDGE,"E2.7.10.3"),sQuery(id+"F0.wireOp",EDGE,"E2.7.11.0"),sQuery(id+"F0.wireOp",EDGE,"E2.7.11.1"),sQuery(id+"F0.wireOp",EDGE,"E2.7.11.2"),sQuery(id+"F0.wireOp",EDGE,"E2.7.11.3"),sQuery(id+"F0.wireOp",EDGE,"E2.7.12.0"),sQuery(id+"F0.wireOp",EDGE,"E2.7.12.1"),sQuery(id+"F0.wireOp",EDGE,"E2.7.12.2"),sQuery(id+"F0.wireOp",EDGE,"E2.7.12.3"),sQuery(id+"F0.wireOp",EDGE,"E2.7.13.0"),sQuery(id+"F0.wireOp",EDGE,"E2.7.13.1"),sQuery(id+"F0.wireOp",EDGE,"E2.7.13.2"),sQuery(id+"F0.wireOp",EDGE,"E2.7.13.3"),sQuery(id+"F0.wireOp",EDGE,"E2.7.14.0"),sQuery(id+"F0.wireOp",EDGE,"E2.7.14.1"),sQuery(id+"F0.wireOp",EDGE,"E2.7.14.2"),sQuery(id+"F0.wireOp",EDGE,"E2.7.14.3"),sQuery(id+"F0.wireOp",EDGE,"E2.7.15.0"),sQuery(id+"F0.wireOp",EDGE,"E2.7.15.1"),sQuery(id+"F0.wireOp",EDGE,"E2.7.15.2"),sQuery(id+"F0.wireOp",EDGE,"E2.7.15.3"),sQuery(id+"F0.wireOp",EDGE,"E2.7.16.0"),sQuery(id+"F0.wireOp",EDGE,"E2.7.16.1"),sQuery(id+"F0.wireOp",EDGE,"E2.7.16.2"),sQuery(id+"F0.wireOp",EDGE,"E2.7.16.3"),sQuery(id+"F0.wireOp",EDGE,"E2.7.17.0"),sQuery(id+"F0.wireOp",EDGE,"E2.7.17.1"),sQuery(id+"F0.wireOp",EDGE,"E2.7.17.2"),sQuery(id+"F0.wireOp",EDGE,"E2.7.17.3"),sQuery(id+"F0.wireOp",EDGE,"E2.7.18.0"),sQuery(id+"F0.wireOp",EDGE,"E2.7.18.1"),sQuery(id+"F0.wireOp",EDGE,"E2.7.18.2"),sQuery(id+"F0.wireOp",EDGE,"E2.7.18.3"),sQuery(id+"F0.wireOp",EDGE,"E2.7.19.0"),sQuery(id+"F0.wireOp",EDGE,"E2.7.19.1"),sQuery(id+"F0.wireOp",EDGE,"E2.7.19.2"),sQuery(id+"F0.wireOp",EDGE,"E2.7.19.3"),sQuery(id+"F0.wireOp",EDGE,"E2.7.20.0"),sQuery(id+"F0.wireOp",EDGE,"E2.7.20.1"),sQuery(id+"F0.wireOp",EDGE,"E2.7.20.2"),sQuery(id+"F0.wireOp",EDGE,"E2.7.20.3"),sQuery(id+"F0.wireOp",EDGE,"E2.7.21.0"),sQuery(id+"F0.wireOp",EDGE,"E2.7.21.1"),sQuery(id+"F0.wireOp",EDGE,"E2.7.21.2"),sQuery(id+"F0.wireOp",EDGE,"E2.7.21.3"),sQuery(id+"F0.wireOp",EDGE,"E2.7.22.0"),sQuery(id+"F0.wireOp",EDGE,"E2.7.22.1"),sQuery(id+"F0.wireOp",EDGE,"E2.7.22.2"),sQuery(id+"F0.wireOp",EDGE,"E2.7.22.3"),sQuery(id+"F0.wireOp",EDGE,"E2.7.23.0"),sQuery(id+"F0.wireOp",EDGE,"E2.7.23.1"),sQuery(id+"F0.wireOp",EDGE,"E2.7.23.2"),sQuery(id+"F0.wireOp",EDGE,"E2.7.23.3"),sQuery(id+"F0.wireOp",EDGE,"E2.8.0.0"),sQuery(id+"F0.wireOp",EDGE,"E2.8.0.1"),sQuery(id+"F0.wireOp",EDGE,"E2.8.0.2"),sQuery(id+"F0.wireOp",EDGE,"E2.8.0.3"),sQuery(id+"F0.wireOp",EDGE,"E2.8.1.0"),sQuery(id+"F0.wireOp",EDGE,"E2.8.1.1"),sQuery(id+"F0.wireOp",EDGE,"E2.8.1.2"),sQuery(id+"F0.wireOp",EDGE,"E2.8.1.3"),sQuery(id+"F0.wireOp",EDGE,"E2.8.2.0"),sQuery(id+"F0.wireOp",EDGE,"E2.8.2.1"),sQuery(id+"F0.wireOp",EDGE,"E2.8.2.2"),sQuery(id+"F0.wireOp",EDGE,"E2.8.2.3"),sQuery(id+"F0.wireOp",EDGE,"E2.8.3.0"),sQuery(id+"F0.wireOp",EDGE,"E2.8.3.1"),sQuery(id+"F0.wireOp",EDGE,"E2.8.3.2"),sQuery(id+"F0.wireOp",EDGE,"E2.8.3.3"),sQuery(id+"F0.wireOp",EDGE,"E2.8.4.0"),sQuery(id+"F0.wireOp",EDGE,"E2.8.4.1"),sQuery(id+"F0.wireOp",EDGE,"E2.8.4.2"),sQuery(id+"F0.wireOp",EDGE,"E2.8.4.3"),sQuery(id+"F0.wireOp",EDGE,"E2.8.5.0"),sQuery(id+"F0.wireOp",EDGE,"E2.8.5.1"),sQuery(id+"F0.wireOp",EDGE,"E2.8.5.2"),sQuery(id+"F0.wireOp",EDGE,"E2.8.5.3"),sQuery(id+"F0.wireOp",EDGE,"E2.8.6.0"),sQuery(id+"F0.wireOp",EDGE,"E2.8.6.1"),sQuery(id+"F0.wireOp",EDGE,"E2.8.6.2"),sQuery(id+"F0.wireOp",EDGE,"E2.8.6.3"),sQuery(id+"F0.wireOp",EDGE,"E2.8.7.0"),sQuery(id+"F0.wireOp",EDGE,"E2.8.7.1"),sQuery(id+"F0.wireOp",EDGE,"E2.8.7.2"),sQuery(id+"F0.wireOp",EDGE,"E2.8.7.3"),sQuery(id+"F0.wireOp",EDGE,"E2.8.8.0"),sQuery(id+"F0.wireOp",EDGE,"E2.8.8.1"),sQuery(id+"F0.wireOp",EDGE,"E2.8.8.2"),sQuery(id+"F0.wireOp",EDGE,"E2.8.8.3"),sQuery(id+"F0.wireOp",EDGE,"E2.8.9.0"),sQuery(id+"F0.wireOp",EDGE,"E2.8.9.1"),sQuery(id+"F0.wireOp",EDGE,"E2.8.9.2"),sQuery(id+"F0.wireOp",EDGE,"E2.8.9.3"),sQuery(id+"F0.wireOp",EDGE,"E2.8.10.0"),sQuery(id+"F0.wireOp",EDGE,"E2.8.10.1"),sQuery(id+"F0.wireOp",EDGE,"E2.8.10.2"),sQuery(id+"F0.wireOp",EDGE,"E2.8.10.3"),sQuery(id+"F0.wireOp",EDGE,"E2.8.11.0"),sQuery(id+"F0.wireOp",EDGE,"E2.8.11.1"),sQuery(id+"F0.wireOp",EDGE,"E2.8.11.2"),sQuery(id+"F0.wireOp",EDGE,"E2.8.11.3"),sQuery(id+"F0.wireOp",EDGE,"E2.8.12.0"),sQuery(id+"F0.wireOp",EDGE,"E2.8.12.1"),sQuery(id+"F0.wireOp",EDGE,"E2.8.12.2"),sQuery(id+"F0.wireOp",EDGE,"E2.8.12.3"),sQuery(id+"F0.wireOp",EDGE,"E2.8.13.0"),sQuery(id+"F0.wireOp",EDGE,"E2.8.13.1"),sQuery(id+"F0.wireOp",EDGE,"E2.8.13.2"),sQuery(id+"F0.wireOp",EDGE,"E2.8.13.3"),sQuery(id+"F0.wireOp",EDGE,"E2.8.14.0"),sQuery(id+"F0.wireOp",EDGE,"E2.8.14.1"),sQuery(id+"F0.wireOp",EDGE,"E2.8.14.2"),sQuery(id+"F0.wireOp",EDGE,"E2.8.14.3"),sQuery(id+"F0.wireOp",EDGE,"E2.8.15.0"),sQuery(id+"F0.wireOp",EDGE,"E2.8.15.1"),sQuery(id+"F0.wireOp",EDGE,"E2.8.15.2"),sQuery(id+"F0.wireOp",EDGE,"E2.8.15.3"),sQuery(id+"F0.wireOp",EDGE,"E2.8.16.0"),sQuery(id+"F0.wireOp",EDGE,"E2.8.16.1"),sQuery(id+"F0.wireOp",EDGE,"E2.8.16.2"),sQuery(id+"F0.wireOp",EDGE,"E2.8.16.3"),sQuery(id+"F0.wireOp",EDGE,"E2.8.17.0"),sQuery(id+"F0.wireOp",EDGE,"E2.8.17.1"),sQuery(id+"F0.wireOp",EDGE,"E2.8.17.2"),sQuery(id+"F0.wireOp",EDGE,"E2.8.17.3"),sQuery(id+"F0.wireOp",EDGE,"E2.8.18.0"),sQuery(id+"F0.wireOp",EDGE,"E2.8.18.1"),sQuery(id+"F0.wireOp",EDGE,"E2.8.18.2"),sQuery(id+"F0.wireOp",EDGE,"E2.8.18.3"),sQuery(id+"F0.wireOp",EDGE,"E2.8.19.0"),sQuery(id+"F0.wireOp",EDGE,"E2.8.19.1"),sQuery(id+"F0.wireOp",EDGE,"E2.8.19.2"),sQuery(id+"F0.wireOp",EDGE,"E2.8.19.3"),sQuery(id+"F0.wireOp",EDGE,"E2.8.20.0"),sQuery(id+"F0.wireOp",EDGE,"E2.8.20.1"),sQuery(id+"F0.wireOp",EDGE,"E2.8.20.2"),sQuery(id+"F0.wireOp",EDGE,"E2.8.20.3"),sQuery(id+"F0.wireOp",EDGE,"E2.8.21.0"),sQuery(id+"F0.wireOp",EDGE,"E2.8.21.1"),sQuery(id+"F0.wireOp",EDGE,"E2.8.21.2"),sQuery(id+"F0.wireOp",EDGE,"E2.8.21.3"),sQuery(id+"F0.wireOp",EDGE,"E2.8.22.0"),sQuery(id+"F0.wireOp",EDGE,"E2.8.22.1"),sQuery(id+"F0.wireOp",EDGE,"E2.8.22.2"),sQuery(id+"F0.wireOp",EDGE,"E2.8.22.3"),sQuery(id+"F0.wireOp",EDGE,"E2.8.23.0"),sQuery(id+"F0.wireOp",EDGE,"E2.8.23.1"),sQuery(id+"F0.wireOp",EDGE,"E2.8.23.2"),sQuery(id+"F0.wireOp",EDGE,"E2.8.23.3"),sQuery(id+"F0.wireOp",EDGE,"E2.9.0.0"),sQuery(id+"F0.wireOp",EDGE,"E2.9.0.1"),sQuery(id+"F0.wireOp",EDGE,"E2.9.0.2"),sQuery(id+"F0.wireOp",EDGE,"E2.9.0.3"),sQuery(id+"F0.wireOp",EDGE,"E2.9.1.0"),sQuery(id+"F0.wireOp",EDGE,"E2.9.1.1"),sQuery(id+"F0.wireOp",EDGE,"E2.9.1.2"),sQuery(id+"F0.wireOp",EDGE,"E2.9.1.3"),sQuery(id+"F0.wireOp",EDGE,"E2.9.2.0"),sQuery(id+"F0.wireOp",EDGE,"E2.9.2.1"),sQuery(id+"F0.wireOp",EDGE,"E2.9.2.2"),sQuery(id+"F0.wireOp",EDGE,"E2.9.2.3"),sQuery(id+"F0.wireOp",EDGE,"E2.9.3.0"),sQuery(id+"F0.wireOp",EDGE,"E2.9.3.1"),sQuery(id+"F0.wireOp",EDGE,"E2.9.3.2"),sQuery(id+"F0.wireOp",EDGE,"E2.9.3.3"),sQuery(id+"F0.wireOp",EDGE,"E2.9.4.0"),sQuery(id+"F0.wireOp",EDGE,"E2.9.4.1"),sQuery(id+"F0.wireOp",EDGE,"E2.9.4.2"),sQuery(id+"F0.wireOp",EDGE,"E2.9.4.3"),sQuery(id+"F0.wireOp",EDGE,"E2.9.5.0"),sQuery(id+"F0.wireOp",EDGE,"E2.9.5.1"),sQuery(id+"F0.wireOp",EDGE,"E2.9.5.2"),sQuery(id+"F0.wireOp",EDGE,"E2.9.5.3"),sQuery(id+"F0.wireOp",EDGE,"E2.9.6.0"),sQuery(id+"F0.wireOp",EDGE,"E2.9.6.1"),sQuery(id+"F0.wireOp",EDGE,"E2.9.6.2"),sQuery(id+"F0.wireOp",EDGE,"E2.9.6.3"),sQuery(id+"F0.wireOp",EDGE,"E2.9.7.0"),sQuery(id+"F0.wireOp",EDGE,"E2.9.7.1"),sQuery(id+"F0.wireOp",EDGE,"E2.9.7.2"),sQuery(id+"F0.wireOp",EDGE,"E2.9.7.3"),sQuery(id+"F0.wireOp",EDGE,"E2.9.8.0"),sQuery(id+"F0.wireOp",EDGE,"E2.9.8.1"),sQuery(id+"F0.wireOp",EDGE,"E2.9.8.2"),sQuery(id+"F0.wireOp",EDGE,"E2.9.8.3"),sQuery(id+"F0.wireOp",EDGE,"E2.9.9.0"),sQuery(id+"F0.wireOp",EDGE,"E2.9.9.1"),sQuery(id+"F0.wireOp",EDGE,"E2.9.9.2"),sQuery(id+"F0.wireOp",EDGE,"E2.9.9.3"),sQuery(id+"F0.wireOp",EDGE,"E2.9.10.0"),sQuery(id+"F0.wireOp",EDGE,"E2.9.10.1"),sQuery(id+"F0.wireOp",EDGE,"E2.9.10.2"),sQuery(id+"F0.wireOp",EDGE,"E2.9.10.3"),sQuery(id+"F0.wireOp",EDGE,"E2.9.11.0"),sQuery(id+"F0.wireOp",EDGE,"E2.9.11.1"),sQuery(id+"F0.wireOp",EDGE,"E2.9.11.2"),sQuery(id+"F0.wireOp",EDGE,"E2.9.11.3"),sQuery(id+"F0.wireOp",EDGE,"E2.9.12.0"),sQuery(id+"F0.wireOp",EDGE,"E2.9.12.1"),sQuery(id+"F0.wireOp",EDGE,"E2.9.12.2"),sQuery(id+"F0.wireOp",EDGE,"E2.9.12.3"),sQuery(id+"F0.wireOp",EDGE,"E2.9.13.0"),sQuery(id+"F0.wireOp",EDGE,"E2.9.13.1"),sQuery(id+"F0.wireOp",EDGE,"E2.9.13.2"),sQuery(id+"F0.wireOp",EDGE,"E2.9.13.3"),sQuery(id+"F0.wireOp",EDGE,"E2.9.14.0"),sQuery(id+"F0.wireOp",EDGE,"E2.9.14.1"),sQuery(id+"F0.wireOp",EDGE,"E2.9.14.2"),sQuery(id+"F0.wireOp",EDGE,"E2.9.14.3"),sQuery(id+"F0.wireOp",EDGE,"E2.9.15.0"),sQuery(id+"F0.wireOp",EDGE,"E2.9.15.1"),sQuery(id+"F0.wireOp",EDGE,"E2.9.15.2"),sQuery(id+"F0.wireOp",EDGE,"E2.9.15.3"),sQuery(id+"F0.wireOp",EDGE,"E2.9.16.0"),sQuery(id+"F0.wireOp",EDGE,"E2.9.16.1"),sQuery(id+"F0.wireOp",EDGE,"E2.9.16.2"),sQuery(id+"F0.wireOp",EDGE,"E2.9.16.3"),sQuery(id+"F0.wireOp",EDGE,"E2.9.17.0"),sQuery(id+"F0.wireOp",EDGE,"E2.9.17.1"),sQuery(id+"F0.wireOp",EDGE,"E2.9.17.2"),sQuery(id+"F0.wireOp",EDGE,"E2.9.17.3"),sQuery(id+"F0.wireOp",EDGE,"E2.9.18.0"),sQuery(id+"F0.wireOp",EDGE,"E2.9.18.1"),sQuery(id+"F0.wireOp",EDGE,"E2.9.18.2"),sQuery(id+"F0.wireOp",EDGE,"E2.9.18.3"),sQuery(id+"F0.wireOp",EDGE,"E2.9.19.0"),sQuery(id+"F0.wireOp",EDGE,"E2.9.19.1"),sQuery(id+"F0.wireOp",EDGE,"E2.9.19.2"),sQuery(id+"F0.wireOp",EDGE,"E2.9.19.3"),sQuery(id+"F0.wireOp",EDGE,"E2.9.20.0"),sQuery(id+"F0.wireOp",EDGE,"E2.9.20.1"),sQuery(id+"F0.wireOp",EDGE,"E2.9.20.2"),sQuery(id+"F0.wireOp",EDGE,"E2.9.20.3"),sQuery(id+"F0.wireOp",EDGE,"E2.9.21.0"),sQuery(id+"F0.wireOp",EDGE,"E2.9.21.1"),sQuery(id+"F0.wireOp",EDGE,"E2.9.21.2"),sQuery(id+"F0.wireOp",EDGE,"E2.9.21.3"),sQuery(id+"F0.wireOp",EDGE,"E2.9.22.0"),sQuery(id+"F0.wireOp",EDGE,"E2.9.22.1"),sQuery(id+"F0.wireOp",EDGE,"E2.9.22.2"),sQuery(id+"F0.wireOp",EDGE,"E2.9.22.3"),sQuery(id+"F0.wireOp",EDGE,"E2.9.23.0"),sQuery(id+"F0.wireOp",EDGE,"E2.9.23.1"),sQuery(id+"F0.wireOp",EDGE,"E2.9.23.2"),sQuery(id+"F0.wireOp",EDGE,"E2.9.23.3"),sQuery(id+"F0.wireOp",EDGE,"E2.10.0.0"),sQuery(id+"F0.wireOp",EDGE,"E2.10.0.1"),sQuery(id+"F0.wireOp",EDGE,"E2.10.0.2"),sQuery(id+"F0.wireOp",EDGE,"E2.10.0.3"),sQuery(id+"F0.wireOp",EDGE,"E2.10.1.0"),sQuery(id+"F0.wireOp",EDGE,"E2.10.1.1"),sQuery(id+"F0.wireOp",EDGE,"E2.10.1.2"),sQuery(id+"F0.wireOp",EDGE,"E2.10.1.3"),sQuery(id+"F0.wireOp",EDGE,"E2.10.2.0"),sQuery(id+"F0.wireOp",EDGE,"E2.10.2.1"),sQuery(id+"F0.wireOp",EDGE,"E2.10.2.2"),sQuery(id+"F0.wireOp",EDGE,"E2.10.2.3"),sQuery(id+"F0.wireOp",EDGE,"E2.10.3.0"),sQuery(id+"F0.wireOp",EDGE,"E2.10.3.1"),sQuery(id+"F0.wireOp",EDGE,"E2.10.3.2"),sQuery(id+"F0.wireOp",EDGE,"E2.10.3.3"),sQuery(id+"F0.wireOp",EDGE,"E2.10.4.0"),sQuery(id+"F0.wireOp",EDGE,"E2.10.4.1"),sQuery(id+"F0.wireOp",EDGE,"E2.10.4.2"),sQuery(id+"F0.wireOp",EDGE,"E2.10.4.3"),sQuery(id+"F0.wireOp",EDGE,"E2.10.5.0"),sQuery(id+"F0.wireOp",EDGE,"E2.10.5.1"),sQuery(id+"F0.wireOp",EDGE,"E2.10.5.2"),sQuery(id+"F0.wireOp",EDGE,"E2.10.5.3"),sQuery(id+"F0.wireOp",EDGE,"E2.10.6.0"),sQuery(id+"F0.wireOp",EDGE,"E2.10.6.1"),sQuery(id+"F0.wireOp",EDGE,"E2.10.6.2"),sQuery(id+"F0.wireOp",EDGE,"E2.10.6.3"),sQuery(id+"F0.wireOp",EDGE,"E2.10.7.0"),sQuery(id+"F0.wireOp",EDGE,"E2.10.7.1"),sQuery(id+"F0.wireOp",EDGE,"E2.10.7.2"),sQuery(id+"F0.wireOp",EDGE,"E2.10.7.3"),sQuery(id+"F0.wireOp",EDGE,"E2.10.8.0"),sQuery(id+"F0.wireOp",EDGE,"E2.10.8.1"),sQuery(id+"F0.wireOp",EDGE,"E2.10.8.2"),sQuery(id+"F0.wireOp",EDGE,"E2.10.8.3"),sQuery(id+"F0.wireOp",EDGE,"E2.10.9.0"),sQuery(id+"F0.wireOp",EDGE,"E2.10.9.1"),sQuery(id+"F0.wireOp",EDGE,"E2.10.9.2"),sQuery(id+"F0.wireOp",EDGE,"E2.10.9.3"),sQuery(id+"F0.wireOp",EDGE,"E2.10.10.0"),sQuery(id+"F0.wireOp",EDGE,"E2.10.10.1"),sQuery(id+"F0.wireOp",EDGE,"E2.10.10.2"),sQuery(id+"F0.wireOp",EDGE,"E2.10.10.3"),sQuery(id+"F0.wireOp",EDGE,"E2.10.11.0"),sQuery(id+"F0.wireOp",EDGE,"E2.10.11.1"),sQuery(id+"F0.wireOp",EDGE,"E2.10.11.2"),sQuery(id+"F0.wireOp",EDGE,"E2.10.11.3"),sQuery(id+"F0.wireOp",EDGE,"E2.10.12.0"),sQuery(id+"F0.wireOp",EDGE,"E2.10.12.1"),sQuery(id+"F0.wireOp",EDGE,"E2.10.12.2"),sQuery(id+"F0.wireOp",EDGE,"E2.10.12.3"),sQuery(id+"F0.wireOp",EDGE,"E2.10.13.0"),sQuery(id+"F0.wireOp",EDGE,"E2.10.13.1"),sQuery(id+"F0.wireOp",EDGE,"E2.10.13.2"),sQuery(id+"F0.wireOp",EDGE,"E2.10.13.3"),sQuery(id+"F0.wireOp",EDGE,"E2.10.14.0"),sQuery(id+"F0.wireOp",EDGE,"E2.10.14.1"),sQuery(id+"F0.wireOp",EDGE,"E2.10.14.2"),sQuery(id+"F0.wireOp",EDGE,"E2.10.14.3"),sQuery(id+"F0.wireOp",EDGE,"E2.10.15.0"),sQuery(id+"F0.wireOp",EDGE,"E2.10.15.1"),sQuery(id+"F0.wireOp",EDGE,"E2.10.15.2"),sQuery(id+"F0.wireOp",EDGE,"E2.10.15.3"),sQuery(id+"F0.wireOp",EDGE,"E2.10.16.0"),sQuery(id+"F0.wireOp",EDGE,"E2.10.16.1"),sQuery(id+"F0.wireOp",EDGE,"E2.10.16.2"),sQuery(id+"F0.wireOp",EDGE,"E2.10.16.3"),sQuery(id+"F0.wireOp",EDGE,"E2.10.17.0"),sQuery(id+"F0.wireOp",EDGE,"E2.10.17.1"),sQuery(id+"F0.wireOp",EDGE,"E2.10.17.2"),sQuery(id+"F0.wireOp",EDGE,"E2.10.17.3"),sQuery(id+"F0.wireOp",EDGE,"E2.10.18.0"),sQuery(id+"F0.wireOp",EDGE,"E2.10.18.1"),sQuery(id+"F0.wireOp",EDGE,"E2.10.18.2"),sQuery(id+"F0.wireOp",EDGE,"E2.10.18.3"),sQuery(id+"F0.wireOp",EDGE,"E2.10.19.0"),sQuery(id+"F0.wireOp",EDGE,"E2.10.19.1"),sQuery(id+"F0.wireOp",EDGE,"E2.10.19.2"),sQuery(id+"F0.wireOp",EDGE,"E2.10.19.3"),sQuery(id+"F0.wireOp",EDGE,"E2.10.20.0"),sQuery(id+"F0.wireOp",EDGE,"E2.10.20.1"),sQuery(id+"F0.wireOp",EDGE,"E2.10.20.2"),sQuery(id+"F0.wireOp",EDGE,"E2.10.20.3"),sQuery(id+"F0.wireOp",EDGE,"E2.10.21.0"),sQuery(id+"F0.wireOp",EDGE,"E2.10.21.1"),sQuery(id+"F0.wireOp",EDGE,"E2.10.21.2"),sQuery(id+"F0.wireOp",EDGE,"E2.10.21.3"),sQuery(id+"F0.wireOp",EDGE,"E2.10.22.0"),sQuery(id+"F0.wireOp",EDGE,"E2.10.22.1"),sQuery(id+"F0.wireOp",EDGE,"E2.10.22.2"),sQuery(id+"F0.wireOp",EDGE,"E2.10.22.3"),sQuery(id+"F0.wireOp",EDGE,"E2.10.23.0"),sQuery(id+"F0.wireOp",EDGE,"E2.10.23.1"),sQuery(id+"F0.wireOp",EDGE,"E2.10.23.2"),sQuery(id+"F0.wireOp",EDGE,"E2.10.23.3"),sQuery(id+"F0.wireOp",EDGE,"E2.11.0.0"),sQuery(id+"F0.wireOp",EDGE,"E2.11.0.1"),sQuery(id+"F0.wireOp",EDGE,"E2.11.0.2"),sQuery(id+"F0.wireOp",EDGE,"E2.11.0.3"),sQuery(id+"F0.wireOp",EDGE,"E2.11.1.0"),sQuery(id+"F0.wireOp",EDGE,"E2.11.1.1"),sQuery(id+"F0.wireOp",EDGE,"E2.11.1.2"),sQuery(id+"F0.wireOp",EDGE,"E2.11.1.3"),sQuery(id+"F0.wireOp",EDGE,"E2.11.2.0"),sQuery(id+"F0.wireOp",EDGE,"E2.11.2.1"),sQuery(id+"F0.wireOp",EDGE,"E2.11.2.2"),sQuery(id+"F0.wireOp",EDGE,"E2.11.2.3"),sQuery(id+"F0.wireOp",EDGE,"E2.11.3.0"),sQuery(id+"F0.wireOp",EDGE,"E2.11.3.1"),sQuery(id+"F0.wireOp",EDGE,"E2.11.3.2"),sQuery(id+"F0.wireOp",EDGE,"E2.11.3.3"),sQuery(id+"F0.wireOp",EDGE,"E2.11.4.0"),sQuery(id+"F0.wireOp",EDGE,"E2.11.4.1"),sQuery(id+"F0.wireOp",EDGE,"E2.11.4.2"),sQuery(id+"F0.wireOp",EDGE,"E2.11.4.3"),sQuery(id+"F0.wireOp",EDGE,"E2.11.5.0"),sQuery(id+"F0.wireOp",EDGE,"E2.11.5.1"),sQuery(id+"F0.wireOp",EDGE,"E2.11.5.2"),sQuery(id+"F0.wireOp",EDGE,"E2.11.5.3"),sQuery(id+"F0.wireOp",EDGE,"E2.11.6.0"),sQuery(id+"F0.wireOp",EDGE,"E2.11.6.1"),sQuery(id+"F0.wireOp",EDGE,"E2.11.6.2"),sQuery(id+"F0.wireOp",EDGE,"E2.11.6.3"),sQuery(id+"F0.wireOp",EDGE,"E2.11.7.0"),sQuery(id+"F0.wireOp",EDGE,"E2.11.7.1"),sQuery(id+"F0.wireOp",EDGE,"E2.11.7.2"),sQuery(id+"F0.wireOp",EDGE,"E2.11.7.3"),sQuery(id+"F0.wireOp",EDGE,"E2.11.8.0"),sQuery(id+"F0.wireOp",EDGE,"E2.11.8.1"),sQuery(id+"F0.wireOp",EDGE,"E2.11.8.2"),sQuery(id+"F0.wireOp",EDGE,"E2.11.8.3"),sQuery(id+"F0.wireOp",EDGE,"E2.11.9.0"),sQuery(id+"F0.wireOp",EDGE,"E2.11.9.1"),sQuery(id+"F0.wireOp",EDGE,"E2.11.9.2"),sQuery(id+"F0.wireOp",EDGE,"E2.11.9.3"),sQuery(id+"F0.wireOp",EDGE,"E2.11.10.0"),sQuery(id+"F0.wireOp",EDGE,"E2.11.10.1"),sQuery(id+"F0.wireOp",EDGE,"E2.11.10.2"),sQuery(id+"F0.wireOp",EDGE,"E2.11.10.3"),sQuery(id+"F0.wireOp",EDGE,"E2.11.11.0"),sQuery(id+"F0.wireOp",EDGE,"E2.11.11.1"),sQuery(id+"F0.wireOp",EDGE,"E2.11.11.2"),sQuery(id+"F0.wireOp",EDGE,"E2.11.11.3"),sQuery(id+"F0.wireOp",EDGE,"E2.11.12.0"),sQuery(id+"F0.wireOp",EDGE,"E2.11.12.1"),sQuery(id+"F0.wireOp",EDGE,"E2.11.12.2"),sQuery(id+"F0.wireOp",EDGE,"E2.11.12.3"),sQuery(id+"F0.wireOp",EDGE,"E2.11.13.0"),sQuery(id+"F0.wireOp",EDGE,"E2.11.13.1"),sQuery(id+"F0.wireOp",EDGE,"E2.11.13.2"),sQuery(id+"F0.wireOp",EDGE,"E2.11.13.3"),sQuery(id+"F0.wireOp",EDGE,"E2.11.14.0"),sQuery(id+"F0.wireOp",EDGE,"E2.11.14.1"),sQuery(id+"F0.wireOp",EDGE,"E2.11.14.2"),sQuery(id+"F0.wireOp",EDGE,"E2.11.14.3"),sQuery(id+"F0.wireOp",EDGE,"E2.11.15.0"),sQuery(id+"F0.wireOp",EDGE,"E2.11.15.1"),sQuery(id+"F0.wireOp",EDGE,"E2.11.15.2"),sQuery(id+"F0.wireOp",EDGE,"E2.11.15.3"),sQuery(id+"F0.wireOp",EDGE,"E2.11.16.0"),sQuery(id+"F0.wireOp",EDGE,"E2.11.16.1"),sQuery(id+"F0.wireOp",EDGE,"E2.11.16.2"),sQuery(id+"F0.wireOp",EDGE,"E2.11.16.3"),sQuery(id+"F0.wireOp",EDGE,"E2.11.17.0"),sQuery(id+"F0.wireOp",EDGE,"E2.11.17.1"),sQuery(id+"F0.wireOp",EDGE,"E2.11.17.2"),sQuery(id+"F0.wireOp",EDGE,"E2.11.17.3"),sQuery(id+"F0.wireOp",EDGE,"E2.11.18.0"),sQuery(id+"F0.wireOp",EDGE,"E2.11.18.1"),sQuery(id+"F0.wireOp",EDGE,"E2.11.18.2"),sQuery(id+"F0.wireOp",EDGE,"E2.11.18.3"),sQuery(id+"F0.wireOp",EDGE,"E2.11.19.0"),sQuery(id+"F0.wireOp",EDGE,"E2.11.19.1"),sQuery(id+"F0.wireOp",EDGE,"E2.11.19.2"),sQuery(id+"F0.wireOp",EDGE,"E2.11.19.3"),sQuery(id+"F0.wireOp",EDGE,"E2.11.20.0"),sQuery(id+"F0.wireOp",EDGE,"E2.11.20.1"),sQuery(id+"F0.wireOp",EDGE,"E2.11.20.2"),sQuery(id+"F0.wireOp",EDGE,"E2.11.20.3"),sQuery(id+"F0.wireOp",EDGE,"E2.11.21.0"),sQuery(id+"F0.wireOp",EDGE,"E2.11.21.1"),sQuery(id+"F0.wireOp",EDGE,"E2.11.21.2"),sQuery(id+"F0.wireOp",EDGE,"E2.11.21.3"),sQuery(id+"F0.wireOp",EDGE,"E2.11.22.0"),sQuery(id+"F0.wireOp",EDGE,"E2.11.22.1"),sQuery(id+"F0.wireOp",EDGE,"E2.11.22.2"),sQuery(id+"F0.wireOp",EDGE,"E2.11.22.3"),sQuery(id+"F0.wireOp",EDGE,"E2.11.23.0"),sQuery(id+"F0.wireOp",EDGE,"E2.11.23.1"),sQuery(id+"F0.wireOp",EDGE,"E2.11.23.2"),sQuery(id+"F0.wireOp",EDGE,"E2.11.23.3")])]});
            transform(context, id + "F2", {"entities" : qUnion([Q0]), "transformType" : TransformType.TRANSLATION_3D, "dx" : 0 * mm, "dy" : 0 * mm, "dz" : 0 * mm, "makeCopy" : true});
        }
    });
